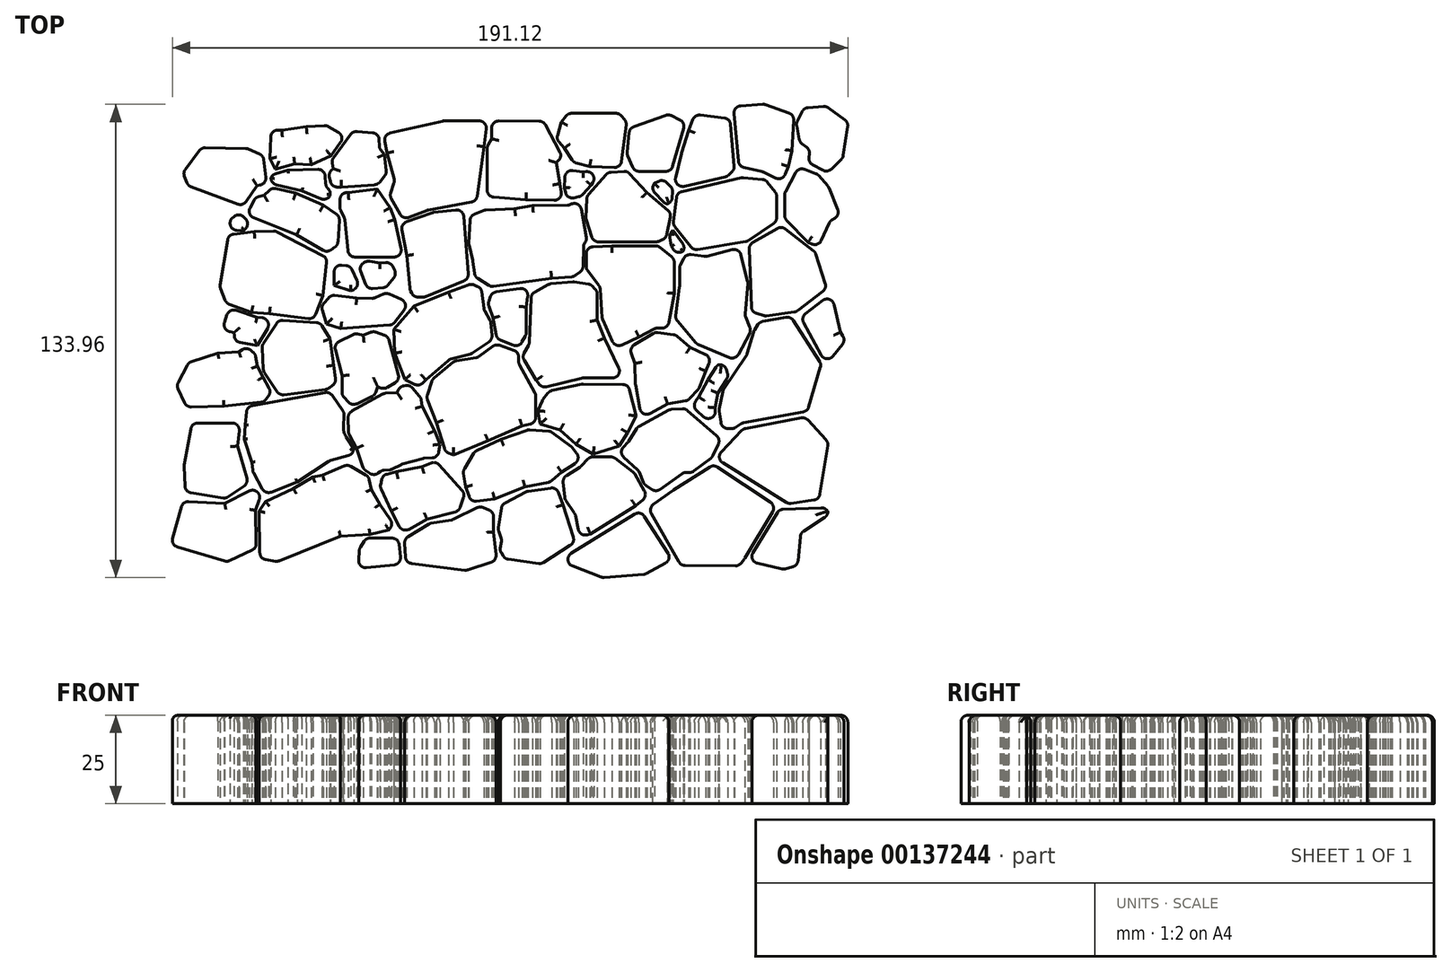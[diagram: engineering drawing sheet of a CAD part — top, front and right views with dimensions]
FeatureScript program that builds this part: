
annotation { "Feature Type Name" : "Feature", "Feature Type Description" : "" }
export const myFeature = defineFeature(function(context is Context, id is Id, definition is map)
    precondition{}
    {
        {
            var Q0;
            Q0=qCreatedBy(makeId("Top.planeOp"),FACE);
            var sketch = newSketch(context, id + "F0", { "sketchPlane" : qUnion([Q0])});
            skLineSegment(sketch, "E0", {"start": v(54.67, -32.32) * mm, "end": v(75.4, -45.2) * mm});
            skLineSegment(sketch, "E1", {"start": v(75.4, -45.2) * mm, "end": v(84.05, -43.94) * mm});
            skLineSegment(sketch, "E2", {"start": v(84.05, -43.94) * mm, "end": v(86.64, -27.84) * mm});
            skLineSegment(sketch, "E3", {"start": v(86.64, -27.84) * mm, "end": v(80.12, -20.7) * mm});
            skLineSegment(sketch, "E4", {"start": v(80.12, -20.7) * mm, "end": v(62.6, -24) * mm});
            skLineSegment(sketch, "E5", {"start": v(62.6, -24) * mm, "end": v(54.67, -32.32) * mm});
            skLineSegment(sketch, "E6", {"start": v(56.48, -23.92) * mm, "end": v(59.93, -23.92) * mm});
            skLineSegment(sketch, "E7", {"start": v(59.93, -23.92) * mm, "end": v(62.3, -22.35) * mm});
            skLineSegment(sketch, "E8", {"start": v(62.3, -22.35) * mm, "end": v(80.75, -18.97) * mm});
            skLineSegment(sketch, "E9", {"start": v(80.75, -18.97) * mm, "end": v(84.67, -5.7) * mm});
            skLineSegment(sketch, "E10", {"start": v(84.67, -5.7) * mm, "end": v(76.04, 7.81) * mm});
            skLineSegment(sketch, "E11", {"start": v(76.04, 7.81) * mm, "end": v(67.24, 6.24) * mm});
            skLineSegment(sketch, "E12", {"start": v(67.24, 6.24) * mm, "end": v(65.59, 3.8) * mm});
            skLineSegment(sketch, "E13", {"start": v(65.59, 3.8) * mm, "end": v(63.63, -3.03) * mm});
            skLineSegment(sketch, "E14", {"start": v(63.63, -3.03) * mm, "end": v(56.87, -13.08) * mm});
            skLineSegment(sketch, "E15", {"start": v(56.87, -13.08) * mm, "end": v(55.77, -18.65) * mm});
            skLineSegment(sketch, "E16", {"start": v(55.77, -18.65) * mm, "end": v(56.48, -23.92) * mm});
            skLineSegment(sketch, "E17", {"start": v(78.86, 7.58) * mm, "end": v(86.09, -5.77) * mm});
            skLineSegment(sketch, "E18", {"start": v(86.09, -5.77) * mm, "end": v(91.59, 1.14) * mm});
            skLineSegment(sketch, "E19", {"start": v(91.59, 1.14) * mm, "end": v(90.02, 3.34) * mm});
            skLineSegment(sketch, "E20", {"start": v(90.02, 3.34) * mm, "end": v(87.58, 14.25) * mm});
            skLineSegment(sketch, "E21", {"start": v(87.58, 14.25) * mm, "end": v(78.86, 7.58) * mm});
            skLineSegment(sketch, "E22", {"start": v(77.53, 9.15) * mm, "end": v(86.23, 15.81) * mm});
            skLineSegment(sketch, "E23", {"start": v(86.23, 15.81) * mm, "end": v(82.95, 26.03) * mm});
            skLineSegment(sketch, "E24", {"start": v(82.95, 26.03) * mm, "end": v(73.44, 33.42) * mm});
            skLineSegment(sketch, "E25", {"start": v(73.44, 33.42) * mm, "end": v(64.25, 28.15) * mm});
            skLineSegment(sketch, "E26", {"start": v(64.25, 28.15) * mm, "end": v(64.96, 9.07) * mm});
            skLineSegment(sketch, "E27", {"start": v(64.96, 9.07) * mm, "end": v(68.73, 7.97) * mm});
            skLineSegment(sketch, "E28", {"start": v(68.73, 7.97) * mm, "end": v(77.53, 9.15) * mm});
            skLineSegment(sketch, "E29", {"start": v(83.89, 27.6) * mm, "end": v(87.19, 34.83) * mm});
            skLineSegment(sketch, "E30", {"start": v(87.19, 34.83) * mm, "end": v(89.94, 36.56) * mm});
            skLineSegment(sketch, "E31", {"start": v(89.94, 36.56) * mm, "end": v(86.72, 44.5) * mm});
            skLineSegment(sketch, "E32", {"start": v(86.72, 44.5) * mm, "end": v(83.57, 48.1) * mm});
            skLineSegment(sketch, "E33", {"start": v(83.57, 48.1) * mm, "end": v(78.23, 50.07) * mm});
            skLineSegment(sketch, "E34", {"start": v(78.23, 50.07) * mm, "end": v(74.3, 42.76) * mm});
            skLineSegment(sketch, "E35", {"start": v(74.3, 42.76) * mm, "end": v(74.3, 35.62) * mm});
            skLineSegment(sketch, "E36", {"start": v(74.3, 35.62) * mm, "end": v(80.9, 28.78) * mm});
            skLineSegment(sketch, "E37", {"start": v(80.9, 28.78) * mm, "end": v(83.89, 27.6) * mm});
            skLineSegment(sketch, "E38", {"start": v(72.03, 34.75) * mm, "end": v(72.03, 42.53) * mm});
            skLineSegment(sketch, "E39", {"start": v(72.03, 42.53) * mm, "end": v(68.89, 46.53) * mm});
            skLineSegment(sketch, "E40", {"start": v(68.89, 46.53) * mm, "end": v(62.3, 47.16) * mm});
            skLineSegment(sketch, "E41", {"start": v(62.3, 47.16) * mm, "end": v(43.83, 42.84) * mm});
            skLineSegment(sketch, "E42", {"start": v(43.83, 42.84) * mm, "end": v(42.73, 33.89) * mm});
            skLineSegment(sketch, "E43", {"start": v(42.73, 33.89) * mm, "end": v(48.55, 26.58) * mm});
            skLineSegment(sketch, "E44", {"start": v(48.55, 26.58) * mm, "end": v(63.7, 29.1) * mm});
            skLineSegment(sketch, "E45", {"start": v(63.7, 29.1) * mm, "end": v(72.03, 34.75) * mm});
            skLineSegment(sketch, "E46", {"start": v(46.35, 25.48) * mm, "end": v(51.92, 24.78) * mm});
            skLineSegment(sketch, "E47", {"start": v(51.92, 24.78) * mm, "end": v(61.43, 27.21) * mm});
            skLineSegment(sketch, "E48", {"start": v(61.43, 27.21) * mm, "end": v(63.92, 17.47) * mm});
            skLineSegment(sketch, "E49", {"start": v(63.92, 17.47) * mm, "end": v(63.08, 8.13) * mm});
            skLineSegment(sketch, "E50", {"start": v(63.08, 8.13) * mm, "end": v(64.8, 3.89) * mm});
            skLineSegment(sketch, "E51", {"start": v(64.8, 3.89) * mm, "end": v(60.33, -4.52) * mm});
            skLineSegment(sketch, "E52", {"start": v(60.33, -4.52) * mm, "end": v(49.49, 0) * mm});
            skLineSegment(sketch, "E53", {"start": v(49.49, 0) * mm, "end": v(43.36, 7.26) * mm});
            skLineSegment(sketch, "E54", {"start": v(43.36, 7.26) * mm, "end": v(44.54, 16.06) * mm});
            skLineSegment(sketch, "E55", {"start": v(44.54, 16.06) * mm, "end": v(44.54, 21.87) * mm});
            skLineSegment(sketch, "E56", {"start": v(44.54, 21.87) * mm, "end": v(46.35, 25.48) * mm});
            skLineSegment(sketch, "E57", {"start": v(18.15, 27.45) * mm, "end": v(18.15, 21.32) * mm});
            skLineSegment(sketch, "E58", {"start": v(18.15, 21.32) * mm, "end": v(22.08, 16.14) * mm});
            skLineSegment(sketch, "E59", {"start": v(22.08, 16.14) * mm, "end": v(22.7, 7.1) * mm});
            skLineSegment(sketch, "E60", {"start": v(22.7, 7.1) * mm, "end": v(26.4, -1.06) * mm});
            skLineSegment(sketch, "E61", {"start": v(26.4, -1.06) * mm, "end": v(33.1, 1.96) * mm});
            skLineSegment(sketch, "E62", {"start": v(33.1, 1.96) * mm, "end": v(37.79, 4.51) * mm});
            skLineSegment(sketch, "E63", {"start": v(37.79, 4.51) * mm, "end": v(41.24, 4.51) * mm});
            skLineSegment(sketch, "E64", {"start": v(41.24, 4.51) * mm, "end": v(43.05, 14.33) * mm});
            skLineSegment(sketch, "E65", {"start": v(43.05, 14.33) * mm, "end": v(43.05, 20.38) * mm});
            skLineSegment(sketch, "E66", {"start": v(43.05, 20.38) * mm, "end": v(43.05, 24.07) * mm});
            skLineSegment(sketch, "E67", {"start": v(43.05, 24.07) * mm, "end": v(38.41, 27.84) * mm});
            skLineSegment(sketch, "E68", {"start": v(38.41, 27.84) * mm, "end": v(25.38, 27.84) * mm});
            skLineSegment(sketch, "E69", {"start": v(25.38, 27.84) * mm, "end": v(18.15, 27.45) * mm});
            skLineSegment(sketch, "E70", {"start": v(48.07, -17.63) * mm, "end": v(49.96, -14.96) * mm});
            skLineSegment(sketch, "E71", {"start": v(49.96, -14.96) * mm, "end": v(52.63, -10.1) * mm});
            skLineSegment(sketch, "E72", {"start": v(52.63, -10.1) * mm, "end": v(55.22, -5.93) * mm});
            skLineSegment(sketch, "E73", {"start": v(55.22, -5.93) * mm, "end": v(57.19, -5.3) * mm});
            skLineSegment(sketch, "E74", {"start": v(57.19, -5.3) * mm, "end": v(58.4, -9.09) * mm});
            skLineSegment(sketch, "E75", {"start": v(58.4, -9.09) * mm, "end": v(55.38, -13.86) * mm});
            skLineSegment(sketch, "E76", {"start": v(55.38, -13.86) * mm, "end": v(54.6, -17.95) * mm});
            skLineSegment(sketch, "E77", {"start": v(54.6, -17.95) * mm, "end": v(55.22, -24) * mm});
            skLineSegment(sketch, "E78", {"start": v(55.22, -24) * mm, "end": v(48.07, -17.63) * mm});
            skLineSegment(sketch, "E79", {"start": v(24.3, 48.58) * mm, "end": v(29.78, 48.96) * mm});
            skLineSegment(sketch, "E80", {"start": v(29.78, 48.96) * mm, "end": v(35.3, 42.93) * mm});
            skLineSegment(sketch, "E81", {"start": v(35.3, 42.93) * mm, "end": v(42.2, 37.04) * mm});
            skLineSegment(sketch, "E82", {"start": v(42.2, 37.04) * mm, "end": v(40.63, 29.89) * mm});
            skLineSegment(sketch, "E83", {"start": v(40.63, 29.89) * mm, "end": v(38.28, 28.95) * mm});
            skLineSegment(sketch, "E84", {"start": v(38.28, 28.95) * mm, "end": v(20.13, 28.95) * mm});
            skLineSegment(sketch, "E85", {"start": v(20.13, 28.95) * mm, "end": v(18.1, 35.46) * mm});
            skLineSegment(sketch, "E86", {"start": v(18.1, 35.46) * mm, "end": v(18.33, 41.83) * mm});
            skLineSegment(sketch, "E87", {"start": v(18.33, 41.83) * mm, "end": v(24.3, 48.58) * mm});
            skLineSegment(sketch, "E88", {"start": v(43.4, 2.6) * mm, "end": v(47.56, -0.89) * mm});
            skLineSegment(sketch, "E89", {"start": v(47.56, -0.89) * mm, "end": v(53.64, -3.72) * mm});
            skLineSegment(sketch, "E90", {"start": v(53.64, -3.72) * mm, "end": v(51.97, -7.63) * mm});
            skLineSegment(sketch, "E91", {"start": v(51.97, -7.63) * mm, "end": v(50.06, -12.54) * mm});
            skLineSegment(sketch, "E92", {"start": v(50.06, -12.54) * mm, "end": v(46.98, -15.95) * mm});
            skLineSegment(sketch, "E93", {"start": v(46.98, -15.95) * mm, "end": v(41.16, -16.86) * mm});
            skLineSegment(sketch, "E94", {"start": v(41.16, -16.86) * mm, "end": v(35.83, -19.86) * mm});
            skLineSegment(sketch, "E95", {"start": v(35.83, -19.86) * mm, "end": v(33.58, -19.86) * mm});
            skLineSegment(sketch, "E96", {"start": v(33.58, -19.86) * mm, "end": v(32.09, -11.46) * mm});
            skLineSegment(sketch, "E97", {"start": v(32.09, -11.46) * mm, "end": v(31.92, -5.46) * mm});
            skLineSegment(sketch, "E98", {"start": v(31.92, -5.46) * mm, "end": v(30.34, -1.05) * mm});
            skLineSegment(sketch, "E99", {"start": v(30.34, -1.05) * mm, "end": v(37.66, 3.36) * mm});
            skLineSegment(sketch, "E100", {"start": v(37.66, 3.36) * mm, "end": v(43.4, 2.6) * mm});
            skLineSegment(sketch, "E101", {"start": v(46.18, -18.24) * mm, "end": v(56.19, -26.98) * mm});
            skLineSegment(sketch, "E102", {"start": v(56.19, -26.98) * mm, "end": v(53.81, -31.95) * mm});
            skLineSegment(sketch, "E103", {"start": v(53.81, -31.95) * mm, "end": v(48.18, -36.33) * mm});
            skLineSegment(sketch, "E104", {"start": v(48.18, -36.33) * mm, "end": v(45.8, -36.33) * mm});
            skLineSegment(sketch, "E105", {"start": v(45.8, -36.33) * mm, "end": v(37.88, -41.96) * mm});
            skLineSegment(sketch, "E106", {"start": v(37.88, -41.96) * mm, "end": v(34.54, -39.66) * mm});
            skLineSegment(sketch, "E107", {"start": v(34.54, -39.66) * mm, "end": v(32.98, -35.88) * mm});
            skLineSegment(sketch, "E108", {"start": v(32.98, -35.88) * mm, "end": v(27.28, -30.62) * mm});
            skLineSegment(sketch, "E109", {"start": v(27.28, -30.62) * mm, "end": v(30.02, -27.73) * mm});
            skLineSegment(sketch, "E110", {"start": v(30.02, -27.73) * mm, "end": v(32.69, -23.5) * mm});
            skLineSegment(sketch, "E111", {"start": v(32.69, -23.5) * mm, "end": v(41.8, -18.53) * mm});
            skLineSegment(sketch, "E112", {"start": v(41.8, -18.53) * mm, "end": v(46.18, -18.24) * mm});
            skLineSegment(sketch, "E113", {"start": v(7.75, -13.33) * mm, "end": v(17.1, -11.29) * mm});
            skLineSegment(sketch, "E114", {"start": v(17.1, -11.29) * mm, "end": v(30.05, -11.46) * mm});
            skLineSegment(sketch, "E115", {"start": v(30.05, -11.46) * mm, "end": v(32.25, -20.32) * mm});
            skLineSegment(sketch, "E116", {"start": v(32.25, -20.32) * mm, "end": v(29.81, -25.03) * mm});
            skLineSegment(sketch, "E117", {"start": v(29.81, -25.03) * mm, "end": v(27.46, -28.88) * mm});
            skLineSegment(sketch, "E118", {"start": v(27.46, -28.88) * mm, "end": v(20.15, -31.16) * mm});
            skLineSegment(sketch, "E119", {"start": v(20.15, -31.16) * mm, "end": v(15.29, -28.33) * mm});
            skLineSegment(sketch, "E120", {"start": v(15.29, -28.33) * mm, "end": v(10.73, -24.32) * mm});
            skLineSegment(sketch, "E121", {"start": v(10.73, -24.32) * mm, "end": v(5.15, -22.6) * mm});
            skLineSegment(sketch, "E122", {"start": v(5.15, -22.6) * mm, "end": v(4.45, -18.82) * mm});
            skLineSegment(sketch, "E123", {"start": v(4.45, -18.82) * mm, "end": v(5.78, -15.84) * mm});
            skLineSegment(sketch, "E124", {"start": v(5.78, -15.84) * mm, "end": v(7.75, -13.33) * mm});
            skLineSegment(sketch, "E125", {"start": v(2.6, 14.2) * mm, "end": v(7.77, 17.02) * mm});
            skLineSegment(sketch, "E126", {"start": v(7.77, 17.02) * mm, "end": v(14.58, 17.61) * mm});
            skLineSegment(sketch, "E127", {"start": v(14.58, 17.61) * mm, "end": v(19.32, 16.95) * mm});
            skLineSegment(sketch, "E128", {"start": v(19.32, 16.95) * mm, "end": v(21.24, 15.03) * mm});
            skLineSegment(sketch, "E129", {"start": v(21.24, 15.03) * mm, "end": v(21.24, 6.8) * mm});
            skLineSegment(sketch, "E130", {"start": v(21.24, 6.8) * mm, "end": v(23.32, 1.72) * mm});
            skLineSegment(sketch, "E131", {"start": v(23.32, 1.72) * mm, "end": v(28.73, -9.6) * mm});
            skLineSegment(sketch, "E132", {"start": v(28.73, -9.6) * mm, "end": v(17.08, -9.6) * mm});
            skLineSegment(sketch, "E133", {"start": v(17.08, -9.6) * mm, "end": v(5.6, -12.43) * mm});
            skLineSegment(sketch, "E134", {"start": v(5.6, -12.43) * mm, "end": v(4.01, -10.18) * mm});
            skLineSegment(sketch, "E135", {"start": v(4.01, -10.18) * mm, "end": v(0, -3.6) * mm});
            skLineSegment(sketch, "E136", {"start": v(0, -3.6) * mm, "end": v(2.01, 0) * mm});
            skLineSegment(sketch, "E137", {"start": v(2.01, 0) * mm, "end": v(2.6, 14.2) * mm});
            skLineSegment(sketch, "E138", {"start": v(35.48, -43) * mm, "end": v(32.15, -45.75) * mm});
            skLineSegment(sketch, "E139", {"start": v(32.15, -45.75) * mm, "end": v(19.34, -53.74) * mm});
            skLineSegment(sketch, "E140", {"start": v(19.34, -53.74) * mm, "end": v(16.34, -54.57) * mm});
            skLineSegment(sketch, "E141", {"start": v(16.34, -54.57) * mm, "end": v(15.01, -48.16) * mm});
            skLineSegment(sketch, "E142", {"start": v(15.01, -48.16) * mm, "end": v(12.1, -43.84) * mm});
            skLineSegment(sketch, "E143", {"start": v(12.1, -43.84) * mm, "end": v(11.52, -37.84) * mm});
            skLineSegment(sketch, "E144", {"start": v(11.52, -37.84) * mm, "end": v(16.6, -34.68) * mm});
            skLineSegment(sketch, "E145", {"start": v(16.6, -34.68) * mm, "end": v(19.17, -31.94) * mm});
            skLineSegment(sketch, "E146", {"start": v(19.17, -31.94) * mm, "end": v(25.75, -31.94) * mm});
            skLineSegment(sketch, "E147", {"start": v(25.75, -31.94) * mm, "end": v(31.65, -36.43) * mm});
            skLineSegment(sketch, "E148", {"start": v(31.65, -36.43) * mm, "end": v(35.48, -43) * mm});
            skLineSegment(sketch, "E149", {"start": v(-7.45, 0) * mm, "end": v(-0.96, -2.23) * mm});
            skLineSegment(sketch, "E150", {"start": v(-0.96, -2.23) * mm, "end": v(-0.96, -5.4) * mm});
            skLineSegment(sketch, "E151", {"start": v(-0.96, -5.4) * mm, "end": v(3.86, -14.21) * mm});
            skLineSegment(sketch, "E152", {"start": v(3.86, -14.21) * mm, "end": v(3.86, -22.28) * mm});
            skLineSegment(sketch, "E153", {"start": v(3.86, -22.28) * mm, "end": v(0, -23.2) * mm});
            skLineSegment(sketch, "E154", {"start": v(0, -23.2) * mm, "end": v(-9.62, -27.36) * mm});
            skLineSegment(sketch, "E155", {"start": v(-9.62, -27.36) * mm, "end": v(-19.35, -31.35) * mm});
            skLineSegment(sketch, "E156", {"start": v(-19.35, -31.35) * mm, "end": v(-21.68, -30.52) * mm});
            skLineSegment(sketch, "E157", {"start": v(-21.68, -30.52) * mm, "end": v(-24.18, -22.2) * mm});
            skLineSegment(sketch, "E158", {"start": v(-24.18, -22.2) * mm, "end": v(-27, -15.05) * mm});
            skLineSegment(sketch, "E159", {"start": v(-27, -15.05) * mm, "end": v(-25.26, -9.89) * mm});
            skLineSegment(sketch, "E160", {"start": v(-25.26, -9.89) * mm, "end": v(-19.1, -4.81) * mm});
            skLineSegment(sketch, "E161", {"start": v(-19.1, -4.81) * mm, "end": v(-12.61, -3.81) * mm});
            skLineSegment(sketch, "E162", {"start": v(-12.61, -3.81) * mm, "end": v(-7.45, 0) * mm});
            skLineSegment(sketch, "E163", {"start": v(-8.53, 14.59) * mm, "end": v(-9.65, 11.48) * mm});
            skLineSegment(sketch, "E164", {"start": v(-9.65, 11.48) * mm, "end": v(-8.24, 7.4) * mm});
            skLineSegment(sketch, "E165", {"start": v(-8.24, 7.4) * mm, "end": v(-7.12, 1.54) * mm});
            skLineSegment(sketch, "E166", {"start": v(-7.12, 1.54) * mm, "end": v(-0.9, -0.98) * mm});
            skLineSegment(sketch, "E167", {"start": v(-0.9, -0.98) * mm, "end": v(1.18, 2.73) * mm});
            skLineSegment(sketch, "E168", {"start": v(1.18, 2.73) * mm, "end": v(1.18, 10.51) * mm});
            skLineSegment(sketch, "E169", {"start": v(1.18, 10.51) * mm, "end": v(2, 16.15) * mm});
            skLineSegment(sketch, "E170", {"start": v(2, 16.15) * mm, "end": v(-8.53, 14.59) * mm});
            skLineSegment(sketch, "E171", {"start": v(-14.54, 17.04) * mm, "end": v(-11.57, 16) * mm});
            skLineSegment(sketch, "E172", {"start": v(-11.57, 16) * mm, "end": v(-10.76, 9.7) * mm});
            skLineSegment(sketch, "E173", {"start": v(-10.76, 9.7) * mm, "end": v(-8.9, 6.5) * mm});
            skLineSegment(sketch, "E174", {"start": v(-8.9, 6.5) * mm, "end": v(-8.39, 1.32) * mm});
            skLineSegment(sketch, "E175", {"start": v(-8.39, 1.32) * mm, "end": v(-14.24, -2.68) * mm});
            skLineSegment(sketch, "E176", {"start": v(-14.24, -2.68) * mm, "end": v(-20.62, -4.39) * mm});
            skLineSegment(sketch, "E177", {"start": v(-20.62, -4.39) * mm, "end": v(-27.21, -10.1) * mm});
            skLineSegment(sketch, "E178", {"start": v(-27.21, -10.1) * mm, "end": v(-29, -12.02) * mm});
            skLineSegment(sketch, "E179", {"start": v(-29, -12.02) * mm, "end": v(-33.15, -10.1) * mm});
            skLineSegment(sketch, "E180", {"start": v(-33.15, -10.1) * mm, "end": v(-36.04, -2.6) * mm});
            skLineSegment(sketch, "E181", {"start": v(-36.04, -2.6) * mm, "end": v(-36.26, 4.21) * mm});
            skLineSegment(sketch, "E182", {"start": v(-36.26, 4.21) * mm, "end": v(-30.62, 10.73) * mm});
            skLineSegment(sketch, "E183", {"start": v(-30.62, 10.73) * mm, "end": v(-20.84, 14.74) * mm});
            skLineSegment(sketch, "E184", {"start": v(-20.84, 14.74) * mm, "end": v(-14.54, 17.04) * mm});
            skLineSegment(sketch, "E185", {"start": v(-15.13, 18.42) * mm, "end": v(-16.67, 38.22) * mm});
            skLineSegment(sketch, "E186", {"start": v(-16.67, 38.22) * mm, "end": v(-25.2, 37.24) * mm});
            skLineSegment(sketch, "E187", {"start": v(-25.2, 37.24) * mm, "end": v(-34.3, 34.1) * mm});
            skLineSegment(sketch, "E188", {"start": v(-34.3, 34.1) * mm, "end": v(-32.62, 25.07) * mm});
            skLineSegment(sketch, "E189", {"start": v(-32.62, 25.07) * mm, "end": v(-31.71, 15.4) * mm});
            skLineSegment(sketch, "E190", {"start": v(-31.71, 15.4) * mm, "end": v(-30.66, 13.31) * mm});
            skLineSegment(sketch, "E191", {"start": v(-30.66, 13.31) * mm, "end": v(-27.58, 13.31) * mm});
            skLineSegment(sketch, "E192", {"start": v(-27.58, 13.31) * mm, "end": v(-15.13, 18.42) * mm});
            skLineSegment(sketch, "E193", {"start": v(-14.66, 36.31) * mm, "end": v(-10.6, 37.92) * mm});
            skLineSegment(sketch, "E194", {"start": v(-10.6, 37.92) * mm, "end": v(-2.07, 38.27) * mm});
            skLineSegment(sketch, "E195", {"start": v(-2.07, 38.27) * mm, "end": v(2.97, 39.25) * mm});
            skLineSegment(sketch, "E196", {"start": v(2.97, 39.25) * mm, "end": v(13.19, 39.32) * mm});
            skLineSegment(sketch, "E197", {"start": v(13.19, 39.32) * mm, "end": v(16.34, 40.58) * mm});
            skLineSegment(sketch, "E198", {"start": v(16.34, 40.58) * mm, "end": v(18.3, 29.46) * mm});
            skLineSegment(sketch, "E199", {"start": v(18.3, 29.46) * mm, "end": v(17.39, 28.06) * mm});
            skLineSegment(sketch, "E200", {"start": v(17.39, 28.06) * mm, "end": v(17.25, 21.06) * mm});
            skLineSegment(sketch, "E201", {"start": v(17.25, 21.06) * mm, "end": v(14.66, 19.1) * mm});
            skLineSegment(sketch, "E202", {"start": v(14.66, 19.1) * mm, "end": v(8.36, 18.68) * mm});
            skLineSegment(sketch, "E203", {"start": v(8.36, 18.68) * mm, "end": v(-8.78, 16.23) * mm});
            skLineSegment(sketch, "E204", {"start": v(-8.78, 16.23) * mm, "end": v(-13.33, 19.1) * mm});
            skLineSegment(sketch, "E205", {"start": v(-13.33, 19.1) * mm, "end": v(-13.96, 23.58) * mm});
            skLineSegment(sketch, "E206", {"start": v(-13.96, 23.58) * mm, "end": v(-15.08, 28.27) * mm});
            skLineSegment(sketch, "E207", {"start": v(-15.08, 28.27) * mm, "end": v(-14.66, 36.31) * mm});
            skLineSegment(sketch, "E208", {"start": v(39.87, 46.7) * mm, "end": v(37.5, 45.57) * mm});
            skLineSegment(sketch, "E209", {"start": v(37.5, 45.57) * mm, "end": v(34.86, 45.77) * mm});
            skLineSegment(sketch, "E210", {"start": v(34.86, 45.77) * mm, "end": v(40.54, 39.63) * mm});
            skLineSegment(sketch, "E211", {"start": v(40.54, 39.63) * mm, "end": v(42.38, 39.76) * mm});
            skLineSegment(sketch, "E212", {"start": v(42.38, 39.76) * mm, "end": v(42.65, 43.99) * mm});
            skLineSegment(sketch, "E213", {"start": v(42.65, 43.99) * mm, "end": v(39.87, 46.7) * mm});
            skLineSegment(sketch, "E214", {"start": v(42.76, 32.2) * mm, "end": v(46.37, 27.15) * mm});
            skLineSegment(sketch, "E215", {"start": v(46.37, 27.15) * mm, "end": v(44.09, 24.49) * mm});
            skLineSegment(sketch, "E216", {"start": v(44.09, 24.49) * mm, "end": v(42.2, 27.82) * mm});
            skLineSegment(sketch, "E217", {"start": v(42.2, 27.82) * mm, "end": v(41.65, 31.6) * mm});
            skLineSegment(sketch, "E218", {"start": v(41.65, 31.6) * mm, "end": v(42.76, 32.2) * mm});
            skLineSegment(sketch, "E219", {"start": v(16.7, 41.85) * mm, "end": v(19.54, 45.05) * mm});
            skLineSegment(sketch, "E220", {"start": v(19.54, 45.05) * mm, "end": v(22.41, 49.26) * mm});
            skLineSegment(sketch, "E221", {"start": v(22.41, 49.26) * mm, "end": v(17.3, 48.73) * mm});
            skLineSegment(sketch, "E222", {"start": v(17.3, 48.73) * mm, "end": v(12.23, 49.44) * mm});
            skLineSegment(sketch, "E223", {"start": v(12.23, 49.44) * mm, "end": v(11.94, 44.2) * mm});
            skLineSegment(sketch, "E224", {"start": v(11.94, 44.2) * mm, "end": v(12.76, 41.02) * mm});
            skLineSegment(sketch, "E225", {"start": v(12.76, 41.02) * mm, "end": v(16.7, 41.85) * mm});
            skLineSegment(sketch, "E226", {"start": v(-14.49, -44.65) * mm, "end": v(-7.8, -43.87) * mm});
            skPoint(sketch, "E226.startSnap0", {"position": v(-14.49, -29.36) * mm});
            skLineSegment(sketch, "E227", {"start": v(-7.8, -43.87) * mm, "end": v(0.85, -40.41) * mm});
            skLineSegment(sketch, "E228", {"start": v(0.85, -40.41) * mm, "end": v(8, -39) * mm});
            skLineSegment(sketch, "E229", {"start": v(8, -39) * mm, "end": v(11.21, -36.25) * mm});
            skLineSegment(sketch, "E230", {"start": v(11.21, -36.25) * mm, "end": v(16.79, -32.56) * mm});
            skLineSegment(sketch, "E231", {"start": v(16.79, -32.56) * mm, "end": v(14.04, -29.1) * mm});
            skLineSegment(sketch, "E232", {"start": v(14.04, -29.1) * mm, "end": v(8.07, -24.7) * mm});
            skLineSegment(sketch, "E233", {"start": v(8.07, -24.7) * mm, "end": v(1.79, -24.23) * mm});
            skLineSegment(sketch, "E234", {"start": v(1.79, -24.23) * mm, "end": v(-5.99, -26.9) * mm});
            skLineSegment(sketch, "E235", {"start": v(-5.99, -26.9) * mm, "end": v(-13.37, -30.44) * mm});
            skLineSegment(sketch, "E236", {"start": v(-13.37, -30.44) * mm, "end": v(-16.67, -35.86) * mm});
            skLineSegment(sketch, "E237", {"start": v(-16.67, -35.86) * mm, "end": v(-15.96, -40.41) * mm});
            skLineSegment(sketch, "E238", {"start": v(-15.96, -40.41) * mm, "end": v(-14.49, -44.65) * mm});
            skLineSegment(sketch, "E239", {"start": v(-31.74, -11.59) * mm, "end": v(-28.62, -15.22) * mm});
            skLineSegment(sketch, "E240", {"start": v(-28.62, -15.22) * mm, "end": v(-28.25, -17.6) * mm});
            skLineSegment(sketch, "E241", {"start": v(-28.25, -17.6) * mm, "end": v(-24.77, -24.56) * mm});
            skLineSegment(sketch, "E242", {"start": v(-24.77, -24.56) * mm, "end": v(-23.21, -28.34) * mm});
            skLineSegment(sketch, "E243", {"start": v(-23.21, -28.34) * mm, "end": v(-23.8, -32.12) * mm});
            skLineSegment(sketch, "E244", {"start": v(-23.8, -32.12) * mm, "end": v(-27.88, -32.34) * mm});
            skLineSegment(sketch, "E245", {"start": v(-27.88, -32.34) * mm, "end": v(-34.1, -34.05) * mm});
            skLineSegment(sketch, "E246", {"start": v(-34.1, -34.05) * mm, "end": v(-37, -35.53) * mm});
            skLineSegment(sketch, "E247", {"start": v(-37, -35.53) * mm, "end": v(-39.67, -35.75) * mm});
            skLineSegment(sketch, "E248", {"start": v(-39.67, -35.75) * mm, "end": v(-41.82, -37.38) * mm});
            skLineSegment(sketch, "E249", {"start": v(-41.82, -37.38) * mm, "end": v(-44.78, -35.46) * mm});
            skLineSegment(sketch, "E250", {"start": v(-44.78, -35.46) * mm, "end": v(-46.79, -29.45) * mm});
            skLineSegment(sketch, "E251", {"start": v(-46.79, -29.45) * mm, "end": v(-49.08, -25.3) * mm});
            skLineSegment(sketch, "E252", {"start": v(-49.08, -25.3) * mm, "end": v(-49.23, -19.6) * mm});
            skLineSegment(sketch, "E253", {"start": v(-49.23, -19.6) * mm, "end": v(-39.08, -13.96) * mm});
            skLineSegment(sketch, "E254", {"start": v(-39.08, -13.96) * mm, "end": v(-35.37, -13.74) * mm});
            skLineSegment(sketch, "E255", {"start": v(-35.37, -13.74) * mm, "end": v(-34.55, -11.96) * mm});
            skLineSegment(sketch, "E256", {"start": v(-34.55, -11.96) * mm, "end": v(-31.74, -11.59) * mm});
            skLineSegment(sketch, "E257", {"start": v(-42.09, 3.6) * mm, "end": v(-37.97, 2.2) * mm});
            skLineSegment(sketch, "E258", {"start": v(-37.97, 2.2) * mm, "end": v(-34.61, -10.16) * mm});
            skLineSegment(sketch, "E259", {"start": v(-34.61, -10.16) * mm, "end": v(-38.9, -12.75) * mm});
            skLineSegment(sketch, "E260", {"start": v(-38.9, -12.75) * mm, "end": v(-40.85, -12.04) * mm});
            skLineSegment(sketch, "E261", {"start": v(-40.85, -12.04) * mm, "end": v(-41.67, -14.4) * mm});
            skLineSegment(sketch, "E262", {"start": v(-41.67, -14.4) * mm, "end": v(-48.09, -17.51) * mm});
            skLineSegment(sketch, "E263", {"start": v(-48.09, -17.51) * mm, "end": v(-50.97, -14.45) * mm});
            skLineSegment(sketch, "E264", {"start": v(-50.97, -14.45) * mm, "end": v(-50.91, -8.98) * mm});
            skLineSegment(sketch, "E265", {"start": v(-50.91, -8.98) * mm, "end": v(-53.27, -0.04) * mm});
            skLineSegment(sketch, "E266", {"start": v(-53.27, -0.04) * mm, "end": v(-47.26, 2.96) * mm});
            skLineSegment(sketch, "E267", {"start": v(-47.26, 2.96) * mm, "end": v(-44.91, 2.5) * mm});
            skLineSegment(sketch, "E268", {"start": v(-44.91, 2.5) * mm, "end": v(-42.09, 3.6) * mm});
            skLineSegment(sketch, "E269", {"start": v(-36.53, 5.47) * mm, "end": v(-31.86, 11.65) * mm});
            skLineSegment(sketch, "E270", {"start": v(-31.86, 11.65) * mm, "end": v(-38.4, 14.51) * mm});
            skLineSegment(sketch, "E271", {"start": v(-38.4, 14.51) * mm, "end": v(-41.95, 12.95) * mm});
            skLineSegment(sketch, "E272", {"start": v(-41.95, 12.95) * mm, "end": v(-46.82, 13.08) * mm});
            skLineSegment(sketch, "E273", {"start": v(-46.82, 13.08) * mm, "end": v(-54.05, 13.89) * mm});
            skLineSegment(sketch, "E274", {"start": v(-54.05, 13.89) * mm, "end": v(-56.85, 10.65) * mm});
            skLineSegment(sketch, "E275", {"start": v(-56.85, 10.65) * mm, "end": v(-55.3, 5.72) * mm});
            skLineSegment(sketch, "E276", {"start": v(-55.3, 5.72) * mm, "end": v(-51.3, 4.35) * mm});
            skLineSegment(sketch, "E277", {"start": v(-51.3, 4.35) * mm, "end": v(-36.53, 5.47) * mm});
            skLineSegment(sketch, "E278", {"start": v(-46.37, 22.47) * mm, "end": v(-43.7, 23.5) * mm});
            skLineSegment(sketch, "E279", {"start": v(-43.7, 23.5) * mm, "end": v(-40.2, 22.93) * mm});
            skLineSegment(sketch, "E280", {"start": v(-40.2, 22.93) * mm, "end": v(-37.17, 23.21) * mm});
            skLineSegment(sketch, "E281", {"start": v(-37.17, 23.21) * mm, "end": v(-35.54, 19.76) * mm});
            skLineSegment(sketch, "E282", {"start": v(-35.54, 19.76) * mm, "end": v(-38.43, 16.07) * mm});
            skLineSegment(sketch, "E283", {"start": v(-38.43, 16.07) * mm, "end": v(-43.75, 15.6) * mm});
            skLineSegment(sketch, "E284", {"start": v(-43.75, 15.6) * mm, "end": v(-46.37, 22.47) * mm});
            skLineSegment(sketch, "E285", {"start": v(9.68, 51.34) * mm, "end": v(10.67, 45.4) * mm});
            skLineSegment(sketch, "E286", {"start": v(10.67, 45.4) * mm, "end": v(11.53, 40.64) * mm});
            skLineSegment(sketch, "E287", {"start": v(11.53, 40.64) * mm, "end": v(1.1, 40.9) * mm});
            skLineSegment(sketch, "E288", {"start": v(1.1, 40.9) * mm, "end": v(-9.87, 41.7) * mm});
            skLineSegment(sketch, "E289", {"start": v(-9.87, 41.7) * mm, "end": v(-9.87, 55.9) * mm});
            skLineSegment(sketch, "E290", {"start": v(-9.87, 55.9) * mm, "end": v(-8.61, 58.14) * mm});
            skLineSegment(sketch, "E291", {"start": v(-8.61, 58.14) * mm, "end": v(-8.61, 63.16) * mm});
            skLineSegment(sketch, "E292", {"start": v(-8.61, 63.16) * mm, "end": v(6.05, 63.1) * mm});
            skLineSegment(sketch, "E293", {"start": v(6.05, 63.1) * mm, "end": v(11.4, 53.06) * mm});
            skLineSegment(sketch, "E294", {"start": v(11.4, 53.06) * mm, "end": v(9.68, 51.34) * mm});
            skLineSegment(sketch, "E295", {"start": v(-9.87, 63.17) * mm, "end": v(-10.76, 55.9) * mm});
            skLineSegment(sketch, "E296", {"start": v(-10.76, 55.9) * mm, "end": v(-12.88, 40.48) * mm});
            skLineSegment(sketch, "E297", {"start": v(-12.88, 40.48) * mm, "end": v(-26.72, 37.93) * mm});
            skLineSegment(sketch, "E298", {"start": v(-26.72, 37.93) * mm, "end": v(-33.64, 35.25) * mm});
            skLineSegment(sketch, "E299", {"start": v(-33.64, 35.25) * mm, "end": v(-37.44, 41.98) * mm});
            skLineSegment(sketch, "E300", {"start": v(-37.44, 41.98) * mm, "end": v(-36.07, 46.1) * mm});
            skLineSegment(sketch, "E301", {"start": v(-36.07, 46.1) * mm, "end": v(-38.25, 54.07) * mm});
            skLineSegment(sketch, "E302", {"start": v(-38.25, 54.07) * mm, "end": v(-39.19, 59.3) * mm});
            skLineSegment(sketch, "E303", {"start": v(-39.19, 59.3) * mm, "end": v(-22.3, 63.17) * mm});
            skLineSegment(sketch, "E304", {"start": v(-22.3, 63.17) * mm, "end": v(-9.87, 63.17) * mm});
            skLineSegment(sketch, "E305", {"start": v(-49.08, 24.65) * mm, "end": v(-33.69, 24.65) * mm});
            skLineSegment(sketch, "E306", {"start": v(-33.69, 24.65) * mm, "end": v(-36.07, 35.22) * mm});
            skLineSegment(sketch, "E307", {"start": v(-36.07, 35.22) * mm, "end": v(-37.32, 38.59) * mm});
            skLineSegment(sketch, "E308", {"start": v(-37.32, 38.59) * mm, "end": v(-40.95, 43.94) * mm});
            skLineSegment(sketch, "E309", {"start": v(-40.95, 43.94) * mm, "end": v(-49.14, 42.88) * mm});
            skLineSegment(sketch, "E310", {"start": v(-49.14, 42.88) * mm, "end": v(-51.52, 42.95) * mm});
            skLineSegment(sketch, "E311", {"start": v(-51.52, 42.95) * mm, "end": v(-51.52, 38.26) * mm});
            skLineSegment(sketch, "E312", {"start": v(-51.52, 38.26) * mm, "end": v(-50.2, 35.55) * mm});
            skLineSegment(sketch, "E313", {"start": v(-50.2, 35.55) * mm, "end": v(-49.08, 24.65) * mm});
            skLineSegment(sketch, "E314", {"start": v(-51.12, 44.45) * mm, "end": v(-40.82, 45.17) * mm});
            skLineSegment(sketch, "E315", {"start": v(-40.82, 45.17) * mm, "end": v(-38.3, 48.34) * mm});
            skLineSegment(sketch, "E316", {"start": v(-38.3, 48.34) * mm, "end": v(-38.97, 53.63) * mm});
            skLineSegment(sketch, "E317", {"start": v(-38.97, 53.63) * mm, "end": v(-40.35, 55.41) * mm});
            skLineSegment(sketch, "E318", {"start": v(-40.35, 55.41) * mm, "end": v(-40.49, 59.64) * mm});
            skLineSegment(sketch, "E319", {"start": v(-40.49, 59.64) * mm, "end": v(-47.75, 60.3) * mm});
            skLineSegment(sketch, "E320", {"start": v(-47.75, 60.3) * mm, "end": v(-53.83, 52.1) * mm});
            skLineSegment(sketch, "E321", {"start": v(-53.83, 52.1) * mm, "end": v(-53.5, 49.67) * mm});
            skLineSegment(sketch, "E322", {"start": v(-53.5, 49.67) * mm, "end": v(-54.75, 48.34) * mm});
            skLineSegment(sketch, "E323", {"start": v(-54.75, 48.34) * mm, "end": v(-53.9, 44.45) * mm});
            skLineSegment(sketch, "E324", {"start": v(-53.9, 44.45) * mm, "end": v(-51.12, 44.45) * mm});
            skLineSegment(sketch, "E325", {"start": v(-33.8, -53.42) * mm, "end": v(-26.9, -49.6) * mm});
            skLineSegment(sketch, "E326", {"start": v(-26.9, -49.6) * mm, "end": v(-17.84, -47.2) * mm});
            skLineSegment(sketch, "E327", {"start": v(-17.84, -47.2) * mm, "end": v(-16.16, -42.37) * mm});
            skLineSegment(sketch, "E328", {"start": v(-16.16, -42.37) * mm, "end": v(-24.42, -33.13) * mm});
            skLineSegment(sketch, "E329", {"start": v(-24.42, -33.13) * mm, "end": v(-28.34, -34.67) * mm});
            skLineSegment(sketch, "E330", {"start": v(-28.34, -34.67) * mm, "end": v(-35.54, -36.14) * mm});
            skLineSegment(sketch, "E331", {"start": v(-35.54, -36.14) * mm, "end": v(-39.46, -37.12) * mm});
            skLineSegment(sketch, "E332", {"start": v(-39.46, -37.12) * mm, "end": v(-40.16, -40.41) * mm});
            skLineSegment(sketch, "E333", {"start": v(-40.16, -40.41) * mm, "end": v(-37.01, -47.2) * mm});
            skLineSegment(sketch, "E334", {"start": v(-37.01, -47.2) * mm, "end": v(-33.8, -53.42) * mm});
            skLineSegment(sketch, "E335", {"start": v(-49.37, -34.13) * mm, "end": v(-43.4, -37.5) * mm});
            skLineSegment(sketch, "E336", {"start": v(-43.4, -37.5) * mm, "end": v(-42.62, -41.2) * mm});
            skLineSegment(sketch, "E337", {"start": v(-42.62, -41.2) * mm, "end": v(-40.18, -45.36) * mm});
            skLineSegment(sketch, "E338", {"start": v(-40.18, -45.36) * mm, "end": v(-36.41, -51.02) * mm});
            skLineSegment(sketch, "E339", {"start": v(-36.41, -51.02) * mm, "end": v(-37.67, -52.59) * mm});
            skLineSegment(sketch, "E340", {"start": v(-37.67, -52.59) * mm, "end": v(-43, -53.92) * mm});
            skLineSegment(sketch, "E341", {"start": v(-43, -53.92) * mm, "end": v(-51.41, -54.4) * mm});
            skLineSegment(sketch, "E342", {"start": v(-51.41, -54.4) * mm, "end": v(-69.24, -61.54) * mm});
            skLineSegment(sketch, "E343", {"start": v(-69.24, -61.54) * mm, "end": v(-74.19, -60.76) * mm});
            skLineSegment(sketch, "E344", {"start": v(-74.19, -60.76) * mm, "end": v(-74.35, -47.25) * mm});
            skLineSegment(sketch, "E345", {"start": v(-74.35, -47.25) * mm, "end": v(-72.62, -44.58) * mm});
            skLineSegment(sketch, "E346", {"start": v(-72.62, -44.58) * mm, "end": v(-64.69, -40.89) * mm});
            skLineSegment(sketch, "E347", {"start": v(-64.69, -40.89) * mm, "end": v(-59.19, -37.59) * mm});
            skLineSegment(sketch, "E348", {"start": v(-59.19, -37.59) * mm, "end": v(-56.44, -37.12) * mm});
            skLineSegment(sketch, "E349", {"start": v(-56.44, -37.12) * mm, "end": v(-49.37, -34.13) * mm});
            skLineSegment(sketch, "E350", {"start": v(-72.62, -42.54) * mm, "end": v(-63.59, -39) * mm});
            skLineSegment(sketch, "E351", {"start": v(-63.59, -39) * mm, "end": v(-54.48, -33.03) * mm});
            skLineSegment(sketch, "E352", {"start": v(-54.48, -33.03) * mm, "end": v(-47.96, -31.23) * mm});
            skLineSegment(sketch, "E353", {"start": v(-47.96, -31.23) * mm, "end": v(-47.64, -29.65) * mm});
            skLineSegment(sketch, "E354", {"start": v(-47.64, -29.65) * mm, "end": v(-50.63, -24.94) * mm});
            skLineSegment(sketch, "E355", {"start": v(-50.63, -24.94) * mm, "end": v(-50.31, -19.52) * mm});
            skLineSegment(sketch, "E356", {"start": v(-50.31, -19.52) * mm, "end": v(-54.48, -13.48) * mm});
            skLineSegment(sketch, "E357", {"start": v(-54.48, -13.48) * mm, "end": v(-77.8, -17.72) * mm});
            skLineSegment(sketch, "E358", {"start": v(-77.8, -17.72) * mm, "end": v(-78.35, -22.82) * mm});
            skLineSegment(sketch, "E359", {"start": v(-78.35, -22.82) * mm, "end": v(-78.59, -26.9) * mm});
            skLineSegment(sketch, "E360", {"start": v(-78.59, -26.9) * mm, "end": v(-76.47, -33.5) * mm});
            skLineSegment(sketch, "E361", {"start": v(-76.47, -33.5) * mm, "end": v(-76.15, -36.17) * mm});
            skLineSegment(sketch, "E362", {"start": v(-76.15, -36.17) * mm, "end": v(-72.62, -42.54) * mm});
            skLineSegment(sketch, "E363", {"start": v(-68.85, 6.81) * mm, "end": v(-57.12, 5.98) * mm});
            skLineSegment(sketch, "E364", {"start": v(-57.12, 5.98) * mm, "end": v(-54.29, 1.49) * mm});
            skLineSegment(sketch, "E365", {"start": v(-54.29, 1.49) * mm, "end": v(-53.37, -6) * mm});
            skLineSegment(sketch, "E366", {"start": v(-53.37, -6) * mm, "end": v(-52.62, -10.91) * mm});
            skLineSegment(sketch, "E367", {"start": v(-52.62, -10.91) * mm, "end": v(-55.04, -12.74) * mm});
            skLineSegment(sketch, "E368", {"start": v(-55.04, -12.74) * mm, "end": v(-68.6, -14.49) * mm});
            skLineSegment(sketch, "E369", {"start": v(-68.6, -14.49) * mm, "end": v(-73.18, -7.67) * mm});
            skLineSegment(sketch, "E370", {"start": v(-73.18, -7.67) * mm, "end": v(-73.6, -0.43) * mm});
            skLineSegment(sketch, "E371", {"start": v(-73.6, -0.43) * mm, "end": v(-68.85, 6.81) * mm});
            skLineSegment(sketch, "E372", {"start": v(-55.16, 24.41) * mm, "end": v(-56.3, 13.73) * mm});
            skPoint(sketch, "E372.endSnap0", {"position": v(-40.18, 13.73) * mm});
            skLineSegment(sketch, "E373", {"start": v(-56.3, 13.73) * mm, "end": v(-58.95, 7.05) * mm});
            skLineSegment(sketch, "E374", {"start": v(-58.95, 7.05) * mm, "end": v(-71.47, 8.54) * mm});
            skLineSegment(sketch, "E375", {"start": v(-71.47, 8.54) * mm, "end": v(-76.58, 8.98) * mm});
            skLineSegment(sketch, "E376", {"start": v(-76.58, 8.98) * mm, "end": v(-83.72, 11.63) * mm});
            skLineSegment(sketch, "E377", {"start": v(-83.72, 11.63) * mm, "end": v(-85.48, 16.21) * mm});
            skLineSegment(sketch, "E378", {"start": v(-85.48, 16.21) * mm, "end": v(-83.1, 30.94) * mm});
            skLineSegment(sketch, "E379", {"start": v(-83.1, 30.94) * mm, "end": v(-75.79, 31.9) * mm});
            skLineSegment(sketch, "E380", {"start": v(-75.79, 31.9) * mm, "end": v(-69.8, 32) * mm});
            skLineSegment(sketch, "E381", {"start": v(-69.8, 32) * mm, "end": v(-55.16, 24.41) * mm});
            skLineSegment(sketch, "E382", {"start": v(-48.63, 22.12) * mm, "end": v(-45.81, 16.13) * mm});
            skLineSegment(sketch, "E383", {"start": v(-45.81, 16.13) * mm, "end": v(-48.46, 15.07) * mm});
            skLineSegment(sketch, "E384", {"start": v(-48.46, 15.07) * mm, "end": v(-53.13, 16.57) * mm});
            skLineSegment(sketch, "E385", {"start": v(-53.13, 16.57) * mm, "end": v(-53.22, 22.56) * mm});
            skLineSegment(sketch, "E386", {"start": v(-53.22, 22.56) * mm, "end": v(-48.63, 22.12) * mm});
            skLineSegment(sketch, "E387", {"start": v(-70.76, 44.25) * mm, "end": v(-72.97, 42.13) * mm});
            skLineSegment(sketch, "E388", {"start": v(-72.97, 42.13) * mm, "end": v(-75.43, 41.52) * mm});
            skLineSegment(sketch, "E389", {"start": v(-75.43, 41.52) * mm, "end": v(-78, 36.58) * mm});
            skLineSegment(sketch, "E390", {"start": v(-78, 36.58) * mm, "end": v(-63.8, 30.94) * mm});
            skLineSegment(sketch, "E391", {"start": v(-63.8, 30.94) * mm, "end": v(-55.16, 25.91) * mm});
            skLineSegment(sketch, "E392", {"start": v(-55.16, 25.91) * mm, "end": v(-52.16, 28.03) * mm});
            skLineSegment(sketch, "E393", {"start": v(-52.16, 28.03) * mm, "end": v(-51.63, 36.14) * mm});
            skLineSegment(sketch, "E394", {"start": v(-51.63, 36.14) * mm, "end": v(-56.22, 39.31) * mm});
            skLineSegment(sketch, "E395", {"start": v(-56.22, 39.31) * mm, "end": v(-64.06, 42.75) * mm});
            skLineSegment(sketch, "E396", {"start": v(-64.06, 42.75) * mm, "end": v(-70.76, 44.25) * mm});
            skLineSegment(sketch, "E397", {"start": v(-71.4, 45.5) * mm, "end": v(-62.3, 43.44) * mm});
            skLineSegment(sketch, "E398", {"start": v(-62.3, 43.44) * mm, "end": v(-54.87, 40.26) * mm});
            skLineSegment(sketch, "E399", {"start": v(-54.87, 40.26) * mm, "end": v(-54, 43.07) * mm});
            skLineSegment(sketch, "E400", {"start": v(-54, 43.07) * mm, "end": v(-55.5, 44.63) * mm});
            skLineSegment(sketch, "E401", {"start": v(-55.5, 44.63) * mm, "end": v(-55.8, 49.49) * mm});
            skLineSegment(sketch, "E402", {"start": v(-55.8, 49.49) * mm, "end": v(-66.22, 49.24) * mm});
            skLineSegment(sketch, "E403", {"start": v(-66.22, 49.24) * mm, "end": v(-70.9, 47.87) * mm});
            skLineSegment(sketch, "E404", {"start": v(-70.9, 47.87) * mm, "end": v(-71.4, 45.5) * mm});
            skLineSegment(sketch, "E405", {"start": v(-71.02, 60.58) * mm, "end": v(-67.97, 60.58) * mm});
            skLineSegment(sketch, "E406", {"start": v(-67.97, 60.58) * mm, "end": v(-61.05, 61.52) * mm});
            skLineSegment(sketch, "E407", {"start": v(-61.05, 61.52) * mm, "end": v(-55.31, 61.9) * mm});
            skLineSegment(sketch, "E408", {"start": v(-55.31, 61.9) * mm, "end": v(-50.07, 58.84) * mm});
            skLineSegment(sketch, "E409", {"start": v(-50.07, 58.84) * mm, "end": v(-54.06, 53.3) * mm});
            skLineSegment(sketch, "E410", {"start": v(-54.06, 53.3) * mm, "end": v(-59.61, 50.8) * mm});
            skLineSegment(sketch, "E411", {"start": v(-59.61, 50.8) * mm, "end": v(-64.35, 50.98) * mm});
            skLineSegment(sketch, "E412", {"start": v(-64.35, 50.98) * mm, "end": v(-69.77, 49.49) * mm});
            skLineSegment(sketch, "E413", {"start": v(-69.77, 49.49) * mm, "end": v(-71.4, 52.48) * mm});
            skLineSegment(sketch, "E414", {"start": v(-71.4, 52.48) * mm, "end": v(-71.02, 60.58) * mm});
            skLineSegment(sketch, "E415", {"start": v(-74.9, -0.43) * mm, "end": v(-70.46, 7.07) * mm});
            skLineSegment(sketch, "E416", {"start": v(-70.46, 7.07) * mm, "end": v(-75.01, 7.62) * mm});
            skLineSegment(sketch, "E417", {"start": v(-75.01, 7.62) * mm, "end": v(-82.84, 10.18) * mm});
            skLineSegment(sketch, "E418", {"start": v(-82.84, 10.18) * mm, "end": v(-84.95, 3.96) * mm});
            skLineSegment(sketch, "E419", {"start": v(-84.95, 3.96) * mm, "end": v(-81.45, 3.3) * mm});
            skLineSegment(sketch, "E420", {"start": v(-81.45, 3.3) * mm, "end": v(-81.34, 0.74) * mm});
            skLineSegment(sketch, "E421", {"start": v(-81.34, 0.74) * mm, "end": v(-74.9, -0.43) * mm});
            skLineSegment(sketch, "E422", {"start": v(-75.53, -2.74) * mm, "end": v(-74.95, -6.32) * mm});
            skLineSegment(sketch, "E423", {"start": v(-74.95, -6.32) * mm, "end": v(-73.28, -9.4) * mm});
            skLineSegment(sketch, "E424", {"start": v(-73.28, -9.4) * mm, "end": v(-70.95, -13.64) * mm});
            skLineSegment(sketch, "E425", {"start": v(-70.95, -13.64) * mm, "end": v(-73.04, -16.39) * mm});
            skLineSegment(sketch, "E426", {"start": v(-73.04, -16.39) * mm, "end": v(-84.35, -17.55) * mm});
            skLineSegment(sketch, "E427", {"start": v(-84.35, -17.55) * mm, "end": v(-94.92, -17.8) * mm});
            skLineSegment(sketch, "E428", {"start": v(-94.92, -17.8) * mm, "end": v(-97.75, -11.73) * mm});
            skLineSegment(sketch, "E429", {"start": v(-97.75, -11.73) * mm, "end": v(-94.34, -5.24) * mm});
            skLineSegment(sketch, "E430", {"start": v(-94.34, -5.24) * mm, "end": v(-86.1, -2.57) * mm});
            skLineSegment(sketch, "E431", {"start": v(-86.1, -2.57) * mm, "end": v(-80.1, -2.16) * mm});
            skLineSegment(sketch, "E432", {"start": v(-80.1, -2.16) * mm, "end": v(-77.94, -0.83) * mm});
            skLineSegment(sketch, "E433", {"start": v(-77.94, -0.83) * mm, "end": v(-75.53, -2.74) * mm});
            skLineSegment(sketch, "E434", {"start": v(11.05, 62.86) * mm, "end": v(9.73, 58) * mm});
            skLineSegment(sketch, "E435", {"start": v(9.73, 58) * mm, "end": v(11.93, 55.45) * mm});
            skLineSegment(sketch, "E436", {"start": v(11.93, 55.45) * mm, "end": v(14.58, 51.49) * mm});
            skLineSegment(sketch, "E437", {"start": v(14.58, 51.49) * mm, "end": v(19.16, 50.25) * mm});
            skLineSegment(sketch, "E438", {"start": v(19.16, 50.25) * mm, "end": v(27.89, 49.9) * mm});
            skLineSegment(sketch, "E439", {"start": v(27.89, 49.9) * mm, "end": v(29.56, 62.95) * mm});
            skLineSegment(sketch, "E440", {"start": v(29.56, 62.95) * mm, "end": v(27.45, 65.33) * mm});
            skLineSegment(sketch, "E441", {"start": v(27.45, 65.33) * mm, "end": v(13.08, 65.33) * mm});
            skLineSegment(sketch, "E442", {"start": v(13.08, 65.33) * mm, "end": v(11.05, 62.86) * mm});
            skLineSegment(sketch, "E443", {"start": v(31.8, 48.9) * mm, "end": v(42.22, 48.9) * mm});
            skLineSegment(sketch, "E444", {"start": v(42.22, 48.9) * mm, "end": v(46.15, 62.74) * mm});
            skLineSegment(sketch, "E445", {"start": v(46.15, 62.74) * mm, "end": v(41.47, 65.05) * mm});
            skLineSegment(sketch, "E446", {"start": v(41.47, 65.05) * mm, "end": v(30.44, 61.12) * mm});
            skLineSegment(sketch, "E447", {"start": v(30.44, 61.12) * mm, "end": v(29.69, 53.83) * mm});
            skLineSegment(sketch, "E448", {"start": v(29.69, 53.83) * mm, "end": v(31.8, 48.9) * mm});
            skLineSegment(sketch, "E449", {"start": v(43.1, 45.66) * mm, "end": v(45.21, 44.48) * mm});
            skLineSegment(sketch, "E450", {"start": v(45.21, 44.48) * mm, "end": v(58.05, 47.47) * mm});
            skLineSegment(sketch, "E451", {"start": v(58.05, 47.47) * mm, "end": v(60.1, 49.47) * mm});
            skLineSegment(sketch, "E452", {"start": v(60.1, 49.47) * mm, "end": v(58.86, 63.8) * mm});
            skLineSegment(sketch, "E453", {"start": v(58.86, 63.8) * mm, "end": v(48.89, 64.99) * mm});
            skLineSegment(sketch, "E454", {"start": v(48.89, 64.99) * mm, "end": v(47.08, 60.5) * mm});
            skLineSegment(sketch, "E455", {"start": v(47.08, 60.5) * mm, "end": v(45.09, 54.02) * mm});
            skLineSegment(sketch, "E456", {"start": v(45.09, 54.02) * mm, "end": v(43.1, 45.66) * mm});
            skLineSegment(sketch, "E457", {"start": v(68.03, 48.78) * mm, "end": v(73.64, 46.1) * mm});
            skLineSegment(sketch, "E458", {"start": v(73.64, 46.1) * mm, "end": v(75.38, 50.28) * mm});
            skLineSegment(sketch, "E459", {"start": v(75.38, 50.28) * mm, "end": v(76.38, 54.77) * mm});
            skLineSegment(sketch, "E460", {"start": v(76.38, 54.77) * mm, "end": v(76.94, 64.86) * mm});
            skLineSegment(sketch, "E461", {"start": v(76.94, 64.86) * mm, "end": v(68.46, 67.92) * mm});
            skLineSegment(sketch, "E462", {"start": v(68.46, 67.92) * mm, "end": v(59.8, 67.3) * mm});
            skLineSegment(sketch, "E463", {"start": v(59.8, 67.3) * mm, "end": v(61.36, 50.28) * mm});
            skLineSegment(sketch, "E464", {"start": v(61.36, 50.28) * mm, "end": v(68.03, 48.78) * mm});
            skLineSegment(sketch, "E465", {"start": v(81.43, 55.01) * mm, "end": v(81, 51.46) * mm});
            skLineSegment(sketch, "E466", {"start": v(81, 51.46) * mm, "end": v(86.42, 48.53) * mm});
            skLineSegment(sketch, "E467", {"start": v(86.42, 48.53) * mm, "end": v(90.78, 52.7) * mm});
            skLineSegment(sketch, "E468", {"start": v(90.78, 52.7) * mm, "end": v(92.34, 62.74) * mm});
            skLineSegment(sketch, "E469", {"start": v(92.34, 62.74) * mm, "end": v(85.98, 67.36) * mm});
            skLineSegment(sketch, "E470", {"start": v(85.98, 67.36) * mm, "end": v(79.8, 66.86) * mm});
            skLineSegment(sketch, "E471", {"start": v(79.8, 66.86) * mm, "end": v(77.56, 62.5) * mm});
            skLineSegment(sketch, "E472", {"start": v(77.56, 62.5) * mm, "end": v(78.56, 57.26) * mm});
            skLineSegment(sketch, "E473", {"start": v(78.56, 57.26) * mm, "end": v(81.43, 55.01) * mm});
            skLineSegment(sketch, "E474", {"start": v(62.96, -60.76) * mm, "end": v(71.86, -45.84) * mm});
            skLineSegment(sketch, "E475", {"start": v(71.86, -45.84) * mm, "end": v(54.23, -34.12) * mm});
            skLineSegment(sketch, "E476", {"start": v(54.23, -34.12) * mm, "end": v(42.77, -41.35) * mm});
            skLineSegment(sketch, "E477", {"start": v(42.77, -41.35) * mm, "end": v(35.72, -46.46) * mm});
            skLineSegment(sketch, "E478", {"start": v(35.72, -46.46) * mm, "end": v(44.97, -62.68) * mm});
            skLineSegment(sketch, "E479", {"start": v(44.97, -62.68) * mm, "end": v(61.37, -62.77) * mm});
            skLineSegment(sketch, "E480", {"start": v(61.37, -62.77) * mm, "end": v(62.96, -60.76) * mm});
            skLineSegment(sketch, "E481", {"start": v(-4.86, -60.76) * mm, "end": v(-6.26, -58.51) * mm});
            skLineSegment(sketch, "E482", {"start": v(-6.26, -58.51) * mm, "end": v(-5.8, -55.3) * mm});
            skLineSegment(sketch, "E483", {"start": v(-5.8, -55.3) * mm, "end": v(-6.75, -52.48) * mm});
            skLineSegment(sketch, "E484", {"start": v(-6.75, -52.48) * mm, "end": v(-5.7, -45.45) * mm});
            skLineSegment(sketch, "E485", {"start": v(-5.7, -45.45) * mm, "end": v(1.43, -41.68) * mm});
            skLineSegment(sketch, "E486", {"start": v(1.43, -41.68) * mm, "end": v(9.7, -40.52) * mm});
            skLineSegment(sketch, "E487", {"start": v(9.7, -40.52) * mm, "end": v(11.6, -45.45) * mm});
            skLineSegment(sketch, "E488", {"start": v(11.6, -45.45) * mm, "end": v(14.95, -56.14) * mm});
            skLineSegment(sketch, "E489", {"start": v(14.95, -56.14) * mm, "end": v(5.41, -62.23) * mm});
            skLineSegment(sketch, "E490", {"start": v(5.41, -62.23) * mm, "end": v(-4.86, -60.76) * mm});
            skLineSegment(sketch, "E491", {"start": v(42.44, -61) * mm, "end": v(33.5, -47.1) * mm});
            skLineSegment(sketch, "E492", {"start": v(33.5, -47.1) * mm, "end": v(10.48, -61.39) * mm});
            skLineSegment(sketch, "E493", {"start": v(10.48, -61.39) * mm, "end": v(22.8, -66.1) * mm});
            skLineSegment(sketch, "E494", {"start": v(22.8, -66.1) * mm, "end": v(34.83, -65.16) * mm});
            skLineSegment(sketch, "E495", {"start": v(34.83, -65.16) * mm, "end": v(42.44, -61) * mm});
            skLineSegment(sketch, "E496", {"start": v(-8.06, -53.21) * mm, "end": v(-8.06, -47.52) * mm});
            skLineSegment(sketch, "E497", {"start": v(-8.06, -47.52) * mm, "end": v(-11.89, -45.93) * mm});
            skLineSegment(sketch, "E498", {"start": v(-11.89, -45.93) * mm, "end": v(-19.73, -49.76) * mm});
            skLineSegment(sketch, "E499", {"start": v(-19.73, -49.76) * mm, "end": v(-26.08, -50.78) * mm});
            skLineSegment(sketch, "E500", {"start": v(-26.08, -50.78) * mm, "end": v(-33.27, -55.17) * mm});
            skLineSegment(sketch, "E501", {"start": v(-33.27, -55.17) * mm, "end": v(-32.9, -61.9) * mm});
            skLineSegment(sketch, "E502", {"start": v(-32.9, -61.9) * mm, "end": v(-15.8, -64.05) * mm});
            skLineSegment(sketch, "E503", {"start": v(-15.8, -64.05) * mm, "end": v(-7.22, -61.25) * mm});
            skLineSegment(sketch, "E504", {"start": v(-7.22, -61.25) * mm, "end": v(-8.06, -53.21) * mm});
            skLineSegment(sketch, "E505", {"start": v(77.95, -62.72) * mm, "end": v(78.8, -53.54) * mm});
            skLineSegment(sketch, "E506", {"start": v(78.8, -53.54) * mm, "end": v(86.8, -48.32) * mm});
            skLineSegment(sketch, "E507", {"start": v(86.8, -48.32) * mm, "end": v(86.27, -46.27) * mm});
            skLineSegment(sketch, "E508", {"start": v(86.27, -46.27) * mm, "end": v(72.8, -46.8) * mm});
            skLineSegment(sketch, "E509", {"start": v(72.8, -46.8) * mm, "end": v(63.88, -61.4) * mm});
            skLineSegment(sketch, "E510", {"start": v(63.88, -61.4) * mm, "end": v(73.99, -63.78) * mm});
            skLineSegment(sketch, "E511", {"start": v(73.99, -63.78) * mm, "end": v(77.95, -62.72) * mm});
            skLineSegment(sketch, "E512", {"start": v(-73.24, 53.38) * mm, "end": v(-72.28, 45.3) * mm});
            skLineSegment(sketch, "E513", {"start": v(-72.28, 45.3) * mm, "end": v(-75.02, 44.85) * mm});
            skLineSegment(sketch, "E514", {"start": v(-75.02, 44.85) * mm, "end": v(-78.95, 39.07) * mm});
            skLineSegment(sketch, "E515", {"start": v(-78.95, 39.07) * mm, "end": v(-94.52, 44.85) * mm});
            skLineSegment(sketch, "E516", {"start": v(-94.52, 44.85) * mm, "end": v(-95.93, 48.63) * mm});
            skLineSegment(sketch, "E517", {"start": v(-95.93, 48.63) * mm, "end": v(-90.66, 55.6) * mm});
            skLineSegment(sketch, "E518", {"start": v(-90.66, 55.6) * mm, "end": v(-77.84, 55.38) * mm});
            skLineSegment(sketch, "E519", {"start": v(-77.84, 55.38) * mm, "end": v(-73.24, 53.38) * mm});
            skLineSegment(sketch, "E520", {"start": v(-80.05, 37.4) * mm, "end": v(-76.71, 33.79) * mm});
            skPoint(sketch, "E520.endSnap0", {"position": v(-76.71, 39.05) * mm});
            skLineSegment(sketch, "E521", {"start": v(-76.71, 33.79) * mm, "end": v(-78.87, 32.14) * mm});
            skLineSegment(sketch, "E522", {"start": v(-78.87, 32.14) * mm, "end": v(-85.63, 32.37) * mm});
            skLineSegment(sketch, "E523", {"start": v(-85.63, 32.37) * mm, "end": v(-80.05, 37.4) * mm});
            skLineSegment(sketch, "E524", {"start": v(-79.78, -22.35) * mm, "end": v(-80.48, -28.87) * mm});
            skLineSegment(sketch, "E525", {"start": v(-80.48, -28.87) * mm, "end": v(-77.45, -39.35) * mm});
            skLineSegment(sketch, "E526", {"start": v(-77.45, -39.35) * mm, "end": v(-83.78, -43.68) * mm});
            skLineSegment(sketch, "E527", {"start": v(-83.78, -43.68) * mm, "end": v(-95.33, -41.8) * mm});
            skLineSegment(sketch, "E528", {"start": v(-95.33, -41.8) * mm, "end": v(-95.66, -34.46) * mm});
            skLineSegment(sketch, "E529", {"start": v(-95.66, -34.46) * mm, "end": v(-93.44, -22.35) * mm});
            skLineSegment(sketch, "E530", {"start": v(-93.44, -22.35) * mm, "end": v(-79.78, -22.35) * mm});
            skLineSegment(sketch, "E531", {"start": v(-83.39, -61.62) * mm, "end": v(-75.2, -57.77) * mm});
            skLineSegment(sketch, "E532", {"start": v(-75.2, -57.77) * mm, "end": v(-75.41, -47.07) * mm});
            skLineSegment(sketch, "E533", {"start": v(-75.41, -47.07) * mm, "end": v(-74.08, -43.29) * mm});
            skLineSegment(sketch, "E534", {"start": v(-74.08, -43.29) * mm, "end": v(-75.27, -40.63) * mm});
            skLineSegment(sketch, "E535", {"start": v(-75.27, -40.63) * mm, "end": v(-84.16, -45.1) * mm});
            skLineSegment(sketch, "E536", {"start": v(-84.16, -45.1) * mm, "end": v(-95.91, -44.48) * mm});
            skLineSegment(sketch, "E537", {"start": v(-95.91, -44.48) * mm, "end": v(-99.41, -56.86) * mm});
            skLineSegment(sketch, "E538", {"start": v(-99.41, -56.86) * mm, "end": v(-83.39, -61.62) * mm});
            skLineSegment(sketch, "E539", {"start": v(-34.2, -62.28) * mm, "end": v(-34.99, -54.95) * mm});
            skLineSegment(sketch, "E540", {"start": v(-34.99, -54.95) * mm, "end": v(-44.04, -54.89) * mm});
            skLineSegment(sketch, "E541", {"start": v(-44.04, -54.89) * mm, "end": v(-46.02, -57.93) * mm});
            skLineSegment(sketch, "E542", {"start": v(-46.02, -57.93) * mm, "end": v(-46.41, -63.54) * mm});
            skLineSegment(sketch, "E543", {"start": v(-46.41, -63.54) * mm, "end": v(-34.2, -62.28) * mm});
            skSolve(sketch);
        }
        {
            var Q0;
            Q0 = qSketchRegion(id + "F0", true);
            extrude(context, id + "F1", {"entities" : qUnion([Q0]), "depth" : 25 * mm});
        }
        {
            var Q0;
            Q0=makeQuery(id+"F1.opExtrude","SWEPT_EDGE",EDGE,{"disambiguationData":[OSD([sQuery(id+"F0.wireOp",EDGE,"E502"),sQuery(id+"F0.wireOp",EDGE,"E503")])]});
            var Q1;
            Q1=makeQuery(id+"F1.opExtrude","SWEPT_EDGE",EDGE,{"disambiguationData":[OSD([sQuery(id+"F0.wireOp",EDGE,"E503"),sQuery(id+"F0.wireOp",EDGE,"E504")])]});
            var Q2;
            Q2=makeQuery(id+"F1.opExtrude","SWEPT_EDGE",EDGE,{"disambiguationData":[OSD([sQuery(id+"F0.wireOp",EDGE,"E501"),sQuery(id+"F0.wireOp",EDGE,"E502")])]});
            var Q3;
            Q3=makeQuery(id+"F1.opExtrude","SWEPT_EDGE",EDGE,{"disambiguationData":[OSD([sQuery(id+"F0.wireOp",EDGE,"E496"),sQuery(id+"F0.wireOp",EDGE,"E497")])]});
            var Q4;
            Q4=makeQuery(id+"F1.opExtrude","SWEPT_EDGE",EDGE,{"disambiguationData":[OSD([sQuery(id+"F0.wireOp",EDGE,"E497"),sQuery(id+"F0.wireOp",EDGE,"E498")])]});
            var Q5;
            Q5=makeQuery(id+"F1.opExtrude","SWEPT_EDGE",EDGE,{"disambiguationData":[OSD([sQuery(id+"F0.wireOp",EDGE,"E498"),sQuery(id+"F0.wireOp",EDGE,"E499")])]});
            var Q6;
            Q6=makeQuery(id+"F1.opExtrude","SWEPT_EDGE",EDGE,{"disambiguationData":[OSD([sQuery(id+"F0.wireOp",EDGE,"E499"),sQuery(id+"F0.wireOp",EDGE,"E500")])]});
            var Q7;
            Q7=makeQuery(id+"F1.opExtrude","SWEPT_EDGE",EDGE,{"disambiguationData":[OSD([sQuery(id+"F0.wireOp",EDGE,"E489"),sQuery(id+"F0.wireOp",EDGE,"E490")])]});
            var Q8;
            Q8=makeQuery(id+"F1.opExtrude","SWEPT_EDGE",EDGE,{"disambiguationData":[OSD([sQuery(id+"F0.wireOp",EDGE,"E481"),sQuery(id+"F0.wireOp",EDGE,"E490")])]});
            var Q9;
            Q9=makeQuery(id+"F1.opExtrude","SWEPT_EDGE",EDGE,{"disambiguationData":[OSD([sQuery(id+"F0.wireOp",EDGE,"E481"),sQuery(id+"F0.wireOp",EDGE,"E482")])]});
            var Q10;
            Q10=makeQuery(id+"F1.opExtrude","SWEPT_EDGE",EDGE,{"disambiguationData":[OSD([sQuery(id+"F0.wireOp",EDGE,"E488"),sQuery(id+"F0.wireOp",EDGE,"E489")])]});
            var Q11;
            Q11=makeQuery(id+"F1.opExtrude","SWEPT_EDGE",EDGE,{"disambiguationData":[OSD([sQuery(id+"F0.wireOp",EDGE,"E486"),sQuery(id+"F0.wireOp",EDGE,"E487")])]});
            var Q12;
            Q12=makeQuery(id+"F1.opExtrude","SWEPT_EDGE",EDGE,{"disambiguationData":[OSD([sQuery(id+"F0.wireOp",EDGE,"E485"),sQuery(id+"F0.wireOp",EDGE,"E486")])]});
            var Q13;
            Q13=makeQuery(id+"F1.opExtrude","SWEPT_EDGE",EDGE,{"disambiguationData":[OSD([sQuery(id+"F0.wireOp",EDGE,"E484"),sQuery(id+"F0.wireOp",EDGE,"E485")])]});
            var Q14;
            Q14=makeQuery(id+"F1.opExtrude","SWEPT_EDGE",EDGE,{"disambiguationData":[OSD([sQuery(id+"F0.wireOp",EDGE,"E483"),sQuery(id+"F0.wireOp",EDGE,"E484")])]});
            var Q15;
            Q15=makeQuery(id+"F1.opExtrude","SWEPT_EDGE",EDGE,{"disambiguationData":[OSD([sQuery(id+"F0.wireOp",EDGE,"E482"),sQuery(id+"F0.wireOp",EDGE,"E483")])]});
            var Q16;
            Q16=makeQuery(id+"F1.opExtrude","SWEPT_EDGE",EDGE,{"disambiguationData":[OSD([sQuery(id+"F0.wireOp",EDGE,"E143"),sQuery(id+"F0.wireOp",EDGE,"E144")])]});
            var Q17;
            Q17=makeQuery(id+"F1.opExtrude","SWEPT_EDGE",EDGE,{"disambiguationData":[OSD([sQuery(id+"F0.wireOp",EDGE,"E142"),sQuery(id+"F0.wireOp",EDGE,"E143")])]});
            var Q18;
            Q18=makeQuery(id+"F1.opExtrude","SWEPT_EDGE",EDGE,{"disambiguationData":[OSD([sQuery(id+"F0.wireOp",EDGE,"E141"),sQuery(id+"F0.wireOp",EDGE,"E142")])]});
            var Q19;
            Q19=makeQuery(id+"F1.opExtrude","SWEPT_EDGE",EDGE,{"disambiguationData":[OSD([sQuery(id+"F0.wireOp",EDGE,"E144"),sQuery(id+"F0.wireOp",EDGE,"E145")])]});
            var Q20;
            Q20=makeQuery(id+"F1.opExtrude","SWEPT_EDGE",EDGE,{"disambiguationData":[OSD([sQuery(id+"F0.wireOp",EDGE,"E145"),sQuery(id+"F0.wireOp",EDGE,"E146")])]});
            var Q21;
            Q21=makeQuery(id+"F1.opExtrude","SWEPT_EDGE",EDGE,{"disambiguationData":[OSD([sQuery(id+"F0.wireOp",EDGE,"E140"),sQuery(id+"F0.wireOp",EDGE,"E141")])]});
            var Q22;
            Q22=makeQuery(id+"F1.opExtrude","SWEPT_EDGE",EDGE,{"disambiguationData":[OSD([sQuery(id+"F0.wireOp",EDGE,"E138"),sQuery(id+"F0.wireOp",EDGE,"E148")])]});
            var Q23;
            Q23=makeQuery(id+"F1.opExtrude","SWEPT_EDGE",EDGE,{"disambiguationData":[OSD([sQuery(id+"F0.wireOp",EDGE,"E146"),sQuery(id+"F0.wireOp",EDGE,"E147")])]});
            var Q24;
            Q24=makeQuery(id+"F1.opExtrude","SWEPT_EDGE",EDGE,{"disambiguationData":[OSD([sQuery(id+"F0.wireOp",EDGE,"E147"),sQuery(id+"F0.wireOp",EDGE,"E148")])]});
            var Q25;
            Q25=makeQuery(id+"F1.opExtrude","SWEPT_EDGE",EDGE,{"disambiguationData":[OSD([sQuery(id+"F0.wireOp",EDGE,"E111"),sQuery(id+"F0.wireOp",EDGE,"E112")])]});
            var Q26;
            Q26=makeQuery(id+"F1.opExtrude","SWEPT_EDGE",EDGE,{"disambiguationData":[OSD([sQuery(id+"F0.wireOp",EDGE,"E101"),sQuery(id+"F0.wireOp",EDGE,"E112")])]});
            var Q27;
            Q27=makeQuery(id+"F1.opExtrude","SWEPT_EDGE",EDGE,{"disambiguationData":[OSD([sQuery(id+"F0.wireOp",EDGE,"E110"),sQuery(id+"F0.wireOp",EDGE,"E111")])]});
            var Q28;
            Q28=makeQuery(id+"F1.opExtrude","SWEPT_EDGE",EDGE,{"disambiguationData":[OSD([sQuery(id+"F0.wireOp",EDGE,"E109"),sQuery(id+"F0.wireOp",EDGE,"E110")])]});
            var Q29;
            Q29=makeQuery(id+"F1.opExtrude","SWEPT_EDGE",EDGE,{"disambiguationData":[OSD([sQuery(id+"F0.wireOp",EDGE,"E108"),sQuery(id+"F0.wireOp",EDGE,"E109")])]});
            var Q30;
            Q30=makeQuery(id+"F1.opExtrude","SWEPT_EDGE",EDGE,{"disambiguationData":[OSD([sQuery(id+"F0.wireOp",EDGE,"E101"),sQuery(id+"F0.wireOp",EDGE,"E102")])]});
            var Q31;
            Q31=makeQuery(id+"F1.opExtrude","SWEPT_EDGE",EDGE,{"disambiguationData":[OSD([sQuery(id+"F0.wireOp",EDGE,"E102"),sQuery(id+"F0.wireOp",EDGE,"E103")])]});
            var Q32;
            Q32=makeQuery(id+"F1.opExtrude","SWEPT_EDGE",EDGE,{"disambiguationData":[OSD([sQuery(id+"F0.wireOp",EDGE,"E103"),sQuery(id+"F0.wireOp",EDGE,"E104")])]});
            var Q33;
            Q33=makeQuery(id+"F1.opExtrude","SWEPT_EDGE",EDGE,{"disambiguationData":[OSD([sQuery(id+"F0.wireOp",EDGE,"E104"),sQuery(id+"F0.wireOp",EDGE,"E105")])]});
            var Q34;
            Q34=makeQuery(id+"F1.opExtrude","SWEPT_EDGE",EDGE,{"disambiguationData":[OSD([sQuery(id+"F0.wireOp",EDGE,"E105"),sQuery(id+"F0.wireOp",EDGE,"E106")])]});
            var Q35;
            Q35=makeQuery(id+"F1.opExtrude","SWEPT_EDGE",EDGE,{"disambiguationData":[OSD([sQuery(id+"F0.wireOp",EDGE,"E106"),sQuery(id+"F0.wireOp",EDGE,"E107")])]});
            var Q36;
            Q36=makeQuery(id+"F1.opExtrude","SWEPT_EDGE",EDGE,{"disambiguationData":[OSD([sQuery(id+"F0.wireOp",EDGE,"E107"),sQuery(id+"F0.wireOp",EDGE,"E108")])]});
            var Q37;
            Q37=makeQuery(id+"F1.opExtrude","SWEPT_EDGE",EDGE,{"disambiguationData":[OSD([sQuery(id+"F0.wireOp",EDGE,"E77"),sQuery(id+"F0.wireOp",EDGE,"E78")])]});
            var Q38;
            Q38=makeQuery(id+"F1.opExtrude","SWEPT_EDGE",EDGE,{"disambiguationData":[OSD([sQuery(id+"F0.wireOp",EDGE,"E70"),sQuery(id+"F0.wireOp",EDGE,"E78")])]});
            var Q39;
            Q39=makeQuery(id+"F1.opExtrude","SWEPT_EDGE",EDGE,{"disambiguationData":[OSD([sQuery(id+"F0.wireOp",EDGE,"E74"),sQuery(id+"F0.wireOp",EDGE,"E75")])]});
            var Q40;
            Q40=makeQuery(id+"F1.opExtrude","SWEPT_EDGE",EDGE,{"disambiguationData":[OSD([sQuery(id+"F0.wireOp",EDGE,"E73"),sQuery(id+"F0.wireOp",EDGE,"E74")])]});
            var Q41;
            Q41=makeQuery(id+"F1.opExtrude","SWEPT_EDGE",EDGE,{"disambiguationData":[OSD([sQuery(id+"F0.wireOp",EDGE,"E72"),sQuery(id+"F0.wireOp",EDGE,"E73")])]});
            var Q42;
            Q42=makeQuery(id+"F1.opExtrude","SWEPT_EDGE",EDGE,{"disambiguationData":[OSD([sQuery(id+"F0.wireOp",EDGE,"E8"),sQuery(id+"F0.wireOp",EDGE,"E9")])]});
            var Q43;
            Q43=makeQuery(id+"F1.opExtrude","SWEPT_EDGE",EDGE,{"disambiguationData":[OSD([sQuery(id+"F0.wireOp",EDGE,"E3"),sQuery(id+"F0.wireOp",EDGE,"E4")])]});
            var Q44;
            Q44=makeQuery(id+"F1.opExtrude","SWEPT_EDGE",EDGE,{"disambiguationData":[OSD([sQuery(id+"F0.wireOp",EDGE,"E2"),sQuery(id+"F0.wireOp",EDGE,"E3")])]});
            var Q45;
            Q45=makeQuery(id+"F1.opExtrude","SWEPT_EDGE",EDGE,{"disambiguationData":[OSD([sQuery(id+"F0.wireOp",EDGE,"E4"),sQuery(id+"F0.wireOp",EDGE,"E5")])]});
            var Q46;
            Q46=makeQuery(id+"F1.opExtrude","SWEPT_EDGE",EDGE,{"disambiguationData":[OSD([sQuery(id+"F0.wireOp",EDGE,"E0"),sQuery(id+"F0.wireOp",EDGE,"E5")])]});
            var Q47;
            Q47=makeQuery(id+"F1.opExtrude","SWEPT_EDGE",EDGE,{"disambiguationData":[OSD([sQuery(id+"F0.wireOp",EDGE,"E475"),sQuery(id+"F0.wireOp",EDGE,"E476")])]});
            var Q48;
            Q48=makeQuery(id+"F1.opExtrude","SWEPT_EDGE",EDGE,{"disambiguationData":[OSD([sQuery(id+"F0.wireOp",EDGE,"E476"),sQuery(id+"F0.wireOp",EDGE,"E477")])]});
            var Q49;
            Q49=makeQuery(id+"F1.opExtrude","SWEPT_EDGE",EDGE,{"disambiguationData":[OSD([sQuery(id+"F0.wireOp",EDGE,"E477"),sQuery(id+"F0.wireOp",EDGE,"E478")])]});
            var Q50;
            Q50=makeQuery(id+"F1.opExtrude","SWEPT_EDGE",EDGE,{"disambiguationData":[OSD([sQuery(id+"F0.wireOp",EDGE,"E478"),sQuery(id+"F0.wireOp",EDGE,"E479")])]});
            var Q51;
            Q51=makeQuery(id+"F1.opExtrude","SWEPT_EDGE",EDGE,{"disambiguationData":[OSD([sQuery(id+"F0.wireOp",EDGE,"E479"),sQuery(id+"F0.wireOp",EDGE,"E480")])]});
            var Q52;
            Q52=makeQuery(id+"F1.opExtrude","SWEPT_EDGE",EDGE,{"disambiguationData":[OSD([sQuery(id+"F0.wireOp",EDGE,"E474"),sQuery(id+"F0.wireOp",EDGE,"E480")])]});
            var Q53;
            Q53=makeQuery(id+"F1.opExtrude","SWEPT_EDGE",EDGE,{"disambiguationData":[OSD([sQuery(id+"F0.wireOp",EDGE,"E474"),sQuery(id+"F0.wireOp",EDGE,"E475")])]});
            var Q54;
            Q54=makeQuery(id+"F1.opExtrude","SWEPT_EDGE",EDGE,{"disambiguationData":[OSD([sQuery(id+"F0.wireOp",EDGE,"E1"),sQuery(id+"F0.wireOp",EDGE,"E2")])]});
            var Q55;
            Q55=makeQuery(id+"F1.opExtrude","SWEPT_EDGE",EDGE,{"disambiguationData":[OSD([sQuery(id+"F0.wireOp",EDGE,"E0"),sQuery(id+"F0.wireOp",EDGE,"E1")])]});
            var Q56;
            Q56=makeQuery(id+"F1.opExtrude","SWEPT_EDGE",EDGE,{"disambiguationData":[OSD([sQuery(id+"F0.wireOp",EDGE,"E506"),sQuery(id+"F0.wireOp",EDGE,"E507")])]});
            var Q57;
            Q57=makeQuery(id+"F1.opExtrude","SWEPT_EDGE",EDGE,{"disambiguationData":[OSD([sQuery(id+"F0.wireOp",EDGE,"E505"),sQuery(id+"F0.wireOp",EDGE,"E506")])]});
            var Q58;
            Q58=makeQuery(id+"F1.opExtrude","SWEPT_EDGE",EDGE,{"disambiguationData":[OSD([sQuery(id+"F0.wireOp",EDGE,"E505"),sQuery(id+"F0.wireOp",EDGE,"E511")])]});
            var Q59;
            Q59=makeQuery(id+"F1.opExtrude","SWEPT_EDGE",EDGE,{"disambiguationData":[OSD([sQuery(id+"F0.wireOp",EDGE,"E510"),sQuery(id+"F0.wireOp",EDGE,"E511")])]});
            var Q60;
            Q60=makeQuery(id+"F1.opExtrude","SWEPT_EDGE",EDGE,{"disambiguationData":[OSD([sQuery(id+"F0.wireOp",EDGE,"E509"),sQuery(id+"F0.wireOp",EDGE,"E510")])]});
            var Q61;
            Q61=makeQuery(id+"F1.opExtrude","SWEPT_EDGE",EDGE,{"disambiguationData":[OSD([sQuery(id+"F0.wireOp",EDGE,"E508"),sQuery(id+"F0.wireOp",EDGE,"E509")])]});
            var Q62;
            Q62=makeQuery(id+"F1.opExtrude","SWEPT_EDGE",EDGE,{"disambiguationData":[OSD([sQuery(id+"F0.wireOp",EDGE,"E507"),sQuery(id+"F0.wireOp",EDGE,"E508")])]});
            var Q63;
            Q63=makeQuery(id+"F1.opExtrude","SWEPT_EDGE",EDGE,{"disambiguationData":[OSD([sQuery(id+"F0.wireOp",EDGE,"E10"),sQuery(id+"F0.wireOp",EDGE,"E11")])]});
            var Q64;
            Q64=makeQuery(id+"F1.opExtrude","SWEPT_EDGE",EDGE,{"disambiguationData":[OSD([sQuery(id+"F0.wireOp",EDGE,"E9"),sQuery(id+"F0.wireOp",EDGE,"E10")])]});
            var Q65;
            Q65=makeQuery(id+"F1.opExtrude","SWEPT_EDGE",EDGE,{"disambiguationData":[OSD([sQuery(id+"F0.wireOp",EDGE,"E11"),sQuery(id+"F0.wireOp",EDGE,"E12")])]});
            var Q66;
            Q66=makeQuery(id+"F1.opExtrude","SWEPT_EDGE",EDGE,{"disambiguationData":[OSD([sQuery(id+"F0.wireOp",EDGE,"E13"),sQuery(id+"F0.wireOp",EDGE,"E14")])]});
            var Q67;
            Q67=makeQuery(id+"F1.opExtrude","SWEPT_EDGE",EDGE,{"disambiguationData":[OSD([sQuery(id+"F0.wireOp",EDGE,"E12"),sQuery(id+"F0.wireOp",EDGE,"E13")])]});
            var Q68;
            Q68=makeQuery(id+"F1.opExtrude","SWEPT_EDGE",EDGE,{"disambiguationData":[OSD([sQuery(id+"F0.wireOp",EDGE,"E14"),sQuery(id+"F0.wireOp",EDGE,"E15")])]});
            var Q69;
            Q69=makeQuery(id+"F1.opExtrude","SWEPT_EDGE",EDGE,{"disambiguationData":[OSD([sQuery(id+"F0.wireOp",EDGE,"E15"),sQuery(id+"F0.wireOp",EDGE,"E16")])]});
            var Q70;
            Q70=makeQuery(id+"F1.opExtrude","SWEPT_EDGE",EDGE,{"disambiguationData":[OSD([sQuery(id+"F0.wireOp",EDGE,"E6"),sQuery(id+"F0.wireOp",EDGE,"E16")])]});
            var Q71;
            Q71=makeQuery(id+"F1.opExtrude","SWEPT_EDGE",EDGE,{"disambiguationData":[OSD([sQuery(id+"F0.wireOp",EDGE,"E6"),sQuery(id+"F0.wireOp",EDGE,"E7")])]});
            var Q72;
            Q72=makeQuery(id+"F1.opExtrude","SWEPT_EDGE",EDGE,{"disambiguationData":[OSD([sQuery(id+"F0.wireOp",EDGE,"E7"),sQuery(id+"F0.wireOp",EDGE,"E8")])]});
            var Q73;
            Q73=makeQuery(id+"F1.opExtrude","SWEPT_EDGE",EDGE,{"disambiguationData":[OSD([sQuery(id+"F0.wireOp",EDGE,"E18"),sQuery(id+"F0.wireOp",EDGE,"E19")])]});
            var Q74;
            Q74=makeQuery(id+"F1.opExtrude","SWEPT_EDGE",EDGE,{"disambiguationData":[OSD([sQuery(id+"F0.wireOp",EDGE,"E17"),sQuery(id+"F0.wireOp",EDGE,"E18")])]});
            var Q75;
            Q75=makeQuery(id+"F1.opExtrude","SWEPT_EDGE",EDGE,{"disambiguationData":[OSD([sQuery(id+"F0.wireOp",EDGE,"E17"),sQuery(id+"F0.wireOp",EDGE,"E21")])]});
            var Q76;
            Q76=makeQuery(id+"F1.opExtrude","SWEPT_EDGE",EDGE,{"disambiguationData":[OSD([sQuery(id+"F0.wireOp",EDGE,"E20"),sQuery(id+"F0.wireOp",EDGE,"E21")])]});
            var Q77;
            Q77=makeQuery(id+"F1.opExtrude","SWEPT_EDGE",EDGE,{"disambiguationData":[OSD([sQuery(id+"F0.wireOp",EDGE,"E22"),sQuery(id+"F0.wireOp",EDGE,"E23")])]});
            var Q78;
            Q78=makeQuery(id+"F1.opExtrude","SWEPT_EDGE",EDGE,{"disambiguationData":[OSD([sQuery(id+"F0.wireOp",EDGE,"E23"),sQuery(id+"F0.wireOp",EDGE,"E24")])]});
            var Q79;
            Q79=makeQuery(id+"F1.opExtrude","SWEPT_EDGE",EDGE,{"disambiguationData":[OSD([sQuery(id+"F0.wireOp",EDGE,"E24"),sQuery(id+"F0.wireOp",EDGE,"E25")])]});
            var Q80;
            Q80=makeQuery(id+"F1.opExtrude","SWEPT_EDGE",EDGE,{"disambiguationData":[OSD([sQuery(id+"F0.wireOp",EDGE,"E25"),sQuery(id+"F0.wireOp",EDGE,"E26")])]});
            var Q81;
            Q81=makeQuery(id+"F1.opExtrude","SWEPT_EDGE",EDGE,{"disambiguationData":[OSD([sQuery(id+"F0.wireOp",EDGE,"E26"),sQuery(id+"F0.wireOp",EDGE,"E27")])]});
            var Q82;
            Q82=makeQuery(id+"F1.opExtrude","SWEPT_EDGE",EDGE,{"disambiguationData":[OSD([sQuery(id+"F0.wireOp",EDGE,"E22"),sQuery(id+"F0.wireOp",EDGE,"E28")])]});
            var Q83;
            Q83=makeQuery(id+"F1.opExtrude","SWEPT_EDGE",EDGE,{"disambiguationData":[OSD([sQuery(id+"F0.wireOp",EDGE,"E27"),sQuery(id+"F0.wireOp",EDGE,"E28")])]});
            var Q84;
            Q84=makeQuery(id+"F1.opExtrude","SWEPT_EDGE",EDGE,{"disambiguationData":[OSD([sQuery(id+"F0.wireOp",EDGE,"E29"),sQuery(id+"F0.wireOp",EDGE,"E37")])]});
            var Q85;
            Q85=makeQuery(id+"F1.opExtrude","SWEPT_EDGE",EDGE,{"disambiguationData":[OSD([sQuery(id+"F0.wireOp",EDGE,"E29"),sQuery(id+"F0.wireOp",EDGE,"E30")])]});
            var Q86;
            Q86=makeQuery(id+"F1.opExtrude","SWEPT_EDGE",EDGE,{"disambiguationData":[OSD([sQuery(id+"F0.wireOp",EDGE,"E30"),sQuery(id+"F0.wireOp",EDGE,"E31")])]});
            var Q87;
            Q87=makeQuery(id+"F1.opExtrude","SWEPT_EDGE",EDGE,{"disambiguationData":[OSD([sQuery(id+"F0.wireOp",EDGE,"E31"),sQuery(id+"F0.wireOp",EDGE,"E32")])]});
            var Q88;
            Q88=makeQuery(id+"F1.opExtrude","SWEPT_EDGE",EDGE,{"disambiguationData":[OSD([sQuery(id+"F0.wireOp",EDGE,"E32"),sQuery(id+"F0.wireOp",EDGE,"E33")])]});
            var Q89;
            Q89=makeQuery(id+"F1.opExtrude","SWEPT_EDGE",EDGE,{"disambiguationData":[OSD([sQuery(id+"F0.wireOp",EDGE,"E33"),sQuery(id+"F0.wireOp",EDGE,"E34")])]});
            var Q90;
            Q90=makeQuery(id+"F1.opExtrude","SWEPT_EDGE",EDGE,{"disambiguationData":[OSD([sQuery(id+"F0.wireOp",EDGE,"E34"),sQuery(id+"F0.wireOp",EDGE,"E35")])]});
            var Q91;
            Q91=makeQuery(id+"F1.opExtrude","SWEPT_EDGE",EDGE,{"disambiguationData":[OSD([sQuery(id+"F0.wireOp",EDGE,"E35"),sQuery(id+"F0.wireOp",EDGE,"E36")])]});
            var Q92;
            Q92=makeQuery(id+"F1.opExtrude","SWEPT_EDGE",EDGE,{"disambiguationData":[OSD([sQuery(id+"F0.wireOp",EDGE,"E465"),sQuery(id+"F0.wireOp",EDGE,"E466")])]});
            var Q93;
            Q93=makeQuery(id+"F1.opExtrude","SWEPT_EDGE",EDGE,{"disambiguationData":[OSD([sQuery(id+"F0.wireOp",EDGE,"E465"),sQuery(id+"F0.wireOp",EDGE,"E473")])]});
            var Q94;
            Q94=makeQuery(id+"F1.opExtrude","SWEPT_EDGE",EDGE,{"disambiguationData":[OSD([sQuery(id+"F0.wireOp",EDGE,"E472"),sQuery(id+"F0.wireOp",EDGE,"E473")])]});
            var Q95;
            Q95=makeQuery(id+"F1.opExtrude","SWEPT_EDGE",EDGE,{"disambiguationData":[OSD([sQuery(id+"F0.wireOp",EDGE,"E470"),sQuery(id+"F0.wireOp",EDGE,"E471")])]});
            var Q96;
            Q96=makeQuery(id+"F1.opExtrude","SWEPT_EDGE",EDGE,{"disambiguationData":[OSD([sQuery(id+"F0.wireOp",EDGE,"E471"),sQuery(id+"F0.wireOp",EDGE,"E472")])]});
            var Q97;
            Q97=makeQuery(id+"F1.opExtrude","SWEPT_EDGE",EDGE,{"disambiguationData":[OSD([sQuery(id+"F0.wireOp",EDGE,"E466"),sQuery(id+"F0.wireOp",EDGE,"E467")])]});
            var Q98;
            Q98=makeQuery(id+"F1.opExtrude","SWEPT_EDGE",EDGE,{"disambiguationData":[OSD([sQuery(id+"F0.wireOp",EDGE,"E467"),sQuery(id+"F0.wireOp",EDGE,"E468")])]});
            var Q99;
            Q99=makeQuery(id+"F1.opExtrude","SWEPT_EDGE",EDGE,{"disambiguationData":[OSD([sQuery(id+"F0.wireOp",EDGE,"E468"),sQuery(id+"F0.wireOp",EDGE,"E469")])]});
            var Q100;
            Q100=makeQuery(id+"F1.opExtrude","SWEPT_EDGE",EDGE,{"disambiguationData":[OSD([sQuery(id+"F0.wireOp",EDGE,"E469"),sQuery(id+"F0.wireOp",EDGE,"E470")])]});
            var Q101;
            Q101=makeQuery(id+"F1.opExtrude","SWEPT_EDGE",EDGE,{"disambiguationData":[OSD([sQuery(id+"F0.wireOp",EDGE,"E457"),sQuery(id+"F0.wireOp",EDGE,"E458")])]});
            var Q102;
            Q102=makeQuery(id+"F1.opExtrude","SWEPT_EDGE",EDGE,{"disambiguationData":[OSD([sQuery(id+"F0.wireOp",EDGE,"E38"),sQuery(id+"F0.wireOp",EDGE,"E39")])]});
            var Q103;
            Q103=makeQuery(id+"F1.opExtrude","SWEPT_EDGE",EDGE,{"disambiguationData":[OSD([sQuery(id+"F0.wireOp",EDGE,"E38"),sQuery(id+"F0.wireOp",EDGE,"E45")])]});
            var Q104;
            Q104=makeQuery(id+"F1.opExtrude","SWEPT_EDGE",EDGE,{"disambiguationData":[OSD([sQuery(id+"F0.wireOp",EDGE,"E451"),sQuery(id+"F0.wireOp",EDGE,"E452")])]});
            var Q105;
            Q105=makeQuery(id+"F1.opExtrude","SWEPT_EDGE",EDGE,{"disambiguationData":[OSD([sQuery(id+"F0.wireOp",EDGE,"E460"),sQuery(id+"F0.wireOp",EDGE,"E461")])]});
            var Q106;
            Q106=makeQuery(id+"F1.opExtrude","SWEPT_EDGE",EDGE,{"disambiguationData":[OSD([sQuery(id+"F0.wireOp",EDGE,"E462"),sQuery(id+"F0.wireOp",EDGE,"E463")])]});
            var Q107;
            Q107=makeQuery(id+"F1.opExtrude","SWEPT_EDGE",EDGE,{"disambiguationData":[OSD([sQuery(id+"F0.wireOp",EDGE,"E463"),sQuery(id+"F0.wireOp",EDGE,"E464")])]});
            var Q108;
            Q108=makeQuery(id+"F1.opExtrude","SWEPT_EDGE",EDGE,{"disambiguationData":[OSD([sQuery(id+"F0.wireOp",EDGE,"E457"),sQuery(id+"F0.wireOp",EDGE,"E464")])]});
            var Q109;
            Q109=makeQuery(id+"F1.opExtrude","SWEPT_EDGE",EDGE,{"disambiguationData":[OSD([sQuery(id+"F0.wireOp",EDGE,"E39"),sQuery(id+"F0.wireOp",EDGE,"E40")])]});
            var Q110;
            Q110=makeQuery(id+"F1.opExtrude","SWEPT_EDGE",EDGE,{"disambiguationData":[OSD([sQuery(id+"F0.wireOp",EDGE,"E40"),sQuery(id+"F0.wireOp",EDGE,"E41")])]});
            var Q111;
            Q111=makeQuery(id+"F1.opExtrude","SWEPT_EDGE",EDGE,{"disambiguationData":[OSD([sQuery(id+"F0.wireOp",EDGE,"E450"),sQuery(id+"F0.wireOp",EDGE,"E451")])]});
            var Q112;
            Q112=makeQuery(id+"F1.opExtrude","SWEPT_EDGE",EDGE,{"disambiguationData":[OSD([sQuery(id+"F0.wireOp",EDGE,"E44"),sQuery(id+"F0.wireOp",EDGE,"E45")])]});
            var Q113;
            Q113=makeQuery(id+"F1.opExtrude","SWEPT_EDGE",EDGE,{"disambiguationData":[OSD([sQuery(id+"F0.wireOp",EDGE,"E43"),sQuery(id+"F0.wireOp",EDGE,"E44")])]});
            var Q114;
            Q114=makeQuery(id+"F1.opExtrude","SWEPT_EDGE",EDGE,{"disambiguationData":[OSD([sQuery(id+"F0.wireOp",EDGE,"E42"),sQuery(id+"F0.wireOp",EDGE,"E43")])]});
            var Q115;
            Q115=makeQuery(id+"F1.opExtrude","SWEPT_EDGE",EDGE,{"disambiguationData":[OSD([sQuery(id+"F0.wireOp",EDGE,"E41"),sQuery(id+"F0.wireOp",EDGE,"E42")])]});
            var Q116;
            Q116=makeQuery(id+"F1.opExtrude","SWEPT_EDGE",EDGE,{"disambiguationData":[OSD([sQuery(id+"F0.wireOp",EDGE,"E449"),sQuery(id+"F0.wireOp",EDGE,"E456")])]});
            var Q117;
            Q117=makeQuery(id+"F1.opExtrude","SWEPT_EDGE",EDGE,{"disambiguationData":[OSD([sQuery(id+"F0.wireOp",EDGE,"E449"),sQuery(id+"F0.wireOp",EDGE,"E450")])]});
            var Q118;
            Q118=makeQuery(id+"F1.opExtrude","SWEPT_EDGE",EDGE,{"disambiguationData":[OSD([sQuery(id+"F0.wireOp",EDGE,"E455"),sQuery(id+"F0.wireOp",EDGE,"E456")])]});
            var Q119;
            Q119=makeQuery(id+"F1.opExtrude","SWEPT_EDGE",EDGE,{"disambiguationData":[OSD([sQuery(id+"F0.wireOp",EDGE,"E453"),sQuery(id+"F0.wireOp",EDGE,"E454")])]});
            var Q120;
            Q120=makeQuery(id+"F1.opExtrude","SWEPT_EDGE",EDGE,{"disambiguationData":[OSD([sQuery(id+"F0.wireOp",EDGE,"E452"),sQuery(id+"F0.wireOp",EDGE,"E453")])]});
            var Q121;
            Q121=makeQuery(id+"F1.opExtrude","SWEPT_EDGE",EDGE,{"disambiguationData":[OSD([sQuery(id+"F0.wireOp",EDGE,"E445"),sQuery(id+"F0.wireOp",EDGE,"E446")])]});
            var Q122;
            Q122=makeQuery(id+"F1.opExtrude","SWEPT_EDGE",EDGE,{"disambiguationData":[OSD([sQuery(id+"F0.wireOp",EDGE,"E444"),sQuery(id+"F0.wireOp",EDGE,"E445")])]});
            var Q123;
            Q123=makeQuery(id+"F1.opExtrude","SWEPT_EDGE",EDGE,{"disambiguationData":[OSD([sQuery(id+"F0.wireOp",EDGE,"E443"),sQuery(id+"F0.wireOp",EDGE,"E444")])]});
            var Q124;
            Q124=makeQuery(id+"F1.opExtrude","SWEPT_EDGE",EDGE,{"disambiguationData":[OSD([sQuery(id+"F0.wireOp",EDGE,"E443"),sQuery(id+"F0.wireOp",EDGE,"E448")])]});
            var Q125;
            Q125=makeQuery(id+"F1.opExtrude","SWEPT_EDGE",EDGE,{"disambiguationData":[OSD([sQuery(id+"F0.wireOp",EDGE,"E211"),sQuery(id+"F0.wireOp",EDGE,"E212")])]});
            var Q126;
            Q126=makeQuery(id+"F1.opExtrude","SWEPT_EDGE",EDGE,{"disambiguationData":[OSD([sQuery(id+"F0.wireOp",EDGE,"E210"),sQuery(id+"F0.wireOp",EDGE,"E211")])]});
            var Q127;
            Q127=makeQuery(id+"F1.opExtrude","SWEPT_EDGE",EDGE,{"disambiguationData":[OSD([sQuery(id+"F0.wireOp",EDGE,"E208"),sQuery(id+"F0.wireOp",EDGE,"E213")])]});
            var Q128;
            Q128=makeQuery(id+"F1.opExtrude","SWEPT_EDGE",EDGE,{"disambiguationData":[OSD([sQuery(id+"F0.wireOp",EDGE,"E212"),sQuery(id+"F0.wireOp",EDGE,"E213")])]});
            var Q129;
            Q129=makeQuery(id+"F1.opExtrude","SWEPT_EDGE",EDGE,{"disambiguationData":[OSD([sQuery(id+"F0.wireOp",EDGE,"E209"),sQuery(id+"F0.wireOp",EDGE,"E210")])]});
            var Q130;
            Q130=makeQuery(id+"F1.opExtrude","SWEPT_EDGE",EDGE,{"disambiguationData":[OSD([sQuery(id+"F0.wireOp",EDGE,"E447"),sQuery(id+"F0.wireOp",EDGE,"E448")])]});
            var Q131;
            Q131=makeQuery(id+"F1.opExtrude","SWEPT_EDGE",EDGE,{"disambiguationData":[OSD([sQuery(id+"F0.wireOp",EDGE,"E446"),sQuery(id+"F0.wireOp",EDGE,"E447")])]});
            var Q132;
            Q132=makeQuery(id+"F1.opExtrude","SWEPT_EDGE",EDGE,{"disambiguationData":[OSD([sQuery(id+"F0.wireOp",EDGE,"E438"),sQuery(id+"F0.wireOp",EDGE,"E439")])]});
            var Q133;
            Q133=makeQuery(id+"F1.opExtrude","SWEPT_EDGE",EDGE,{"disambiguationData":[OSD([sQuery(id+"F0.wireOp",EDGE,"E439"),sQuery(id+"F0.wireOp",EDGE,"E440")])]});
            var Q134;
            Q134=makeQuery(id+"F1.opExtrude","SWEPT_EDGE",EDGE,{"disambiguationData":[OSD([sQuery(id+"F0.wireOp",EDGE,"E440"),sQuery(id+"F0.wireOp",EDGE,"E441")])]});
            var Q135;
            Q135=makeQuery(id+"F1.opExtrude","SWEPT_EDGE",EDGE,{"disambiguationData":[OSD([sQuery(id+"F0.wireOp",EDGE,"E441"),sQuery(id+"F0.wireOp",EDGE,"E442")])]});
            var Q136;
            Q136=makeQuery(id+"F1.opExtrude","SWEPT_EDGE",EDGE,{"disambiguationData":[OSD([sQuery(id+"F0.wireOp",EDGE,"E434"),sQuery(id+"F0.wireOp",EDGE,"E435")])]});
            var Q137;
            Q137=makeQuery(id+"F1.opExtrude","SWEPT_EDGE",EDGE,{"disambiguationData":[OSD([sQuery(id+"F0.wireOp",EDGE,"E436"),sQuery(id+"F0.wireOp",EDGE,"E437")])]});
            var Q138;
            Q138=makeQuery(id+"F1.opExtrude","SWEPT_EDGE",EDGE,{"disambiguationData":[OSD([sQuery(id+"F0.wireOp",EDGE,"E89"),sQuery(id+"F0.wireOp",EDGE,"E90")])]});
            var Q139;
            Q139=makeQuery(id+"F1.opExtrude","SWEPT_EDGE",EDGE,{"disambiguationData":[OSD([sQuery(id+"F0.wireOp",EDGE,"E91"),sQuery(id+"F0.wireOp",EDGE,"E92")])]});
            var Q140;
            Q140=makeQuery(id+"F1.opExtrude","SWEPT_EDGE",EDGE,{"disambiguationData":[OSD([sQuery(id+"F0.wireOp",EDGE,"E92"),sQuery(id+"F0.wireOp",EDGE,"E93")])]});
            var Q141;
            Q141=makeQuery(id+"F1.opExtrude","SWEPT_EDGE",EDGE,{"disambiguationData":[OSD([sQuery(id+"F0.wireOp",EDGE,"E95"),sQuery(id+"F0.wireOp",EDGE,"E96")])]});
            var Q142;
            Q142=makeQuery(id+"F1.opExtrude","SWEPT_EDGE",EDGE,{"disambiguationData":[OSD([sQuery(id+"F0.wireOp",EDGE,"E94"),sQuery(id+"F0.wireOp",EDGE,"E95")])]});
            var Q143;
            Q143=makeQuery(id+"F1.opExtrude","SWEPT_EDGE",EDGE,{"disambiguationData":[OSD([sQuery(id+"F0.wireOp",EDGE,"E88"),sQuery(id+"F0.wireOp",EDGE,"E100")])]});
            var Q144;
            Q144=makeQuery(id+"F1.opExtrude","SWEPT_EDGE",EDGE,{"disambiguationData":[OSD([sQuery(id+"F0.wireOp",EDGE,"E99"),sQuery(id+"F0.wireOp",EDGE,"E100")])]});
            var Q145;
            Q145=makeQuery(id+"F1.opExtrude","SWEPT_EDGE",EDGE,{"disambiguationData":[OSD([sQuery(id+"F0.wireOp",EDGE,"E98"),sQuery(id+"F0.wireOp",EDGE,"E99")])]});
            var Q146;
            Q146=makeQuery(id+"F1.opExtrude","SWEPT_EDGE",EDGE,{"disambiguationData":[OSD([sQuery(id+"F0.wireOp",EDGE,"E96"),sQuery(id+"F0.wireOp",EDGE,"E97")])]});
            var Q147;
            Q147=makeQuery(id+"F1.opExtrude","SWEPT_EDGE",EDGE,{"disambiguationData":[OSD([sQuery(id+"F0.wireOp",EDGE,"E131"),sQuery(id+"F0.wireOp",EDGE,"E132")])]});
            var Q148;
            Q148=makeQuery(id+"F1.opExtrude","SWEPT_EDGE",EDGE,{"disambiguationData":[OSD([sQuery(id+"F0.wireOp",EDGE,"E60"),sQuery(id+"F0.wireOp",EDGE,"E61")])]});
            var Q149;
            Q149=makeQuery(id+"F1.opExtrude","SWEPT_EDGE",EDGE,{"disambiguationData":[OSD([sQuery(id+"F0.wireOp",EDGE,"E63"),sQuery(id+"F0.wireOp",EDGE,"E64")])]});
            var Q150;
            Q150=makeQuery(id+"F1.opExtrude","SWEPT_EDGE",EDGE,{"disambiguationData":[OSD([sQuery(id+"F0.wireOp",EDGE,"E62"),sQuery(id+"F0.wireOp",EDGE,"E63")])]});
            var Q151;
            Q151=makeQuery(id+"F1.opExtrude","SWEPT_EDGE",EDGE,{"disambiguationData":[OSD([sQuery(id+"F0.wireOp",EDGE,"E66"),sQuery(id+"F0.wireOp",EDGE,"E67")])]});
            var Q152;
            Q152=makeQuery(id+"F1.opExtrude","SWEPT_EDGE",EDGE,{"disambiguationData":[OSD([sQuery(id+"F0.wireOp",EDGE,"E67"),sQuery(id+"F0.wireOp",EDGE,"E68")])]});
            var Q153;
            Q153=makeQuery(id+"F1.opExtrude","SWEPT_EDGE",EDGE,{"disambiguationData":[OSD([sQuery(id+"F0.wireOp",EDGE,"E49"),sQuery(id+"F0.wireOp",EDGE,"E50")])]});
            var Q154;
            Q154=makeQuery(id+"F1.opExtrude","SWEPT_EDGE",EDGE,{"disambiguationData":[OSD([sQuery(id+"F0.wireOp",EDGE,"E51"),sQuery(id+"F0.wireOp",EDGE,"E52")])]});
            var Q155;
            Q155=makeQuery(id+"F1.opExtrude","SWEPT_EDGE",EDGE,{"disambiguationData":[OSD([sQuery(id+"F0.wireOp",EDGE,"E52"),sQuery(id+"F0.wireOp",EDGE,"E53")])]});
            var Q156;
            Q156=makeQuery(id+"F1.opExtrude","SWEPT_EDGE",EDGE,{"disambiguationData":[OSD([sQuery(id+"F0.wireOp",EDGE,"E53"),sQuery(id+"F0.wireOp",EDGE,"E54")])]});
            var Q157;
            Q157=makeQuery(id+"F1.opExtrude","SWEPT_EDGE",EDGE,{"disambiguationData":[OSD([sQuery(id+"F0.wireOp",EDGE,"E50"),sQuery(id+"F0.wireOp",EDGE,"E51")])]});
            var Q158;
            Q158=makeQuery(id+"F1.opExtrude","SWEPT_EDGE",EDGE,{"disambiguationData":[OSD([sQuery(id+"F0.wireOp",EDGE,"E48"),sQuery(id+"F0.wireOp",EDGE,"E49")])]});
            var Q159;
            Q159=makeQuery(id+"F1.opExtrude","SWEPT_EDGE",EDGE,{"disambiguationData":[OSD([sQuery(id+"F0.wireOp",EDGE,"E47"),sQuery(id+"F0.wireOp",EDGE,"E48")])]});
            var Q160;
            Q160=makeQuery(id+"F1.opExtrude","SWEPT_EDGE",EDGE,{"disambiguationData":[OSD([sQuery(id+"F0.wireOp",EDGE,"E46"),sQuery(id+"F0.wireOp",EDGE,"E47")])]});
            var Q161;
            Q161=makeQuery(id+"F1.opExtrude","SWEPT_EDGE",EDGE,{"disambiguationData":[OSD([sQuery(id+"F0.wireOp",EDGE,"E46"),sQuery(id+"F0.wireOp",EDGE,"E56")])]});
            var Q162;
            Q162=makeQuery(id+"F1.opExtrude","SWEPT_EDGE",EDGE,{"disambiguationData":[OSD([sQuery(id+"F0.wireOp",EDGE,"E55"),sQuery(id+"F0.wireOp",EDGE,"E56")])]});
            var Q163;
            Q163=makeQuery(id+"F1.opExtrude","SWEPT_EDGE",EDGE,{"disambiguationData":[OSD([sQuery(id+"F0.wireOp",EDGE,"E54"),sQuery(id+"F0.wireOp",EDGE,"E55")])]});
            var Q164;
            Q164=makeQuery(id+"F1.opExtrude","SWEPT_EDGE",EDGE,{"disambiguationData":[OSD([sQuery(id+"F0.wireOp",EDGE,"E214"),sQuery(id+"F0.wireOp",EDGE,"E215")])]});
            var Q165;
            Q165=makeQuery(id+"F1.opExtrude","SWEPT_EDGE",EDGE,{"disambiguationData":[OSD([sQuery(id+"F0.wireOp",EDGE,"E215"),sQuery(id+"F0.wireOp",EDGE,"E216")])]});
            var Q166;
            Q166=makeQuery(id+"F1.opExtrude","SWEPT_EDGE",EDGE,{"disambiguationData":[OSD([sQuery(id+"F0.wireOp",EDGE,"E81"),sQuery(id+"F0.wireOp",EDGE,"E82")])]});
            var Q167;
            Q167=makeQuery(id+"F1.opExtrude","SWEPT_EDGE",EDGE,{"disambiguationData":[OSD([sQuery(id+"F0.wireOp",EDGE,"E82"),sQuery(id+"F0.wireOp",EDGE,"E83")])]});
            var Q168;
            Q168=makeQuery(id+"F1.opExtrude","SWEPT_EDGE",EDGE,{"disambiguationData":[OSD([sQuery(id+"F0.wireOp",EDGE,"E83"),sQuery(id+"F0.wireOp",EDGE,"E84")])]});
            var Q169;
            Q169=makeQuery(id+"F1.opExtrude","SWEPT_EDGE",EDGE,{"disambiguationData":[OSD([sQuery(id+"F0.wireOp",EDGE,"E217"),sQuery(id+"F0.wireOp",EDGE,"E218")])]});
            var Q170;
            Q170=makeQuery(id+"F1.opExtrude","SWEPT_EDGE",EDGE,{"disambiguationData":[OSD([sQuery(id+"F0.wireOp",EDGE,"E79"),sQuery(id+"F0.wireOp",EDGE,"E80")])]});
            var Q171;
            Q171=makeQuery(id+"F1.opExtrude","SWEPT_EDGE",EDGE,{"disambiguationData":[OSD([sQuery(id+"F0.wireOp",EDGE,"E79"),sQuery(id+"F0.wireOp",EDGE,"E87")])]});
            var Q172;
            Q172=makeQuery(id+"F1.opExtrude","SWEPT_EDGE",EDGE,{"disambiguationData":[OSD([sQuery(id+"F0.wireOp",EDGE,"E86"),sQuery(id+"F0.wireOp",EDGE,"E87")])]});
            var Q173;
            Q173=makeQuery(id+"F1.opExtrude","SWEPT_EDGE",EDGE,{"disambiguationData":[OSD([sQuery(id+"F0.wireOp",EDGE,"E85"),sQuery(id+"F0.wireOp",EDGE,"E86")])]});
            var Q174;
            Q174=makeQuery(id+"F1.opExtrude","SWEPT_EDGE",EDGE,{"disambiguationData":[OSD([sQuery(id+"F0.wireOp",EDGE,"E84"),sQuery(id+"F0.wireOp",EDGE,"E85")])]});
            var Q175;
            Q175=makeQuery(id+"F1.opExtrude","SWEPT_EDGE",EDGE,{"disambiguationData":[OSD([sQuery(id+"F0.wireOp",EDGE,"E59"),sQuery(id+"F0.wireOp",EDGE,"E60")])]});
            var Q176;
            Q176=makeQuery(id+"F1.opExtrude","SWEPT_EDGE",EDGE,{"disambiguationData":[OSD([sQuery(id+"F0.wireOp",EDGE,"E58"),sQuery(id+"F0.wireOp",EDGE,"E59")])]});
            var Q177;
            Q177=makeQuery(id+"F1.opExtrude","SWEPT_EDGE",EDGE,{"disambiguationData":[OSD([sQuery(id+"F0.wireOp",EDGE,"E57"),sQuery(id+"F0.wireOp",EDGE,"E58")])]});
            var Q178;
            Q178=makeQuery(id+"F1.opExtrude","SWEPT_EDGE",EDGE,{"disambiguationData":[OSD([sQuery(id+"F0.wireOp",EDGE,"E57"),sQuery(id+"F0.wireOp",EDGE,"E69")])]});
            var Q179;
            Q179=makeQuery(id+"F1.opExtrude","SWEPT_EDGE",EDGE,{"disambiguationData":[OSD([sQuery(id+"F0.wireOp",EDGE,"E199"),sQuery(id+"F0.wireOp",EDGE,"E200")])]});
            var Q180;
            Q180=makeQuery(id+"F1.opExtrude","SWEPT_EDGE",EDGE,{"disambiguationData":[OSD([sQuery(id+"F0.wireOp",EDGE,"E198"),sQuery(id+"F0.wireOp",EDGE,"E199")])]});
            var Q181;
            Q181=makeQuery(id+"F1.opExtrude","SWEPT_EDGE",EDGE,{"disambiguationData":[OSD([sQuery(id+"F0.wireOp",EDGE,"E197"),sQuery(id+"F0.wireOp",EDGE,"E198")])]});
            var Q182;
            Q182=makeQuery(id+"F1.opExtrude","SWEPT_EDGE",EDGE,{"disambiguationData":[OSD([sQuery(id+"F0.wireOp",EDGE,"E196"),sQuery(id+"F0.wireOp",EDGE,"E197")])]});
            var Q183;
            Q183=makeQuery(id+"F1.opExtrude","SWEPT_EDGE",EDGE,{"disambiguationData":[OSD([sQuery(id+"F0.wireOp",EDGE,"E220"),sQuery(id+"F0.wireOp",EDGE,"E221")])]});
            var Q184;
            Q184=makeQuery(id+"F1.opExtrude","SWEPT_EDGE",EDGE,{"disambiguationData":[OSD([sQuery(id+"F0.wireOp",EDGE,"E222"),sQuery(id+"F0.wireOp",EDGE,"E223")])]});
            var Q185;
            Q185=makeQuery(id+"F1.opExtrude","SWEPT_EDGE",EDGE,{"disambiguationData":[OSD([sQuery(id+"F0.wireOp",EDGE,"E224"),sQuery(id+"F0.wireOp",EDGE,"E225")])]});
            var Q186;
            Q186=makeQuery(id+"F1.opExtrude","SWEPT_EDGE",EDGE,{"disambiguationData":[OSD([sQuery(id+"F0.wireOp",EDGE,"E219"),sQuery(id+"F0.wireOp",EDGE,"E225")])]});
            var Q187;
            Q187=makeQuery(id+"F1.opExtrude","SWEPT_EDGE",EDGE,{"disambiguationData":[OSD([sQuery(id+"F0.wireOp",EDGE,"E286"),sQuery(id+"F0.wireOp",EDGE,"E287")])]});
            var Q188;
            Q188=makeQuery(id+"F1.opExtrude","SWEPT_EDGE",EDGE,{"disambiguationData":[OSD([sQuery(id+"F0.wireOp",EDGE,"E292"),sQuery(id+"F0.wireOp",EDGE,"E293")])]});
            var Q189;
            Q189=makeQuery(id+"F1.opExtrude","SWEPT_EDGE",EDGE,{"disambiguationData":[OSD([sQuery(id+"F0.wireOp",EDGE,"E293"),sQuery(id+"F0.wireOp",EDGE,"E294")])]});
            var Q190;
            Q190=makeQuery(id+"F1.opExtrude","SWEPT_EDGE",EDGE,{"disambiguationData":[OSD([sQuery(id+"F0.wireOp",EDGE,"E291"),sQuery(id+"F0.wireOp",EDGE,"E292")])]});
            var Q191;
            Q191=makeQuery(id+"F1.opExtrude","SWEPT_EDGE",EDGE,{"disambiguationData":[OSD([sQuery(id+"F0.wireOp",EDGE,"E288"),sQuery(id+"F0.wireOp",EDGE,"E289")])]});
            var Q192;
            Q192=makeQuery(id+"F1.opExtrude","SWEPT_EDGE",EDGE,{"disambiguationData":[OSD([sQuery(id+"F0.wireOp",EDGE,"E289"),sQuery(id+"F0.wireOp",EDGE,"E290")])]});
            var Q193;
            Q193=makeQuery(id+"F1.opExtrude","SWEPT_EDGE",EDGE,{"disambiguationData":[OSD([sQuery(id+"F0.wireOp",EDGE,"E295"),sQuery(id+"F0.wireOp",EDGE,"E304")])]});
            var Q194;
            Q194=makeQuery(id+"F1.opExtrude","SWEPT_EDGE",EDGE,{"disambiguationData":[OSD([sQuery(id+"F0.wireOp",EDGE,"E296"),sQuery(id+"F0.wireOp",EDGE,"E297")])]});
            var Q195;
            Q195=makeQuery(id+"F1.opExtrude","SWEPT_EDGE",EDGE,{"disambiguationData":[OSD([sQuery(id+"F0.wireOp",EDGE,"E302"),sQuery(id+"F0.wireOp",EDGE,"E303")])]});
            var Q196;
            Q196=makeQuery(id+"F1.opExtrude","SWEPT_EDGE",EDGE,{"disambiguationData":[OSD([sQuery(id+"F0.wireOp",EDGE,"E193"),sQuery(id+"F0.wireOp",EDGE,"E207")])]});
            var Q197;
            Q197=makeQuery(id+"F1.opExtrude","SWEPT_EDGE",EDGE,{"disambiguationData":[OSD([sQuery(id+"F0.wireOp",EDGE,"E193"),sQuery(id+"F0.wireOp",EDGE,"E194")])]});
            var Q198;
            Q198=makeQuery(id+"F1.opExtrude","SWEPT_EDGE",EDGE,{"disambiguationData":[OSD([sQuery(id+"F0.wireOp",EDGE,"E300"),sQuery(id+"F0.wireOp",EDGE,"E301")])]});
            var Q199;
            Q199=makeQuery(id+"F1.opExtrude","SWEPT_EDGE",EDGE,{"disambiguationData":[OSD([sQuery(id+"F0.wireOp",EDGE,"E299"),sQuery(id+"F0.wireOp",EDGE,"E300")])]});
            var Q200;
            Q200=makeQuery(id+"F1.opExtrude","SWEPT_EDGE",EDGE,{"disambiguationData":[OSD([sQuery(id+"F0.wireOp",EDGE,"E298"),sQuery(id+"F0.wireOp",EDGE,"E299")])]});
            var Q201;
            Q201=makeQuery(id+"F1.opExtrude","SWEPT_EDGE",EDGE,{"disambiguationData":[OSD([sQuery(id+"F0.wireOp",EDGE,"E297"),sQuery(id+"F0.wireOp",EDGE,"E298")])]});
            var Q202;
            Q202=makeQuery(id+"F1.opExtrude","SWEPT_EDGE",EDGE,{"disambiguationData":[OSD([sQuery(id+"F0.wireOp",EDGE,"E187"),sQuery(id+"F0.wireOp",EDGE,"E188")])]});
            var Q203;
            Q203=makeQuery(id+"F1.opExtrude","SWEPT_EDGE",EDGE,{"disambiguationData":[OSD([sQuery(id+"F0.wireOp",EDGE,"E189"),sQuery(id+"F0.wireOp",EDGE,"E190")])]});
            var Q204;
            Q204=makeQuery(id+"F1.opExtrude","SWEPT_EDGE",EDGE,{"disambiguationData":[OSD([sQuery(id+"F0.wireOp",EDGE,"E190"),sQuery(id+"F0.wireOp",EDGE,"E191")])]});
            var Q205;
            Q205=makeQuery(id+"F1.opExtrude","SWEPT_EDGE",EDGE,{"disambiguationData":[OSD([sQuery(id+"F0.wireOp",EDGE,"E191"),sQuery(id+"F0.wireOp",EDGE,"E192")])]});
            var Q206;
            Q206=makeQuery(id+"F1.opExtrude","SWEPT_EDGE",EDGE,{"disambiguationData":[OSD([sQuery(id+"F0.wireOp",EDGE,"E185"),sQuery(id+"F0.wireOp",EDGE,"E192")])]});
            var Q207;
            Q207=makeQuery(id+"F1.opExtrude","SWEPT_EDGE",EDGE,{"disambiguationData":[OSD([sQuery(id+"F0.wireOp",EDGE,"E203"),sQuery(id+"F0.wireOp",EDGE,"E204")])]});
            var Q208;
            Q208=makeQuery(id+"F1.opExtrude","SWEPT_EDGE",EDGE,{"disambiguationData":[OSD([sQuery(id+"F0.wireOp",EDGE,"E204"),sQuery(id+"F0.wireOp",EDGE,"E205")])]});
            var Q209;
            Q209=makeQuery(id+"F1.opExtrude","SWEPT_EDGE",EDGE,{"disambiguationData":[OSD([sQuery(id+"F0.wireOp",EDGE,"E206"),sQuery(id+"F0.wireOp",EDGE,"E207")])]});
            var Q210;
            Q210=makeQuery(id+"F1.opExtrude","SWEPT_EDGE",EDGE,{"disambiguationData":[OSD([sQuery(id+"F0.wireOp",EDGE,"E205"),sQuery(id+"F0.wireOp",EDGE,"E206")])]});
            var Q211;
            Q211=makeQuery(id+"F1.opExtrude","SWEPT_EDGE",EDGE,{"disambiguationData":[OSD([sQuery(id+"F0.wireOp",EDGE,"E185"),sQuery(id+"F0.wireOp",EDGE,"E186")])]});
            var Q212;
            Q212=makeQuery(id+"F1.opExtrude","SWEPT_EDGE",EDGE,{"disambiguationData":[OSD([sQuery(id+"F0.wireOp",EDGE,"E186"),sQuery(id+"F0.wireOp",EDGE,"E187")])]});
            var Q213;
            Q213=makeQuery(id+"F1.opExtrude","SWEPT_EDGE",EDGE,{"disambiguationData":[OSD([sQuery(id+"F0.wireOp",EDGE,"E303"),sQuery(id+"F0.wireOp",EDGE,"E304")])]});
            var Q214;
            Q214=makeQuery(id+"F1.opExtrude","SWEPT_EDGE",EDGE,{"disambiguationData":[OSD([sQuery(id+"F0.wireOp",EDGE,"E318"),sQuery(id+"F0.wireOp",EDGE,"E319")])]});
            var Q215;
            Q215=makeQuery(id+"F1.opExtrude","SWEPT_EDGE",EDGE,{"disambiguationData":[OSD([sQuery(id+"F0.wireOp",EDGE,"E319"),sQuery(id+"F0.wireOp",EDGE,"E320")])]});
            var Q216;
            Q216=makeQuery(id+"F1.opExtrude","SWEPT_EDGE",EDGE,{"disambiguationData":[OSD([sQuery(id+"F0.wireOp",EDGE,"E317"),sQuery(id+"F0.wireOp",EDGE,"E318")])]});
            var Q217;
            Q217=makeQuery(id+"F1.opExtrude","SWEPT_EDGE",EDGE,{"disambiguationData":[OSD([sQuery(id+"F0.wireOp",EDGE,"E315"),sQuery(id+"F0.wireOp",EDGE,"E316")])]});
            var Q218;
            Q218=makeQuery(id+"F1.opExtrude","SWEPT_EDGE",EDGE,{"disambiguationData":[OSD([sQuery(id+"F0.wireOp",EDGE,"E314"),sQuery(id+"F0.wireOp",EDGE,"E315")])]});
            var Q219;
            Q219=makeQuery(id+"F1.opExtrude","SWEPT_EDGE",EDGE,{"disambiguationData":[OSD([sQuery(id+"F0.wireOp",EDGE,"E323"),sQuery(id+"F0.wireOp",EDGE,"E324")])]});
            var Q220;
            Q220=makeQuery(id+"F1.opExtrude","SWEPT_EDGE",EDGE,{"disambiguationData":[OSD([sQuery(id+"F0.wireOp",EDGE,"E322"),sQuery(id+"F0.wireOp",EDGE,"E323")])]});
            var Q221;
            Q221=makeQuery(id+"F1.opExtrude","SWEPT_EDGE",EDGE,{"disambiguationData":[OSD([sQuery(id+"F0.wireOp",EDGE,"E320"),sQuery(id+"F0.wireOp",EDGE,"E321")])]});
            var Q222;
            Q222=makeQuery(id+"F1.opExtrude","SWEPT_EDGE",EDGE,{"disambiguationData":[OSD([sQuery(id+"F0.wireOp",EDGE,"E310"),sQuery(id+"F0.wireOp",EDGE,"E311")])]});
            var Q223;
            Q223=makeQuery(id+"F1.opExtrude","SWEPT_EDGE",EDGE,{"disambiguationData":[OSD([sQuery(id+"F0.wireOp",EDGE,"E311"),sQuery(id+"F0.wireOp",EDGE,"E312")])]});
            var Q224;
            Q224=makeQuery(id+"F1.opExtrude","SWEPT_EDGE",EDGE,{"disambiguationData":[OSD([sQuery(id+"F0.wireOp",EDGE,"E312"),sQuery(id+"F0.wireOp",EDGE,"E313")])]});
            var Q225;
            Q225=makeQuery(id+"F1.opExtrude","SWEPT_EDGE",EDGE,{"disambiguationData":[OSD([sQuery(id+"F0.wireOp",EDGE,"E305"),sQuery(id+"F0.wireOp",EDGE,"E313")])]});
            var Q226;
            Q226=makeQuery(id+"F1.opExtrude","SWEPT_EDGE",EDGE,{"disambiguationData":[OSD([sQuery(id+"F0.wireOp",EDGE,"E305"),sQuery(id+"F0.wireOp",EDGE,"E306")])]});
            var Q227;
            Q227=makeQuery(id+"F1.opExtrude","SWEPT_EDGE",EDGE,{"disambiguationData":[OSD([sQuery(id+"F0.wireOp",EDGE,"E281"),sQuery(id+"F0.wireOp",EDGE,"E282")])]});
            var Q228;
            Q228=makeQuery(id+"F1.opExtrude","SWEPT_EDGE",EDGE,{"disambiguationData":[OSD([sQuery(id+"F0.wireOp",EDGE,"E282"),sQuery(id+"F0.wireOp",EDGE,"E283")])]});
            var Q229;
            Q229=makeQuery(id+"F1.opExtrude","SWEPT_EDGE",EDGE,{"disambiguationData":[OSD([sQuery(id+"F0.wireOp",EDGE,"E283"),sQuery(id+"F0.wireOp",EDGE,"E284")])]});
            var Q230;
            Q230=makeQuery(id+"F1.opExtrude","SWEPT_EDGE",EDGE,{"disambiguationData":[OSD([sQuery(id+"F0.wireOp",EDGE,"E278"),sQuery(id+"F0.wireOp",EDGE,"E284")])]});
            var Q231;
            Q231=makeQuery(id+"F1.opExtrude","SWEPT_EDGE",EDGE,{"disambiguationData":[OSD([sQuery(id+"F0.wireOp",EDGE,"E278"),sQuery(id+"F0.wireOp",EDGE,"E279")])]});
            var Q232;
            Q232=makeQuery(id+"F1.opExtrude","SWEPT_EDGE",EDGE,{"disambiguationData":[OSD([sQuery(id+"F0.wireOp",EDGE,"E280"),sQuery(id+"F0.wireOp",EDGE,"E281")])]});
            var Q233;
            Q233=makeQuery(id+"F1.opExtrude","SWEPT_EDGE",EDGE,{"disambiguationData":[OSD([sQuery(id+"F0.wireOp",EDGE,"E269"),sQuery(id+"F0.wireOp",EDGE,"E270")])]});
            var Q234;
            Q234=makeQuery(id+"F1.opExtrude","SWEPT_EDGE",EDGE,{"disambiguationData":[OSD([sQuery(id+"F0.wireOp",EDGE,"E270"),sQuery(id+"F0.wireOp",EDGE,"E271")])]});
            var Q235;
            Q235=makeQuery(id+"F1.opExtrude","SWEPT_EDGE",EDGE,{"disambiguationData":[OSD([sQuery(id+"F0.wireOp",EDGE,"E269"),sQuery(id+"F0.wireOp",EDGE,"E277")])]});
            var Q236;
            Q236=makeQuery(id+"F1.opExtrude","SWEPT_EDGE",EDGE,{"disambiguationData":[OSD([sQuery(id+"F0.wireOp",EDGE,"E382"),sQuery(id+"F0.wireOp",EDGE,"E383")])]});
            var Q237;
            Q237=makeQuery(id+"F1.opExtrude","SWEPT_EDGE",EDGE,{"disambiguationData":[OSD([sQuery(id+"F0.wireOp",EDGE,"E382"),sQuery(id+"F0.wireOp",EDGE,"E386")])]});
            var Q238;
            Q238=makeQuery(id+"F1.opExtrude","SWEPT_EDGE",EDGE,{"disambiguationData":[OSD([sQuery(id+"F0.wireOp",EDGE,"E385"),sQuery(id+"F0.wireOp",EDGE,"E386")])]});
            var Q239;
            Q239=makeQuery(id+"F1.opExtrude","SWEPT_EDGE",EDGE,{"disambiguationData":[OSD([sQuery(id+"F0.wireOp",EDGE,"E372"),sQuery(id+"F0.wireOp",EDGE,"E381")])]});
            var Q240;
            Q240=makeQuery(id+"F1.opExtrude","SWEPT_EDGE",EDGE,{"disambiguationData":[OSD([sQuery(id+"F0.wireOp",EDGE,"E392"),sQuery(id+"F0.wireOp",EDGE,"E393")])]});
            var Q241;
            Q241=makeQuery(id+"F1.opExtrude","SWEPT_EDGE",EDGE,{"disambiguationData":[OSD([sQuery(id+"F0.wireOp",EDGE,"E393"),sQuery(id+"F0.wireOp",EDGE,"E394")])]});
            var Q242;
            Q242=makeQuery(id+"F1.opExtrude","SWEPT_EDGE",EDGE,{"disambiguationData":[OSD([sQuery(id+"F0.wireOp",EDGE,"E399"),sQuery(id+"F0.wireOp",EDGE,"E400")])]});
            var Q243;
            Q243=makeQuery(id+"F1.opExtrude","SWEPT_EDGE",EDGE,{"disambiguationData":[OSD([sQuery(id+"F0.wireOp",EDGE,"E398"),sQuery(id+"F0.wireOp",EDGE,"E399")])]});
            var Q244;
            Q244=makeQuery(id+"F1.opExtrude","SWEPT_EDGE",EDGE,{"disambiguationData":[OSD([sQuery(id+"F0.wireOp",EDGE,"E400"),sQuery(id+"F0.wireOp",EDGE,"E401")])]});
            var Q245;
            Q245=makeQuery(id+"F1.opExtrude","SWEPT_EDGE",EDGE,{"disambiguationData":[OSD([sQuery(id+"F0.wireOp",EDGE,"E401"),sQuery(id+"F0.wireOp",EDGE,"E402")])]});
            var Q246;
            Q246=makeQuery(id+"F1.opExtrude","SWEPT_EDGE",EDGE,{"disambiguationData":[OSD([sQuery(id+"F0.wireOp",EDGE,"E408"),sQuery(id+"F0.wireOp",EDGE,"E409")])]});
            var Q247;
            Q247=makeQuery(id+"F1.opExtrude","SWEPT_EDGE",EDGE,{"disambiguationData":[OSD([sQuery(id+"F0.wireOp",EDGE,"E407"),sQuery(id+"F0.wireOp",EDGE,"E408")])]});
            var Q248;
            Q248=makeQuery(id+"F1.opExtrude","SWEPT_EDGE",EDGE,{"disambiguationData":[OSD([sQuery(id+"F0.wireOp",EDGE,"E405"),sQuery(id+"F0.wireOp",EDGE,"E414")])]});
            var Q249;
            Q249=makeQuery(id+"F1.opExtrude","SWEPT_EDGE",EDGE,{"disambiguationData":[OSD([sQuery(id+"F0.wireOp",EDGE,"E512"),sQuery(id+"F0.wireOp",EDGE,"E519")])]});
            var Q250;
            Q250=makeQuery(id+"F1.opExtrude","SWEPT_EDGE",EDGE,{"disambiguationData":[OSD([sQuery(id+"F0.wireOp",EDGE,"E518"),sQuery(id+"F0.wireOp",EDGE,"E519")])]});
            var Q251;
            Q251=makeQuery(id+"F1.opExtrude","SWEPT_EDGE",EDGE,{"disambiguationData":[OSD([sQuery(id+"F0.wireOp",EDGE,"E512"),sQuery(id+"F0.wireOp",EDGE,"E513")])]});
            var Q252;
            Q252=makeQuery(id+"F1.opExtrude","SWEPT_EDGE",EDGE,{"disambiguationData":[OSD([sQuery(id+"F0.wireOp",EDGE,"E373"),sQuery(id+"F0.wireOp",EDGE,"E374")])]});
            var Q253;
            Q253=makeQuery(id+"F1.opExtrude","SWEPT_EDGE",EDGE,{"disambiguationData":[OSD([sQuery(id+"F0.wireOp",EDGE,"E273"),sQuery(id+"F0.wireOp",EDGE,"E274")])]});
            var Q254;
            Q254=makeQuery(id+"F1.opExtrude","SWEPT_EDGE",EDGE,{"disambiguationData":[OSD([sQuery(id+"F0.wireOp",EDGE,"E271"),sQuery(id+"F0.wireOp",EDGE,"E272")])]});
            var Q255;
            Q255=makeQuery(id+"F1.opExtrude","SWEPT_EDGE",EDGE,{"disambiguationData":[OSD([sQuery(id+"F0.wireOp",EDGE,"E363"),sQuery(id+"F0.wireOp",EDGE,"E364")])]});
            var Q256;
            Q256=makeQuery(id+"F1.opExtrude","SWEPT_EDGE",EDGE,{"disambiguationData":[OSD([sQuery(id+"F0.wireOp",EDGE,"E266"),sQuery(id+"F0.wireOp",EDGE,"E267")])]});
            var Q257;
            Q257=makeQuery(id+"F1.opExtrude","SWEPT_EDGE",EDGE,{"disambiguationData":[OSD([sQuery(id+"F0.wireOp",EDGE,"E265"),sQuery(id+"F0.wireOp",EDGE,"E266")])]});
            var Q258;
            Q258=makeQuery(id+"F1.opExtrude","SWEPT_EDGE",EDGE,{"disambiguationData":[OSD([sQuery(id+"F0.wireOp",EDGE,"E257"),sQuery(id+"F0.wireOp",EDGE,"E268")])]});
            var Q259;
            Q259=makeQuery(id+"F1.opExtrude","SWEPT_EDGE",EDGE,{"disambiguationData":[OSD([sQuery(id+"F0.wireOp",EDGE,"E257"),sQuery(id+"F0.wireOp",EDGE,"E258")])]});
            var Q260;
            Q260=makeQuery(id+"F1.opExtrude","SWEPT_EDGE",EDGE,{"disambiguationData":[OSD([sQuery(id+"F0.wireOp",EDGE,"E178"),sQuery(id+"F0.wireOp",EDGE,"E179")])]});
            var Q261;
            Q261=makeQuery(id+"F1.opExtrude","SWEPT_EDGE",EDGE,{"disambiguationData":[OSD([sQuery(id+"F0.wireOp",EDGE,"E239"),sQuery(id+"F0.wireOp",EDGE,"E256")])]});
            var Q262;
            Q262=makeQuery(id+"F1.opExtrude","SWEPT_EDGE",EDGE,{"disambiguationData":[OSD([sQuery(id+"F0.wireOp",EDGE,"E239"),sQuery(id+"F0.wireOp",EDGE,"E240")])]});
            var Q263;
            Q263=makeQuery(id+"F1.opExtrude","SWEPT_EDGE",EDGE,{"disambiguationData":[OSD([sQuery(id+"F0.wireOp",EDGE,"E255"),sQuery(id+"F0.wireOp",EDGE,"E256")])]});
            var Q264;
            Q264=makeQuery(id+"F1.opExtrude","SWEPT_EDGE",EDGE,{"disambiguationData":[OSD([sQuery(id+"F0.wireOp",EDGE,"E258"),sQuery(id+"F0.wireOp",EDGE,"E259")])]});
            var Q265;
            Q265=makeQuery(id+"F1.opExtrude","SWEPT_EDGE",EDGE,{"disambiguationData":[OSD([sQuery(id+"F0.wireOp",EDGE,"E517"),sQuery(id+"F0.wireOp",EDGE,"E518")])]});
            var Q266;
            Q266=makeQuery(id+"F1.opExtrude","SWEPT_EDGE",EDGE,{"disambiguationData":[OSD([sQuery(id+"F0.wireOp",EDGE,"E516"),sQuery(id+"F0.wireOp",EDGE,"E517")])]});
            var Q267;
            Q267=makeQuery(id+"F1.opExtrude","SWEPT_EDGE",EDGE,{"disambiguationData":[OSD([sQuery(id+"F0.wireOp",EDGE,"E515"),sQuery(id+"F0.wireOp",EDGE,"E516")])]});
            var Q268;
            Q268=makeQuery(id+"F1.opExtrude","SWEPT_EDGE",EDGE,{"disambiguationData":[OSD([sQuery(id+"F0.wireOp",EDGE,"E522"),sQuery(id+"F0.wireOp",EDGE,"E523")])]});
            var Q269;
            Q269=makeQuery(id+"F1.opExtrude","SWEPT_EDGE",EDGE,{"disambiguationData":[OSD([sQuery(id+"F0.wireOp",EDGE,"E514"),sQuery(id+"F0.wireOp",EDGE,"E515")])]});
            var Q270;
            Q270=makeQuery(id+"F1.opExtrude","SWEPT_EDGE",EDGE,{"disambiguationData":[OSD([sQuery(id+"F0.wireOp",EDGE,"E520"),sQuery(id+"F0.wireOp",EDGE,"E521")])]});
            var Q271;
            Q271=makeQuery(id+"F1.opExtrude","SWEPT_EDGE",EDGE,{"disambiguationData":[OSD([sQuery(id+"F0.wireOp",EDGE,"E389"),sQuery(id+"F0.wireOp",EDGE,"E390")])]});
            var Q272;
            Q272=makeQuery(id+"F1.opExtrude","SWEPT_EDGE",EDGE,{"disambiguationData":[OSD([sQuery(id+"F0.wireOp",EDGE,"E391"),sQuery(id+"F0.wireOp",EDGE,"E392")])]});
            var Q273;
            Q273=makeQuery(id+"F1.opExtrude","SWEPT_EDGE",EDGE,{"disambiguationData":[OSD([sQuery(id+"F0.wireOp",EDGE,"E520"),sQuery(id+"F0.wireOp",EDGE,"E523")])]});
            var Q274;
            Q274=makeQuery(id+"F1.opExtrude","SWEPT_EDGE",EDGE,{"disambiguationData":[OSD([sQuery(id+"F0.wireOp",EDGE,"E388"),sQuery(id+"F0.wireOp",EDGE,"E389")])]});
            var Q275;
            Q275=makeQuery(id+"F1.opExtrude","SWEPT_EDGE",EDGE,{"disambiguationData":[OSD([sQuery(id+"F0.wireOp",EDGE,"E387"),sQuery(id+"F0.wireOp",EDGE,"E396")])]});
            var Q276;
            Q276=makeQuery(id+"F1.opExtrude","SWEPT_EDGE",EDGE,{"disambiguationData":[OSD([sQuery(id+"F0.wireOp",EDGE,"E403"),sQuery(id+"F0.wireOp",EDGE,"E404")])]});
            var Q277;
            Q277=makeQuery(id+"F1.opExtrude","SWEPT_EDGE",EDGE,{"disambiguationData":[OSD([sQuery(id+"F0.wireOp",EDGE,"E397"),sQuery(id+"F0.wireOp",EDGE,"E404")])]});
            var Q278;
            Q278=makeQuery(id+"F1.opExtrude","SWEPT_EDGE",EDGE,{"disambiguationData":[OSD([sQuery(id+"F0.wireOp",EDGE,"E378"),sQuery(id+"F0.wireOp",EDGE,"E379")])]});
            var Q279;
            Q279=makeQuery(id+"F1.opExtrude","SWEPT_EDGE",EDGE,{"disambiguationData":[OSD([sQuery(id+"F0.wireOp",EDGE,"E380"),sQuery(id+"F0.wireOp",EDGE,"E381")])]});
            var Q280;
            Q280=makeQuery(id+"F1.opExtrude","SWEPT_EDGE",EDGE,{"disambiguationData":[OSD([sQuery(id+"F0.wireOp",EDGE,"E377"),sQuery(id+"F0.wireOp",EDGE,"E378")])]});
            var Q281;
            Q281=makeQuery(id+"F1.opExtrude","SWEPT_EDGE",EDGE,{"disambiguationData":[OSD([sQuery(id+"F0.wireOp",EDGE,"E376"),sQuery(id+"F0.wireOp",EDGE,"E377")])]});
            var Q282;
            Q282=makeQuery(id+"F1.opExtrude","SWEPT_EDGE",EDGE,{"disambiguationData":[OSD([sQuery(id+"F0.wireOp",EDGE,"E417"),sQuery(id+"F0.wireOp",EDGE,"E418")])]});
            var Q283;
            Q283=makeQuery(id+"F1.opExtrude","SWEPT_EDGE",EDGE,{"disambiguationData":[OSD([sQuery(id+"F0.wireOp",EDGE,"E418"),sQuery(id+"F0.wireOp",EDGE,"E419")])]});
            var Q284;
            Q284=makeQuery(id+"F1.opExtrude","SWEPT_EDGE",EDGE,{"disambiguationData":[OSD([sQuery(id+"F0.wireOp",EDGE,"E420"),sQuery(id+"F0.wireOp",EDGE,"E421")])]});
            var Q285;
            Q285=makeQuery(id+"F1.opExtrude","SWEPT_EDGE",EDGE,{"disambiguationData":[OSD([sQuery(id+"F0.wireOp",EDGE,"E415"),sQuery(id+"F0.wireOp",EDGE,"E416")])]});
            var Q286;
            Q286=makeQuery(id+"F1.opExtrude","SWEPT_EDGE",EDGE,{"disambiguationData":[OSD([sQuery(id+"F0.wireOp",EDGE,"E274"),sQuery(id+"F0.wireOp",EDGE,"E275")])]});
            var Q287;
            Q287=makeQuery(id+"F1.opExtrude","SWEPT_EDGE",EDGE,{"disambiguationData":[OSD([sQuery(id+"F0.wireOp",EDGE,"E363"),sQuery(id+"F0.wireOp",EDGE,"E371")])]});
            var Q288;
            Q288=makeQuery(id+"F1.opExtrude","SWEPT_EDGE",EDGE,{"disambiguationData":[OSD([sQuery(id+"F0.wireOp",EDGE,"E201"),sQuery(id+"F0.wireOp",EDGE,"E202")])]});
            var Q289;
            Q289=makeQuery(id+"F1.opExtrude","SWEPT_EDGE",EDGE,{"disambiguationData":[OSD([sQuery(id+"F0.wireOp",EDGE,"E200"),sQuery(id+"F0.wireOp",EDGE,"E201")])]});
            var Q290;
            Q290=makeQuery(id+"F1.opExtrude","SWEPT_EDGE",EDGE,{"disambiguationData":[OSD([sQuery(id+"F0.wireOp",EDGE,"E169"),sQuery(id+"F0.wireOp",EDGE,"E170")])]});
            var Q291;
            Q291=makeQuery(id+"F1.opExtrude","SWEPT_EDGE",EDGE,{"disambiguationData":[OSD([sQuery(id+"F0.wireOp",EDGE,"E125"),sQuery(id+"F0.wireOp",EDGE,"E137")])]});
            var Q292;
            Q292=makeQuery(id+"F1.opExtrude","SWEPT_EDGE",EDGE,{"disambiguationData":[OSD([sQuery(id+"F0.wireOp",EDGE,"E127"),sQuery(id+"F0.wireOp",EDGE,"E128")])]});
            var Q293;
            Q293=makeQuery(id+"F1.opExtrude","SWEPT_EDGE",EDGE,{"disambiguationData":[OSD([sQuery(id+"F0.wireOp",EDGE,"E128"),sQuery(id+"F0.wireOp",EDGE,"E129")])]});
            var Q294;
            Q294=makeQuery(id+"F1.opExtrude","SWEPT_EDGE",EDGE,{"disambiguationData":[OSD([sQuery(id+"F0.wireOp",EDGE,"E125"),sQuery(id+"F0.wireOp",EDGE,"E126")])]});
            var Q295;
            Q295=makeQuery(id+"F1.opExtrude","SWEPT_EDGE",EDGE,{"disambiguationData":[OSD([sQuery(id+"F0.wireOp",EDGE,"E126"),sQuery(id+"F0.wireOp",EDGE,"E127")])]});
            var Q296;
            Q296=makeQuery(id+"F1.opExtrude","SWEPT_EDGE",EDGE,{"disambiguationData":[OSD([sQuery(id+"F0.wireOp",EDGE,"E171"),sQuery(id+"F0.wireOp",EDGE,"E184")])]});
            var Q297;
            Q297=makeQuery(id+"F1.opExtrude","SWEPT_EDGE",EDGE,{"disambiguationData":[OSD([sQuery(id+"F0.wireOp",EDGE,"E171"),sQuery(id+"F0.wireOp",EDGE,"E172")])]});
            var Q298;
            Q298=makeQuery(id+"F1.opExtrude","SWEPT_EDGE",EDGE,{"disambiguationData":[OSD([sQuery(id+"F0.wireOp",EDGE,"E163"),sQuery(id+"F0.wireOp",EDGE,"E170")])]});
            var Q299;
            Q299=makeQuery(id+"F1.opExtrude","SWEPT_EDGE",EDGE,{"disambiguationData":[OSD([sQuery(id+"F0.wireOp",EDGE,"E163"),sQuery(id+"F0.wireOp",EDGE,"E164")])]});
            var Q300;
            Q300=makeQuery(id+"F1.opExtrude","SWEPT_EDGE",EDGE,{"disambiguationData":[OSD([sQuery(id+"F0.wireOp",EDGE,"E165"),sQuery(id+"F0.wireOp",EDGE,"E166")])]});
            var Q301;
            Q301=makeQuery(id+"F1.opExtrude","SWEPT_EDGE",EDGE,{"disambiguationData":[OSD([sQuery(id+"F0.wireOp",EDGE,"E166"),sQuery(id+"F0.wireOp",EDGE,"E167")])]});
            var Q302;
            Q302=makeQuery(id+"F1.opExtrude","SWEPT_EDGE",EDGE,{"disambiguationData":[OSD([sQuery(id+"F0.wireOp",EDGE,"E167"),sQuery(id+"F0.wireOp",EDGE,"E168")])]});
            var Q303;
            Q303=makeQuery(id+"F1.opExtrude","SWEPT_EDGE",EDGE,{"disambiguationData":[OSD([sQuery(id+"F0.wireOp",EDGE,"E174"),sQuery(id+"F0.wireOp",EDGE,"E175")])]});
            var Q304;
            Q304=makeQuery(id+"F1.opExtrude","SWEPT_EDGE",EDGE,{"disambiguationData":[OSD([sQuery(id+"F0.wireOp",EDGE,"E173"),sQuery(id+"F0.wireOp",EDGE,"E174")])]});
            var Q305;
            Q305=makeQuery(id+"F1.opExtrude","SWEPT_EDGE",EDGE,{"disambiguationData":[OSD([sQuery(id+"F0.wireOp",EDGE,"E172"),sQuery(id+"F0.wireOp",EDGE,"E173")])]});
            var Q306;
            Q306=makeQuery(id+"F1.opExtrude","SWEPT_EDGE",EDGE,{"disambiguationData":[OSD([sQuery(id+"F0.wireOp",EDGE,"E175"),sQuery(id+"F0.wireOp",EDGE,"E176")])]});
            var Q307;
            Q307=makeQuery(id+"F1.opExtrude","SWEPT_EDGE",EDGE,{"disambiguationData":[OSD([sQuery(id+"F0.wireOp",EDGE,"E176"),sQuery(id+"F0.wireOp",EDGE,"E177")])]});
            var Q308;
            Q308=makeQuery(id+"F1.opExtrude","SWEPT_EDGE",EDGE,{"disambiguationData":[OSD([sQuery(id+"F0.wireOp",EDGE,"E132"),sQuery(id+"F0.wireOp",EDGE,"E133")])]});
            var Q309;
            Q309=makeQuery(id+"F1.opExtrude","SWEPT_EDGE",EDGE,{"disambiguationData":[OSD([sQuery(id+"F0.wireOp",EDGE,"E133"),sQuery(id+"F0.wireOp",EDGE,"E134")])]});
            var Q310;
            Q310=makeQuery(id+"F1.opExtrude","SWEPT_EDGE",EDGE,{"disambiguationData":[OSD([sQuery(id+"F0.wireOp",EDGE,"E135"),sQuery(id+"F0.wireOp",EDGE,"E136")])]});
            var Q311;
            Q311=makeQuery(id+"F1.opExtrude","SWEPT_EDGE",EDGE,{"disambiguationData":[OSD([sQuery(id+"F0.wireOp",EDGE,"E136"),sQuery(id+"F0.wireOp",EDGE,"E137")])]});
            var Q312;
            Q312=makeQuery(id+"F1.opExtrude","SWEPT_EDGE",EDGE,{"disambiguationData":[OSD([sQuery(id+"F0.wireOp",EDGE,"E113"),sQuery(id+"F0.wireOp",EDGE,"E124")])]});
            var Q313;
            Q313=makeQuery(id+"F1.opExtrude","SWEPT_EDGE",EDGE,{"disambiguationData":[OSD([sQuery(id+"F0.wireOp",EDGE,"E123"),sQuery(id+"F0.wireOp",EDGE,"E124")])]});
            var Q314;
            Q314=makeQuery(id+"F1.opExtrude","SWEPT_EDGE",EDGE,{"disambiguationData":[OSD([sQuery(id+"F0.wireOp",EDGE,"E152"),sQuery(id+"F0.wireOp",EDGE,"E153")])]});
            var Q315;
            Q315=makeQuery(id+"F1.opExtrude","SWEPT_EDGE",EDGE,{"disambiguationData":[OSD([sQuery(id+"F0.wireOp",EDGE,"E151"),sQuery(id+"F0.wireOp",EDGE,"E152")])]});
            var Q316;
            Q316=makeQuery(id+"F1.opExtrude","SWEPT_EDGE",EDGE,{"disambiguationData":[OSD([sQuery(id+"F0.wireOp",EDGE,"E149"),sQuery(id+"F0.wireOp",EDGE,"E150")])]});
            var Q317;
            Q317=makeQuery(id+"F1.opExtrude","SWEPT_EDGE",EDGE,{"disambiguationData":[OSD([sQuery(id+"F0.wireOp",EDGE,"E149"),sQuery(id+"F0.wireOp",EDGE,"E162")])]});
            var Q318;
            Q318=makeQuery(id+"F1.opExtrude","SWEPT_EDGE",EDGE,{"disambiguationData":[OSD([sQuery(id+"F0.wireOp",EDGE,"E150"),sQuery(id+"F0.wireOp",EDGE,"E151")])]});
            var Q319;
            Q319=makeQuery(id+"F1.opExtrude","SWEPT_EDGE",EDGE,{"disambiguationData":[OSD([sQuery(id+"F0.wireOp",EDGE,"E161"),sQuery(id+"F0.wireOp",EDGE,"E162")])]});
            var Q320;
            Q320=makeQuery(id+"F1.opExtrude","SWEPT_EDGE",EDGE,{"disambiguationData":[OSD([sQuery(id+"F0.wireOp",EDGE,"E160"),sQuery(id+"F0.wireOp",EDGE,"E161")])]});
            var Q321;
            Q321=makeQuery(id+"F1.opExtrude","SWEPT_EDGE",EDGE,{"disambiguationData":[OSD([sQuery(id+"F0.wireOp",EDGE,"E159"),sQuery(id+"F0.wireOp",EDGE,"E160")])]});
            var Q322;
            Q322=makeQuery(id+"F1.opExtrude","SWEPT_EDGE",EDGE,{"disambiguationData":[OSD([sQuery(id+"F0.wireOp",EDGE,"E158"),sQuery(id+"F0.wireOp",EDGE,"E159")])]});
            var Q323;
            Q323=makeQuery(id+"F1.opExtrude","SWEPT_EDGE",EDGE,{"disambiguationData":[OSD([sQuery(id+"F0.wireOp",EDGE,"E114"),sQuery(id+"F0.wireOp",EDGE,"E115")])]});
            var Q324;
            Q324=makeQuery(id+"F1.opExtrude","SWEPT_EDGE",EDGE,{"disambiguationData":[OSD([sQuery(id+"F0.wireOp",EDGE,"E113"),sQuery(id+"F0.wireOp",EDGE,"E114")])]});
            var Q325;
            Q325=makeQuery(id+"F1.opExtrude","SWEPT_EDGE",EDGE,{"disambiguationData":[OSD([sQuery(id+"F0.wireOp",EDGE,"E230"),sQuery(id+"F0.wireOp",EDGE,"E231")])]});
            var Q326;
            Q326=makeQuery(id+"F1.opExtrude","SWEPT_EDGE",EDGE,{"disambiguationData":[OSD([sQuery(id+"F0.wireOp",EDGE,"E236"),sQuery(id+"F0.wireOp",EDGE,"E237")])]});
            var Q327;
            Q327=makeQuery(id+"F1.opExtrude","SWEPT_EDGE",EDGE,{"disambiguationData":[OSD([sQuery(id+"F0.wireOp",EDGE,"E233"),sQuery(id+"F0.wireOp",EDGE,"E234")])]});
            var Q328;
            Q328=makeQuery(id+"F1.opExtrude","SWEPT_EDGE",EDGE,{"disambiguationData":[OSD([sQuery(id+"F0.wireOp",EDGE,"E232"),sQuery(id+"F0.wireOp",EDGE,"E233")])]});
            var Q329;
            Q329=makeQuery(id+"F1.opExtrude","SWEPT_EDGE",EDGE,{"disambiguationData":[OSD([sQuery(id+"F0.wireOp",EDGE,"E231"),sQuery(id+"F0.wireOp",EDGE,"E232")])]});
            var Q330;
            Q330=makeQuery(id+"F1.opExtrude","SWEPT_EDGE",EDGE,{"disambiguationData":[OSD([sQuery(id+"F0.wireOp",EDGE,"E253"),sQuery(id+"F0.wireOp",EDGE,"E254")])]});
            var Q331;
            Q331=makeQuery(id+"F1.opExtrude","SWEPT_EDGE",EDGE,{"disambiguationData":[OSD([sQuery(id+"F0.wireOp",EDGE,"E252"),sQuery(id+"F0.wireOp",EDGE,"E253")])]});
            var Q332;
            Q332=makeQuery(id+"F1.opExtrude","SWEPT_EDGE",EDGE,{"disambiguationData":[OSD([sQuery(id+"F0.wireOp",EDGE,"E356"),sQuery(id+"F0.wireOp",EDGE,"E357")])]});
            var Q333;
            Q333=makeQuery(id+"F1.opExtrude","SWEPT_EDGE",EDGE,{"disambiguationData":[OSD([sQuery(id+"F0.wireOp",EDGE,"E355"),sQuery(id+"F0.wireOp",EDGE,"E356")])]});
            var Q334;
            Q334=makeQuery(id+"F1.opExtrude","SWEPT_EDGE",EDGE,{"disambiguationData":[OSD([sQuery(id+"F0.wireOp",EDGE,"E263"),sQuery(id+"F0.wireOp",EDGE,"E264")])]});
            var Q335;
            Q335=makeQuery(id+"F1.opExtrude","SWEPT_EDGE",EDGE,{"disambiguationData":[OSD([sQuery(id+"F0.wireOp",EDGE,"E262"),sQuery(id+"F0.wireOp",EDGE,"E263")])]});
            var Q336;
            Q336=makeQuery(id+"F1.opExtrude","SWEPT_EDGE",EDGE,{"disambiguationData":[OSD([sQuery(id+"F0.wireOp",EDGE,"E261"),sQuery(id+"F0.wireOp",EDGE,"E262")])]});
            var Q337;
            Q337=makeQuery(id+"F1.opExtrude","SWEPT_EDGE",EDGE,{"disambiguationData":[OSD([sQuery(id+"F0.wireOp",EDGE,"E259"),sQuery(id+"F0.wireOp",EDGE,"E260")])]});
            var Q338;
            Q338=makeQuery(id+"F1.opExtrude","SWEPT_EDGE",EDGE,{"disambiguationData":[OSD([sQuery(id+"F0.wireOp",EDGE,"E368"),sQuery(id+"F0.wireOp",EDGE,"E369")])]});
            var Q339;
            Q339=makeQuery(id+"F1.opExtrude","SWEPT_EDGE",EDGE,{"disambiguationData":[OSD([sQuery(id+"F0.wireOp",EDGE,"E369"),sQuery(id+"F0.wireOp",EDGE,"E370")])]});
            var Q340;
            Q340=makeQuery(id+"F1.opExtrude","SWEPT_EDGE",EDGE,{"disambiguationData":[OSD([sQuery(id+"F0.wireOp",EDGE,"E370"),sQuery(id+"F0.wireOp",EDGE,"E371")])]});
            var Q341;
            Q341=makeQuery(id+"F1.opExtrude","SWEPT_EDGE",EDGE,{"disambiguationData":[OSD([sQuery(id+"F0.wireOp",EDGE,"E367"),sQuery(id+"F0.wireOp",EDGE,"E368")])]});
            var Q342;
            Q342=makeQuery(id+"F1.opExtrude","SWEPT_EDGE",EDGE,{"disambiguationData":[OSD([sQuery(id+"F0.wireOp",EDGE,"E366"),sQuery(id+"F0.wireOp",EDGE,"E367")])]});
            var Q343;
            Q343=makeQuery(id+"F1.opExtrude","SWEPT_EDGE",EDGE,{"disambiguationData":[OSD([sQuery(id+"F0.wireOp",EDGE,"E251"),sQuery(id+"F0.wireOp",EDGE,"E252")])]});
            var Q344;
            Q344=makeQuery(id+"F1.opExtrude","SWEPT_EDGE",EDGE,{"disambiguationData":[OSD([sQuery(id+"F0.wireOp",EDGE,"E249"),sQuery(id+"F0.wireOp",EDGE,"E250")])]});
            var Q345;
            Q345=makeQuery(id+"F1.opExtrude","SWEPT_EDGE",EDGE,{"disambiguationData":[OSD([sQuery(id+"F0.wireOp",EDGE,"E248"),sQuery(id+"F0.wireOp",EDGE,"E249")])]});
            var Q346;
            Q346=makeQuery(id+"F1.opExtrude","SWEPT_EDGE",EDGE,{"disambiguationData":[OSD([sQuery(id+"F0.wireOp",EDGE,"E247"),sQuery(id+"F0.wireOp",EDGE,"E248")])]});
            var Q347;
            Q347=makeQuery(id+"F1.opExtrude","SWEPT_EDGE",EDGE,{"disambiguationData":[OSD([sQuery(id+"F0.wireOp",EDGE,"E246"),sQuery(id+"F0.wireOp",EDGE,"E247")])]});
            var Q348;
            Q348=makeQuery(id+"F1.opExtrude","SWEPT_EDGE",EDGE,{"disambiguationData":[OSD([sQuery(id+"F0.wireOp",EDGE,"E245"),sQuery(id+"F0.wireOp",EDGE,"E246")])]});
            var Q349;
            Q349=makeQuery(id+"F1.opExtrude","SWEPT_EDGE",EDGE,{"disambiguationData":[OSD([sQuery(id+"F0.wireOp",EDGE,"E244"),sQuery(id+"F0.wireOp",EDGE,"E245")])]});
            var Q350;
            Q350=makeQuery(id+"F1.opExtrude","SWEPT_EDGE",EDGE,{"disambiguationData":[OSD([sQuery(id+"F0.wireOp",EDGE,"E243"),sQuery(id+"F0.wireOp",EDGE,"E244")])]});
            var Q351;
            Q351=makeQuery(id+"F1.opExtrude","SWEPT_EDGE",EDGE,{"disambiguationData":[OSD([sQuery(id+"F0.wireOp",EDGE,"E357"),sQuery(id+"F0.wireOp",EDGE,"E358")])]});
            var Q352;
            Q352=makeQuery(id+"F1.opExtrude","SWEPT_EDGE",EDGE,{"disambiguationData":[OSD([sQuery(id+"F0.wireOp",EDGE,"E350"),sQuery(id+"F0.wireOp",EDGE,"E362")])]});
            var Q353;
            Q353=makeQuery(id+"F1.opExtrude","SWEPT_EDGE",EDGE,{"disambiguationData":[OSD([sQuery(id+"F0.wireOp",EDGE,"E361"),sQuery(id+"F0.wireOp",EDGE,"E362")])]});
            var Q354;
            Q354=makeQuery(id+"F1.opExtrude","SWEPT_EDGE",EDGE,{"disambiguationData":[OSD([sQuery(id+"F0.wireOp",EDGE,"E352"),sQuery(id+"F0.wireOp",EDGE,"E353")])]});
            var Q355;
            Q355=makeQuery(id+"F1.opExtrude","SWEPT_EDGE",EDGE,{"disambiguationData":[OSD([sQuery(id+"F0.wireOp",EDGE,"E351"),sQuery(id+"F0.wireOp",EDGE,"E352")])]});
            var Q356;
            Q356=makeQuery(id+"F1.opExtrude","SWEPT_EDGE",EDGE,{"disambiguationData":[OSD([sQuery(id+"F0.wireOp",EDGE,"E526"),sQuery(id+"F0.wireOp",EDGE,"E527")])]});
            var Q357;
            Q357=makeQuery(id+"F1.opExtrude","SWEPT_EDGE",EDGE,{"disambiguationData":[OSD([sQuery(id+"F0.wireOp",EDGE,"E527"),sQuery(id+"F0.wireOp",EDGE,"E528")])]});
            var Q358;
            Q358=makeQuery(id+"F1.opExtrude","SWEPT_EDGE",EDGE,{"disambiguationData":[OSD([sQuery(id+"F0.wireOp",EDGE,"E525"),sQuery(id+"F0.wireOp",EDGE,"E526")])]});
            var Q359;
            Q359=makeQuery(id+"F1.opExtrude","SWEPT_EDGE",EDGE,{"disambiguationData":[OSD([sQuery(id+"F0.wireOp",EDGE,"E529"),sQuery(id+"F0.wireOp",EDGE,"E530")])]});
            var Q360;
            Q360=makeQuery(id+"F1.opExtrude","SWEPT_EDGE",EDGE,{"disambiguationData":[OSD([sQuery(id+"F0.wireOp",EDGE,"E528"),sQuery(id+"F0.wireOp",EDGE,"E529")])]});
            var Q361;
            Q361=makeQuery(id+"F1.opExtrude","SWEPT_EDGE",EDGE,{"disambiguationData":[OSD([sQuery(id+"F0.wireOp",EDGE,"E524"),sQuery(id+"F0.wireOp",EDGE,"E530")])]});
            var Q362;
            Q362=makeQuery(id+"F1.opExtrude","SWEPT_EDGE",EDGE,{"disambiguationData":[OSD([sQuery(id+"F0.wireOp",EDGE,"E536"),sQuery(id+"F0.wireOp",EDGE,"E537")])]});
            var Q363;
            Q363=makeQuery(id+"F1.opExtrude","SWEPT_EDGE",EDGE,{"disambiguationData":[OSD([sQuery(id+"F0.wireOp",EDGE,"E422"),sQuery(id+"F0.wireOp",EDGE,"E433")])]});
            var Q364;
            Q364=makeQuery(id+"F1.opExtrude","SWEPT_EDGE",EDGE,{"disambiguationData":[OSD([sQuery(id+"F0.wireOp",EDGE,"E432"),sQuery(id+"F0.wireOp",EDGE,"E433")])]});
            var Q365;
            Q365=makeQuery(id+"F1.opExtrude","SWEPT_EDGE",EDGE,{"disambiguationData":[OSD([sQuery(id+"F0.wireOp",EDGE,"E424"),sQuery(id+"F0.wireOp",EDGE,"E425")])]});
            var Q366;
            Q366=makeQuery(id+"F1.opExtrude","SWEPT_EDGE",EDGE,{"disambiguationData":[OSD([sQuery(id+"F0.wireOp",EDGE,"E425"),sQuery(id+"F0.wireOp",EDGE,"E426")])]});
            var Q367;
            Q367=makeQuery(id+"F1.opExtrude","SWEPT_EDGE",EDGE,{"disambiguationData":[OSD([sQuery(id+"F0.wireOp",EDGE,"E429"),sQuery(id+"F0.wireOp",EDGE,"E430")])]});
            var Q368;
            Q368=makeQuery(id+"F1.opExtrude","SWEPT_EDGE",EDGE,{"disambiguationData":[OSD([sQuery(id+"F0.wireOp",EDGE,"E428"),sQuery(id+"F0.wireOp",EDGE,"E429")])]});
            var Q369;
            Q369=makeQuery(id+"F1.opExtrude","SWEPT_EDGE",EDGE,{"disambiguationData":[OSD([sQuery(id+"F0.wireOp",EDGE,"E427"),sQuery(id+"F0.wireOp",EDGE,"E428")])]});
            var Q370;
            Q370=makeQuery(id+"F1.opExtrude","SWEPT_EDGE",EDGE,{"disambiguationData":[OSD([sQuery(id+"F0.wireOp",EDGE,"E537"),sQuery(id+"F0.wireOp",EDGE,"E538")])]});
            var Q371;
            Q371=makeQuery(id+"F1.opExtrude","SWEPT_EDGE",EDGE,{"disambiguationData":[OSD([sQuery(id+"F0.wireOp",EDGE,"E531"),sQuery(id+"F0.wireOp",EDGE,"E538")])]});
            var Q372;
            Q372=makeQuery(id+"F1.opExtrude","SWEPT_EDGE",EDGE,{"disambiguationData":[OSD([sQuery(id+"F0.wireOp",EDGE,"E343"),sQuery(id+"F0.wireOp",EDGE,"E344")])]});
            var Q373;
            Q373=makeQuery(id+"F1.opExtrude","SWEPT_EDGE",EDGE,{"disambiguationData":[OSD([sQuery(id+"F0.wireOp",EDGE,"E342"),sQuery(id+"F0.wireOp",EDGE,"E343")])]});
            var Q374;
            Q374=makeQuery(id+"F1.opExtrude","SWEPT_EDGE",EDGE,{"disambiguationData":[OSD([sQuery(id+"F0.wireOp",EDGE,"E542"),sQuery(id+"F0.wireOp",EDGE,"E543")])]});
            var Q375;
            Q375=makeQuery(id+"F1.opExtrude","SWEPT_EDGE",EDGE,{"disambiguationData":[OSD([sQuery(id+"F0.wireOp",EDGE,"E541"),sQuery(id+"F0.wireOp",EDGE,"E542")])]});
            var Q376;
            Q376=makeQuery(id+"F1.opExtrude","SWEPT_EDGE",EDGE,{"disambiguationData":[OSD([sQuery(id+"F0.wireOp",EDGE,"E540"),sQuery(id+"F0.wireOp",EDGE,"E541")])]});
            var Q377;
            Q377=makeQuery(id+"F1.opExtrude","SWEPT_EDGE",EDGE,{"disambiguationData":[OSD([sQuery(id+"F0.wireOp",EDGE,"E534"),sQuery(id+"F0.wireOp",EDGE,"E535")])]});
            var Q378;
            Q378=makeQuery(id+"F1.opExtrude","SWEPT_EDGE",EDGE,{"disambiguationData":[OSD([sQuery(id+"F0.wireOp",EDGE,"E335"),sQuery(id+"F0.wireOp",EDGE,"E349")])]});
            var Q379;
            Q379=makeQuery(id+"F1.opExtrude","SWEPT_EDGE",EDGE,{"disambiguationData":[OSD([sQuery(id+"F0.wireOp",EDGE,"E325"),sQuery(id+"F0.wireOp",EDGE,"E334")])]});
            var Q380;
            Q380=makeQuery(id+"F1.opExtrude","SWEPT_EDGE",EDGE,{"disambiguationData":[OSD([sQuery(id+"F0.wireOp",EDGE,"E332"),sQuery(id+"F0.wireOp",EDGE,"E333")])]});
            var Q381;
            Q381=makeQuery(id+"F1.opExtrude","SWEPT_EDGE",EDGE,{"disambiguationData":[OSD([sQuery(id+"F0.wireOp",EDGE,"E531"),sQuery(id+"F0.wireOp",EDGE,"E532")])]});
            var Q382;
            Q382=makeQuery(id+"F1.opExtrude","SWEPT_EDGE",EDGE,{"disambiguationData":[OSD([sQuery(id+"F0.wireOp",EDGE,"E533"),sQuery(id+"F0.wireOp",EDGE,"E534")])]});
            var Q383;
            Q383=makeQuery(id+"F1.opExtrude","SWEPT_EDGE",EDGE,{"disambiguationData":[OSD([sQuery(id+"F0.wireOp",EDGE,"E326"),sQuery(id+"F0.wireOp",EDGE,"E327")])]});
            var Q384;
            Q384=makeQuery(id+"F1.opExtrude","SWEPT_EDGE",EDGE,{"disambiguationData":[OSD([sQuery(id+"F0.wireOp",EDGE,"E327"),sQuery(id+"F0.wireOp",EDGE,"E328")])]});
            var Q385;
            Q385=makeQuery(id+"F1.opExtrude","SWEPT_EDGE",EDGE,{"disambiguationData":[OSD([sQuery(id+"F0.wireOp",EDGE,"E226"),sQuery(id+"F0.wireOp",EDGE,"E238")])]});
            var Q386;
            Q386=makeQuery(id+"F1.opExtrude","SWEPT_EDGE",EDGE,{"disambiguationData":[OSD([sQuery(id+"F0.wireOp",EDGE,"E228"),sQuery(id+"F0.wireOp",EDGE,"E229")])]});
            var Q387;
            Q387=makeQuery(id+"F1.opExtrude","SWEPT_EDGE",EDGE,{"disambiguationData":[OSD([sQuery(id+"F0.wireOp",EDGE,"E235"),sQuery(id+"F0.wireOp",EDGE,"E236")])]});
            var Q388;
            Q388=makeQuery(id+"F1.opExtrude","SWEPT_EDGE",EDGE,{"disambiguationData":[OSD([sQuery(id+"F0.wireOp",EDGE,"E156"),sQuery(id+"F0.wireOp",EDGE,"E157")])]});
            var Q389;
            Q389=makeQuery(id+"F1.opExtrude","SWEPT_EDGE",EDGE,{"disambiguationData":[OSD([sQuery(id+"F0.wireOp",EDGE,"E328"),sQuery(id+"F0.wireOp",EDGE,"E329")])]});
            var Q390;
            Q390=makeQuery(id+"F1.opExtrude","SWEPT_EDGE",EDGE,{"disambiguationData":[OSD([sQuery(id+"F0.wireOp",EDGE,"E331"),sQuery(id+"F0.wireOp",EDGE,"E332")])]});
            var Q391;
            Q391=makeQuery(id+"F1.opExtrude","SWEPT_EDGE",EDGE,{"disambiguationData":[OSD([sQuery(id+"F0.wireOp",EDGE,"E338"),sQuery(id+"F0.wireOp",EDGE,"E339")])]});
            var Q392;
            Q392=makeQuery(id+"F1.opExtrude","SWEPT_EDGE",EDGE,{"disambiguationData":[OSD([sQuery(id+"F0.wireOp",EDGE,"E539"),sQuery(id+"F0.wireOp",EDGE,"E540")])]});
            var Q393;
            Q393=makeQuery(id+"F1.opExtrude","SWEPT_EDGE",EDGE,{"disambiguationData":[OSD([sQuery(id+"F0.wireOp",EDGE,"E335"),sQuery(id+"F0.wireOp",EDGE,"E336")])]});
            var Q394;
            Q394=makeQuery(id+"F1.opExtrude","SWEPT_EDGE",EDGE,{"disambiguationData":[OSD([sQuery(id+"F0.wireOp",EDGE,"E539"),sQuery(id+"F0.wireOp",EDGE,"E543")])]});
            var Q395;
            Q395=makeQuery(id+"F1.opExtrude","SWEPT_EDGE",EDGE,{"disambiguationData":[OSD([sQuery(id+"F0.wireOp",EDGE,"E500"),sQuery(id+"F0.wireOp",EDGE,"E501")])]});
            var Q396;
            Q396=makeQuery(id+"F1.opExtrude","SWEPT_EDGE",EDGE,{"disambiguationData":[OSD([sQuery(id+"F0.wireOp",EDGE,"E492"),sQuery(id+"F0.wireOp",EDGE,"E493")])]});
            var Q397;
            Q397=makeQuery(id+"F1.opExtrude","SWEPT_EDGE",EDGE,{"disambiguationData":[OSD([sQuery(id+"F0.wireOp",EDGE,"E491"),sQuery(id+"F0.wireOp",EDGE,"E492")])]});
            var Q398;
            Q398=makeQuery(id+"F1.opExtrude","SWEPT_EDGE",EDGE,{"disambiguationData":[OSD([sQuery(id+"F0.wireOp",EDGE,"E491"),sQuery(id+"F0.wireOp",EDGE,"E495")])]});
            var Q399;
            Q399=makeQuery(id+"F1.opExtrude","SWEPT_EDGE",EDGE,{"disambiguationData":[OSD([sQuery(id+"F0.wireOp",EDGE,"E494"),sQuery(id+"F0.wireOp",EDGE,"E495")])]});
            var Q400;
            Q400=makeQuery(id+"F1.opExtrude","SWEPT_EDGE",EDGE,{"disambiguationData":[OSD([sQuery(id+"F0.wireOp",EDGE,"E493"),sQuery(id+"F0.wireOp",EDGE,"E494")])]});
            var Q401;
            Q401=makeQuery(id+"F1.opExtrude","SWEPT_EDGE",EDGE,{"disambiguationData":[OSD([sQuery(id+"F0.wireOp",EDGE,"E461"),sQuery(id+"F0.wireOp",EDGE,"E462")])]});
            fillet(context, id + "F2", {"entities" : qUnion([Q0, Q1, Q2, Q3, Q4, Q5, Q6, Q7, Q8, Q9, Q10, Q11, Q12, Q13, Q14, Q15, Q16, Q17, Q18, Q19, Q20, Q21, Q22, Q23, Q24, Q25, Q26, Q27, Q28, Q29, Q30, Q31, Q32, Q33, Q34, Q35, Q36, Q37, Q38, Q39, Q40, Q41, Q42, Q43, Q44, Q45, Q46, Q47, Q48, Q49, Q50, Q51, Q52, Q53, Q54, Q55, Q56, Q57, Q58, Q59, Q60, Q61, Q62, Q63, Q64, Q65, Q66, Q67, Q68, Q69, Q70, Q71, Q72, Q73, Q74, Q75, Q76, Q77, Q78, Q79, Q80, Q81, Q82, Q83, Q84, Q85, Q86, Q87, Q88, Q89, Q90, Q91, Q92, Q93, Q94, Q95, Q96, Q97, Q98, Q99, Q100, Q101, Q102, Q103, Q104, Q105, Q106, Q107, Q108, Q109, Q110, Q111, Q112, Q113, Q114, Q115, Q116, Q117, Q118, Q119, Q120, Q121, Q122, Q123, Q124, Q125, Q126, Q127, Q128, Q129, Q130, Q131, Q132, Q133, Q134, Q135, Q136, Q137, Q138, Q139, Q140, Q141, Q142, Q143, Q144, Q145, Q146, Q147, Q148, Q149, Q150, Q151, Q152, Q153, Q154, Q155, Q156, Q157, Q158, Q159, Q160, Q161, Q162, Q163, Q164, Q165, Q166, Q167, Q168, Q169, Q170, Q171, Q172, Q173, Q174, Q175, Q176, Q177, Q178, Q179, Q180, Q181, Q182, Q183, Q184, Q185, Q186, Q187, Q188, Q189, Q190, Q191, Q192, Q193, Q194, Q195, Q196, Q197, Q198, Q199, Q200, Q201, Q202, Q203, Q204, Q205, Q206, Q207, Q208, Q209, Q210, Q211, Q212, Q213, Q214, Q215, Q216, Q217, Q218, Q219, Q220, Q221, Q222, Q223, Q224, Q225, Q226, Q227, Q228, Q229, Q230, Q231, Q232, Q233, Q234, Q235, Q236, Q237, Q238, Q239, Q240, Q241, Q242, Q243, Q244, Q245, Q246, Q247, Q248, Q249, Q250, Q251, Q252, Q253, Q254, Q255, Q256, Q257, Q258, Q259, Q260, Q261, Q262, Q263, Q264, Q265, Q266, Q267, Q268, Q269, Q270, Q271, Q272, Q273, Q274, Q275, Q276, Q277, Q278, Q279, Q280, Q281, Q282, Q283, Q284, Q285, Q286, Q287, Q288, Q289, Q290, Q291, Q292, Q293, Q294, Q295, Q296, Q297, Q298, Q299, Q300, Q301, Q302, Q303, Q304, Q305, Q306, Q307, Q308, Q309, Q310, Q311, Q312, Q313, Q314, Q315, Q316, Q317, Q318, Q319, Q320, Q321, Q322, Q323, Q324, Q325, Q326, Q327, Q328, Q329, Q330, Q331, Q332, Q333, Q334, Q335, Q336, Q337, Q338, Q339, Q340, Q341, Q342, Q343, Q344, Q345, Q346, Q347, Q348, Q349, Q350, Q351, Q352, Q353, Q354, Q355, Q356, Q357, Q358, Q359, Q360, Q361, Q362, Q363, Q364, Q365, Q366, Q367, Q368, Q369, Q370, Q371, Q372, Q373, Q374, Q375, Q376, Q377, Q378, Q379, Q380, Q381, Q382, Q383, Q384, Q385, Q386, Q387, Q388, Q389, Q390, Q391, Q392, Q393, Q394, Q395, Q396, Q397, Q398, Q399, Q400, Q401]), "radius" : 2 * mm, "tangentPropagation" : true, "allowEdgeOverflow" : false});
        }
        {
            var Q0;
            Q0=makeQuery(id+"F1.opExtrude","CAP_FACE",FACE,{"disambiguationData":[OSD([sQuery(id+"F0.wireOp",EDGE,"E505"),sQuery(id+"F0.wireOp",EDGE,"E506"),sQuery(id+"F0.wireOp",EDGE,"E507"),sQuery(id+"F0.wireOp",EDGE,"E508"),sQuery(id+"F0.wireOp",EDGE,"E509"),sQuery(id+"F0.wireOp",EDGE,"E510"),sQuery(id+"F0.wireOp",EDGE,"E511")])],"isStart":false});
            var Q1;
            Q1=makeQuery(id+"F1.opExtrude","CAP_FACE",FACE,{"disambiguationData":[OSD([sQuery(id+"F0.wireOp",EDGE,"E0"),sQuery(id+"F0.wireOp",EDGE,"E1"),sQuery(id+"F0.wireOp",EDGE,"E2"),sQuery(id+"F0.wireOp",EDGE,"E3"),sQuery(id+"F0.wireOp",EDGE,"E4"),sQuery(id+"F0.wireOp",EDGE,"E5")])],"isStart":false});
            var Q2;
            Q2=makeQuery(id+"F1.opExtrude","CAP_FACE",FACE,{"disambiguationData":[OSD([sQuery(id+"F0.wireOp",EDGE,"E474"),sQuery(id+"F0.wireOp",EDGE,"E475"),sQuery(id+"F0.wireOp",EDGE,"E476"),sQuery(id+"F0.wireOp",EDGE,"E477"),sQuery(id+"F0.wireOp",EDGE,"E478"),sQuery(id+"F0.wireOp",EDGE,"E479"),sQuery(id+"F0.wireOp",EDGE,"E480")])],"isStart":false});
            var Q3;
            Q3=makeQuery(id+"F1.opExtrude","CAP_FACE",FACE,{"disambiguationData":[OSD([sQuery(id+"F0.wireOp",EDGE,"E491"),sQuery(id+"F0.wireOp",EDGE,"E492"),sQuery(id+"F0.wireOp",EDGE,"E493"),sQuery(id+"F0.wireOp",EDGE,"E494"),sQuery(id+"F0.wireOp",EDGE,"E495")])],"isStart":false});
            var Q4;
            Q4=makeQuery(id+"F1.opExtrude","CAP_FACE",FACE,{"disambiguationData":[OSD([sQuery(id+"F0.wireOp",EDGE,"E101"),sQuery(id+"F0.wireOp",EDGE,"E102"),sQuery(id+"F0.wireOp",EDGE,"E103"),sQuery(id+"F0.wireOp",EDGE,"E104"),sQuery(id+"F0.wireOp",EDGE,"E105"),sQuery(id+"F0.wireOp",EDGE,"E106"),sQuery(id+"F0.wireOp",EDGE,"E107"),sQuery(id+"F0.wireOp",EDGE,"E108"),sQuery(id+"F0.wireOp",EDGE,"E109"),sQuery(id+"F0.wireOp",EDGE,"E110"),sQuery(id+"F0.wireOp",EDGE,"E111"),sQuery(id+"F0.wireOp",EDGE,"E112")])],"isStart":false});
            var Q5;
            Q5=makeQuery(id+"F1.opExtrude","CAP_FACE",FACE,{"disambiguationData":[OSD([sQuery(id+"F0.wireOp",EDGE,"E6"),sQuery(id+"F0.wireOp",EDGE,"E7"),sQuery(id+"F0.wireOp",EDGE,"E8"),sQuery(id+"F0.wireOp",EDGE,"E9"),sQuery(id+"F0.wireOp",EDGE,"E10"),sQuery(id+"F0.wireOp",EDGE,"E11"),sQuery(id+"F0.wireOp",EDGE,"E12"),sQuery(id+"F0.wireOp",EDGE,"E13"),sQuery(id+"F0.wireOp",EDGE,"E14"),sQuery(id+"F0.wireOp",EDGE,"E15"),sQuery(id+"F0.wireOp",EDGE,"E16")])],"isStart":false});
            var Q6;
            Q6=makeQuery(id+"F1.opExtrude","CAP_FACE",FACE,{"disambiguationData":[OSD([sQuery(id+"F0.wireOp",EDGE,"E88"),sQuery(id+"F0.wireOp",EDGE,"E89"),sQuery(id+"F0.wireOp",EDGE,"E90"),sQuery(id+"F0.wireOp",EDGE,"E91"),sQuery(id+"F0.wireOp",EDGE,"E92"),sQuery(id+"F0.wireOp",EDGE,"E93"),sQuery(id+"F0.wireOp",EDGE,"E94"),sQuery(id+"F0.wireOp",EDGE,"E95"),sQuery(id+"F0.wireOp",EDGE,"E96"),sQuery(id+"F0.wireOp",EDGE,"E97"),sQuery(id+"F0.wireOp",EDGE,"E98"),sQuery(id+"F0.wireOp",EDGE,"E99"),sQuery(id+"F0.wireOp",EDGE,"E100")])],"isStart":false});
            var Q7;
            Q7=makeQuery(id+"F1.opExtrude","CAP_FACE",FACE,{"disambiguationData":[OSD([sQuery(id+"F0.wireOp",EDGE,"E70"),sQuery(id+"F0.wireOp",EDGE,"E71"),sQuery(id+"F0.wireOp",EDGE,"E72"),sQuery(id+"F0.wireOp",EDGE,"E73"),sQuery(id+"F0.wireOp",EDGE,"E74"),sQuery(id+"F0.wireOp",EDGE,"E75"),sQuery(id+"F0.wireOp",EDGE,"E76"),sQuery(id+"F0.wireOp",EDGE,"E77"),sQuery(id+"F0.wireOp",EDGE,"E78")])],"isStart":false});
            var Q8;
            Q8=makeQuery(id+"F1.opExtrude","CAP_FACE",FACE,{"disambiguationData":[OSD([sQuery(id+"F0.wireOp",EDGE,"E17"),sQuery(id+"F0.wireOp",EDGE,"E18"),sQuery(id+"F0.wireOp",EDGE,"E19"),sQuery(id+"F0.wireOp",EDGE,"E20"),sQuery(id+"F0.wireOp",EDGE,"E21")])],"isStart":false});
            var Q9;
            Q9=makeQuery(id+"F1.opExtrude","CAP_FACE",FACE,{"disambiguationData":[OSD([sQuery(id+"F0.wireOp",EDGE,"E22"),sQuery(id+"F0.wireOp",EDGE,"E23"),sQuery(id+"F0.wireOp",EDGE,"E24"),sQuery(id+"F0.wireOp",EDGE,"E25"),sQuery(id+"F0.wireOp",EDGE,"E26"),sQuery(id+"F0.wireOp",EDGE,"E27"),sQuery(id+"F0.wireOp",EDGE,"E28")])],"isStart":false});
            var Q10;
            Q10=makeQuery(id+"F1.opExtrude","CAP_FACE",FACE,{"disambiguationData":[OSD([sQuery(id+"F0.wireOp",EDGE,"E46"),sQuery(id+"F0.wireOp",EDGE,"E47"),sQuery(id+"F0.wireOp",EDGE,"E48"),sQuery(id+"F0.wireOp",EDGE,"E49"),sQuery(id+"F0.wireOp",EDGE,"E50"),sQuery(id+"F0.wireOp",EDGE,"E51"),sQuery(id+"F0.wireOp",EDGE,"E52"),sQuery(id+"F0.wireOp",EDGE,"E53"),sQuery(id+"F0.wireOp",EDGE,"E54"),sQuery(id+"F0.wireOp",EDGE,"E55"),sQuery(id+"F0.wireOp",EDGE,"E56")])],"isStart":false});
            var Q11;
            Q11=makeQuery(id+"F1.opExtrude","CAP_FACE",FACE,{"disambiguationData":[OSD([sQuery(id+"F0.wireOp",EDGE,"E57"),sQuery(id+"F0.wireOp",EDGE,"E58"),sQuery(id+"F0.wireOp",EDGE,"E59"),sQuery(id+"F0.wireOp",EDGE,"E60"),sQuery(id+"F0.wireOp",EDGE,"E61"),sQuery(id+"F0.wireOp",EDGE,"E62"),sQuery(id+"F0.wireOp",EDGE,"E63"),sQuery(id+"F0.wireOp",EDGE,"E64"),sQuery(id+"F0.wireOp",EDGE,"E65"),sQuery(id+"F0.wireOp",EDGE,"E66"),sQuery(id+"F0.wireOp",EDGE,"E67"),sQuery(id+"F0.wireOp",EDGE,"E68"),sQuery(id+"F0.wireOp",EDGE,"E69")])],"isStart":false});
            var Q12;
            Q12=makeQuery(id+"F1.opExtrude","CAP_FACE",FACE,{"disambiguationData":[OSD([sQuery(id+"F0.wireOp",EDGE,"E125"),sQuery(id+"F0.wireOp",EDGE,"E126"),sQuery(id+"F0.wireOp",EDGE,"E127"),sQuery(id+"F0.wireOp",EDGE,"E128"),sQuery(id+"F0.wireOp",EDGE,"E129"),sQuery(id+"F0.wireOp",EDGE,"E130"),sQuery(id+"F0.wireOp",EDGE,"E131"),sQuery(id+"F0.wireOp",EDGE,"E132"),sQuery(id+"F0.wireOp",EDGE,"E133"),sQuery(id+"F0.wireOp",EDGE,"E134"),sQuery(id+"F0.wireOp",EDGE,"E135"),sQuery(id+"F0.wireOp",EDGE,"E136"),sQuery(id+"F0.wireOp",EDGE,"E137")])],"isStart":false});
            var Q13;
            Q13=makeQuery(id+"F1.opExtrude","CAP_FACE",FACE,{"disambiguationData":[OSD([sQuery(id+"F0.wireOp",EDGE,"E113"),sQuery(id+"F0.wireOp",EDGE,"E114"),sQuery(id+"F0.wireOp",EDGE,"E115"),sQuery(id+"F0.wireOp",EDGE,"E116"),sQuery(id+"F0.wireOp",EDGE,"E117"),sQuery(id+"F0.wireOp",EDGE,"E118"),sQuery(id+"F0.wireOp",EDGE,"E119"),sQuery(id+"F0.wireOp",EDGE,"E120"),sQuery(id+"F0.wireOp",EDGE,"E121"),sQuery(id+"F0.wireOp",EDGE,"E122"),sQuery(id+"F0.wireOp",EDGE,"E123"),sQuery(id+"F0.wireOp",EDGE,"E124")])],"isStart":false});
            var Q14;
            Q14=makeQuery(id+"F1.opExtrude","CAP_FACE",FACE,{"disambiguationData":[OSD([sQuery(id+"F0.wireOp",EDGE,"E138"),sQuery(id+"F0.wireOp",EDGE,"E139"),sQuery(id+"F0.wireOp",EDGE,"E140"),sQuery(id+"F0.wireOp",EDGE,"E141"),sQuery(id+"F0.wireOp",EDGE,"E142"),sQuery(id+"F0.wireOp",EDGE,"E143"),sQuery(id+"F0.wireOp",EDGE,"E144"),sQuery(id+"F0.wireOp",EDGE,"E145"),sQuery(id+"F0.wireOp",EDGE,"E146"),sQuery(id+"F0.wireOp",EDGE,"E147"),sQuery(id+"F0.wireOp",EDGE,"E148")])],"isStart":false});
            var Q15;
            Q15=makeQuery(id+"F1.opExtrude","CAP_FACE",FACE,{"disambiguationData":[OSD([sQuery(id+"F0.wireOp",EDGE,"E481"),sQuery(id+"F0.wireOp",EDGE,"E482"),sQuery(id+"F0.wireOp",EDGE,"E483"),sQuery(id+"F0.wireOp",EDGE,"E484"),sQuery(id+"F0.wireOp",EDGE,"E485"),sQuery(id+"F0.wireOp",EDGE,"E486"),sQuery(id+"F0.wireOp",EDGE,"E487"),sQuery(id+"F0.wireOp",EDGE,"E488"),sQuery(id+"F0.wireOp",EDGE,"E489"),sQuery(id+"F0.wireOp",EDGE,"E490")])],"isStart":false});
            var Q16;
            Q16=makeQuery(id+"F1.opExtrude","CAP_FACE",FACE,{"disambiguationData":[OSD([sQuery(id+"F0.wireOp",EDGE,"E496"),sQuery(id+"F0.wireOp",EDGE,"E497"),sQuery(id+"F0.wireOp",EDGE,"E498"),sQuery(id+"F0.wireOp",EDGE,"E499"),sQuery(id+"F0.wireOp",EDGE,"E500"),sQuery(id+"F0.wireOp",EDGE,"E501"),sQuery(id+"F0.wireOp",EDGE,"E502"),sQuery(id+"F0.wireOp",EDGE,"E503"),sQuery(id+"F0.wireOp",EDGE,"E504")])],"isStart":false});
            var Q17;
            Q17=makeQuery(id+"F1.opExtrude","CAP_FACE",FACE,{"disambiguationData":[OSD([sQuery(id+"F0.wireOp",EDGE,"E226"),sQuery(id+"F0.wireOp",EDGE,"E227"),sQuery(id+"F0.wireOp",EDGE,"E228"),sQuery(id+"F0.wireOp",EDGE,"E229"),sQuery(id+"F0.wireOp",EDGE,"E230"),sQuery(id+"F0.wireOp",EDGE,"E231"),sQuery(id+"F0.wireOp",EDGE,"E232"),sQuery(id+"F0.wireOp",EDGE,"E233"),sQuery(id+"F0.wireOp",EDGE,"E234"),sQuery(id+"F0.wireOp",EDGE,"E235"),sQuery(id+"F0.wireOp",EDGE,"E236"),sQuery(id+"F0.wireOp",EDGE,"E237"),sQuery(id+"F0.wireOp",EDGE,"E238")])],"isStart":false});
            var Q18;
            Q18=makeQuery(id+"F1.opExtrude","CAP_FACE",FACE,{"disambiguationData":[OSD([sQuery(id+"F0.wireOp",EDGE,"E149"),sQuery(id+"F0.wireOp",EDGE,"E150"),sQuery(id+"F0.wireOp",EDGE,"E151"),sQuery(id+"F0.wireOp",EDGE,"E152"),sQuery(id+"F0.wireOp",EDGE,"E153"),sQuery(id+"F0.wireOp",EDGE,"E154"),sQuery(id+"F0.wireOp",EDGE,"E155"),sQuery(id+"F0.wireOp",EDGE,"E156"),sQuery(id+"F0.wireOp",EDGE,"E157"),sQuery(id+"F0.wireOp",EDGE,"E158"),sQuery(id+"F0.wireOp",EDGE,"E159"),sQuery(id+"F0.wireOp",EDGE,"E160"),sQuery(id+"F0.wireOp",EDGE,"E161"),sQuery(id+"F0.wireOp",EDGE,"E162")])],"isStart":false});
            var Q19;
            Q19=makeQuery(id+"F1.opExtrude","CAP_FACE",FACE,{"disambiguationData":[OSD([sQuery(id+"F0.wireOp",EDGE,"E29"),sQuery(id+"F0.wireOp",EDGE,"E30"),sQuery(id+"F0.wireOp",EDGE,"E31"),sQuery(id+"F0.wireOp",EDGE,"E32"),sQuery(id+"F0.wireOp",EDGE,"E33"),sQuery(id+"F0.wireOp",EDGE,"E34"),sQuery(id+"F0.wireOp",EDGE,"E35"),sQuery(id+"F0.wireOp",EDGE,"E36"),sQuery(id+"F0.wireOp",EDGE,"E37")])],"isStart":false});
            var Q20;
            Q20=makeQuery(id+"F1.opExtrude","CAP_FACE",FACE,{"disambiguationData":[OSD([sQuery(id+"F0.wireOp",EDGE,"E38"),sQuery(id+"F0.wireOp",EDGE,"E39"),sQuery(id+"F0.wireOp",EDGE,"E40"),sQuery(id+"F0.wireOp",EDGE,"E41"),sQuery(id+"F0.wireOp",EDGE,"E42"),sQuery(id+"F0.wireOp",EDGE,"E43"),sQuery(id+"F0.wireOp",EDGE,"E44"),sQuery(id+"F0.wireOp",EDGE,"E45")])],"isStart":false});
            var Q21;
            Q21=makeQuery(id+"F1.opExtrude","CAP_FACE",FACE,{"disambiguationData":[OSD([sQuery(id+"F0.wireOp",EDGE,"E465"),sQuery(id+"F0.wireOp",EDGE,"E466"),sQuery(id+"F0.wireOp",EDGE,"E467"),sQuery(id+"F0.wireOp",EDGE,"E468"),sQuery(id+"F0.wireOp",EDGE,"E469"),sQuery(id+"F0.wireOp",EDGE,"E470"),sQuery(id+"F0.wireOp",EDGE,"E471"),sQuery(id+"F0.wireOp",EDGE,"E472"),sQuery(id+"F0.wireOp",EDGE,"E473")])],"isStart":false});
            var Q22;
            Q22=makeQuery(id+"F1.opExtrude","CAP_FACE",FACE,{"disambiguationData":[OSD([sQuery(id+"F0.wireOp",EDGE,"E457"),sQuery(id+"F0.wireOp",EDGE,"E458"),sQuery(id+"F0.wireOp",EDGE,"E459"),sQuery(id+"F0.wireOp",EDGE,"E460"),sQuery(id+"F0.wireOp",EDGE,"E461"),sQuery(id+"F0.wireOp",EDGE,"E462"),sQuery(id+"F0.wireOp",EDGE,"E463"),sQuery(id+"F0.wireOp",EDGE,"E464")])],"isStart":false});
            var Q23;
            Q23=makeQuery(id+"F1.opExtrude","CAP_FACE",FACE,{"disambiguationData":[OSD([sQuery(id+"F0.wireOp",EDGE,"E449"),sQuery(id+"F0.wireOp",EDGE,"E450"),sQuery(id+"F0.wireOp",EDGE,"E451"),sQuery(id+"F0.wireOp",EDGE,"E452"),sQuery(id+"F0.wireOp",EDGE,"E453"),sQuery(id+"F0.wireOp",EDGE,"E454"),sQuery(id+"F0.wireOp",EDGE,"E455"),sQuery(id+"F0.wireOp",EDGE,"E456")])],"isStart":false});
            var Q24;
            Q24=makeQuery(id+"F1.opExtrude","CAP_FACE",FACE,{"disambiguationData":[OSD([sQuery(id+"F0.wireOp",EDGE,"E443"),sQuery(id+"F0.wireOp",EDGE,"E444"),sQuery(id+"F0.wireOp",EDGE,"E445"),sQuery(id+"F0.wireOp",EDGE,"E446"),sQuery(id+"F0.wireOp",EDGE,"E447"),sQuery(id+"F0.wireOp",EDGE,"E448")])],"isStart":false});
            var Q25;
            Q25=makeQuery(id+"F1.opExtrude","CAP_FACE",FACE,{"disambiguationData":[OSD([sQuery(id+"F0.wireOp",EDGE,"E434"),sQuery(id+"F0.wireOp",EDGE,"E435"),sQuery(id+"F0.wireOp",EDGE,"E436"),sQuery(id+"F0.wireOp",EDGE,"E437"),sQuery(id+"F0.wireOp",EDGE,"E438"),sQuery(id+"F0.wireOp",EDGE,"E439"),sQuery(id+"F0.wireOp",EDGE,"E440"),sQuery(id+"F0.wireOp",EDGE,"E441"),sQuery(id+"F0.wireOp",EDGE,"E442")])],"isStart":false});
            var Q26;
            Q26=makeQuery(id+"F1.opExtrude","CAP_FACE",FACE,{"disambiguationData":[OSD([sQuery(id+"F0.wireOp",EDGE,"E79"),sQuery(id+"F0.wireOp",EDGE,"E80"),sQuery(id+"F0.wireOp",EDGE,"E81"),sQuery(id+"F0.wireOp",EDGE,"E82"),sQuery(id+"F0.wireOp",EDGE,"E83"),sQuery(id+"F0.wireOp",EDGE,"E84"),sQuery(id+"F0.wireOp",EDGE,"E85"),sQuery(id+"F0.wireOp",EDGE,"E86"),sQuery(id+"F0.wireOp",EDGE,"E87")])],"isStart":false});
            var Q27;
            Q27=makeQuery(id+"F1.opExtrude","CAP_FACE",FACE,{"disambiguationData":[OSD([sQuery(id+"F0.wireOp",EDGE,"E285"),sQuery(id+"F0.wireOp",EDGE,"E286"),sQuery(id+"F0.wireOp",EDGE,"E287"),sQuery(id+"F0.wireOp",EDGE,"E288"),sQuery(id+"F0.wireOp",EDGE,"E289"),sQuery(id+"F0.wireOp",EDGE,"E290"),sQuery(id+"F0.wireOp",EDGE,"E291"),sQuery(id+"F0.wireOp",EDGE,"E292"),sQuery(id+"F0.wireOp",EDGE,"E293"),sQuery(id+"F0.wireOp",EDGE,"E294")])],"isStart":false});
            var Q28;
            Q28=makeQuery(id+"F1.opExtrude","CAP_FACE",FACE,{"disambiguationData":[OSD([sQuery(id+"F0.wireOp",EDGE,"E193"),sQuery(id+"F0.wireOp",EDGE,"E194"),sQuery(id+"F0.wireOp",EDGE,"E195"),sQuery(id+"F0.wireOp",EDGE,"E196"),sQuery(id+"F0.wireOp",EDGE,"E197"),sQuery(id+"F0.wireOp",EDGE,"E198"),sQuery(id+"F0.wireOp",EDGE,"E199"),sQuery(id+"F0.wireOp",EDGE,"E200"),sQuery(id+"F0.wireOp",EDGE,"E201"),sQuery(id+"F0.wireOp",EDGE,"E202"),sQuery(id+"F0.wireOp",EDGE,"E203"),sQuery(id+"F0.wireOp",EDGE,"E204"),sQuery(id+"F0.wireOp",EDGE,"E205"),sQuery(id+"F0.wireOp",EDGE,"E206"),sQuery(id+"F0.wireOp",EDGE,"E207")])],"isStart":false});
            var Q29;
            Q29=makeQuery(id+"F1.opExtrude","CAP_FACE",FACE,{"disambiguationData":[OSD([sQuery(id+"F0.wireOp",EDGE,"E295"),sQuery(id+"F0.wireOp",EDGE,"E296"),sQuery(id+"F0.wireOp",EDGE,"E297"),sQuery(id+"F0.wireOp",EDGE,"E298"),sQuery(id+"F0.wireOp",EDGE,"E299"),sQuery(id+"F0.wireOp",EDGE,"E300"),sQuery(id+"F0.wireOp",EDGE,"E301"),sQuery(id+"F0.wireOp",EDGE,"E302"),sQuery(id+"F0.wireOp",EDGE,"E303"),sQuery(id+"F0.wireOp",EDGE,"E304")])],"isStart":false});
            var Q30;
            Q30=makeQuery(id+"F1.opExtrude","CAP_FACE",FACE,{"disambiguationData":[OSD([sQuery(id+"F0.wireOp",EDGE,"E171"),sQuery(id+"F0.wireOp",EDGE,"E172"),sQuery(id+"F0.wireOp",EDGE,"E173"),sQuery(id+"F0.wireOp",EDGE,"E174"),sQuery(id+"F0.wireOp",EDGE,"E175"),sQuery(id+"F0.wireOp",EDGE,"E176"),sQuery(id+"F0.wireOp",EDGE,"E177"),sQuery(id+"F0.wireOp",EDGE,"E178"),sQuery(id+"F0.wireOp",EDGE,"E179"),sQuery(id+"F0.wireOp",EDGE,"E180"),sQuery(id+"F0.wireOp",EDGE,"E181"),sQuery(id+"F0.wireOp",EDGE,"E182"),sQuery(id+"F0.wireOp",EDGE,"E183"),sQuery(id+"F0.wireOp",EDGE,"E184")])],"isStart":false});
            var Q31;
            Q31=makeQuery(id+"F1.opExtrude","CAP_FACE",FACE,{"disambiguationData":[OSD([sQuery(id+"F0.wireOp",EDGE,"E163"),sQuery(id+"F0.wireOp",EDGE,"E164"),sQuery(id+"F0.wireOp",EDGE,"E165"),sQuery(id+"F0.wireOp",EDGE,"E166"),sQuery(id+"F0.wireOp",EDGE,"E167"),sQuery(id+"F0.wireOp",EDGE,"E168"),sQuery(id+"F0.wireOp",EDGE,"E169"),sQuery(id+"F0.wireOp",EDGE,"E170")])],"isStart":false});
            var Q32;
            Q32=makeQuery(id+"F1.opExtrude","CAP_FACE",FACE,{"disambiguationData":[OSD([sQuery(id+"F0.wireOp",EDGE,"E405"),sQuery(id+"F0.wireOp",EDGE,"E406"),sQuery(id+"F0.wireOp",EDGE,"E407"),sQuery(id+"F0.wireOp",EDGE,"E408"),sQuery(id+"F0.wireOp",EDGE,"E409"),sQuery(id+"F0.wireOp",EDGE,"E410"),sQuery(id+"F0.wireOp",EDGE,"E411"),sQuery(id+"F0.wireOp",EDGE,"E412"),sQuery(id+"F0.wireOp",EDGE,"E413"),sQuery(id+"F0.wireOp",EDGE,"E414")])],"isStart":false});
            var Q33;
            Q33=makeQuery(id+"F1.opExtrude","CAP_FACE",FACE,{"disambiguationData":[OSD([sQuery(id+"F0.wireOp",EDGE,"E372"),sQuery(id+"F0.wireOp",EDGE,"E373"),sQuery(id+"F0.wireOp",EDGE,"E374"),sQuery(id+"F0.wireOp",EDGE,"E375"),sQuery(id+"F0.wireOp",EDGE,"E376"),sQuery(id+"F0.wireOp",EDGE,"E377"),sQuery(id+"F0.wireOp",EDGE,"E378"),sQuery(id+"F0.wireOp",EDGE,"E379"),sQuery(id+"F0.wireOp",EDGE,"E380"),sQuery(id+"F0.wireOp",EDGE,"E381")])],"isStart":false});
            var Q34;
            Q34=makeQuery(id+"F1.opExtrude","CAP_FACE",FACE,{"disambiguationData":[OSD([sQuery(id+"F0.wireOp",EDGE,"E512"),sQuery(id+"F0.wireOp",EDGE,"E513"),sQuery(id+"F0.wireOp",EDGE,"E514"),sQuery(id+"F0.wireOp",EDGE,"E515"),sQuery(id+"F0.wireOp",EDGE,"E516"),sQuery(id+"F0.wireOp",EDGE,"E517"),sQuery(id+"F0.wireOp",EDGE,"E518"),sQuery(id+"F0.wireOp",EDGE,"E519")])],"isStart":false});
            var Q35;
            Q35=makeQuery(id+"F1.opExtrude","CAP_FACE",FACE,{"disambiguationData":[OSD([sQuery(id+"F0.wireOp",EDGE,"E363"),sQuery(id+"F0.wireOp",EDGE,"E364"),sQuery(id+"F0.wireOp",EDGE,"E365"),sQuery(id+"F0.wireOp",EDGE,"E366"),sQuery(id+"F0.wireOp",EDGE,"E367"),sQuery(id+"F0.wireOp",EDGE,"E368"),sQuery(id+"F0.wireOp",EDGE,"E369"),sQuery(id+"F0.wireOp",EDGE,"E370"),sQuery(id+"F0.wireOp",EDGE,"E371")])],"isStart":false});
            var Q36;
            Q36=makeQuery(id+"F1.opExtrude","CAP_FACE",FACE,{"disambiguationData":[OSD([sQuery(id+"F0.wireOp",EDGE,"E524"),sQuery(id+"F0.wireOp",EDGE,"E525"),sQuery(id+"F0.wireOp",EDGE,"E526"),sQuery(id+"F0.wireOp",EDGE,"E527"),sQuery(id+"F0.wireOp",EDGE,"E528"),sQuery(id+"F0.wireOp",EDGE,"E529"),sQuery(id+"F0.wireOp",EDGE,"E530")])],"isStart":false});
            var Q37;
            Q37=makeQuery(id+"F1.opExtrude","CAP_FACE",FACE,{"disambiguationData":[OSD([sQuery(id+"F0.wireOp",EDGE,"E239"),sQuery(id+"F0.wireOp",EDGE,"E240"),sQuery(id+"F0.wireOp",EDGE,"E241"),sQuery(id+"F0.wireOp",EDGE,"E242"),sQuery(id+"F0.wireOp",EDGE,"E243"),sQuery(id+"F0.wireOp",EDGE,"E244"),sQuery(id+"F0.wireOp",EDGE,"E245"),sQuery(id+"F0.wireOp",EDGE,"E246"),sQuery(id+"F0.wireOp",EDGE,"E247"),sQuery(id+"F0.wireOp",EDGE,"E248"),sQuery(id+"F0.wireOp",EDGE,"E249"),sQuery(id+"F0.wireOp",EDGE,"E250"),sQuery(id+"F0.wireOp",EDGE,"E251"),sQuery(id+"F0.wireOp",EDGE,"E252"),sQuery(id+"F0.wireOp",EDGE,"E253"),sQuery(id+"F0.wireOp",EDGE,"E254"),sQuery(id+"F0.wireOp",EDGE,"E255"),sQuery(id+"F0.wireOp",EDGE,"E256")])],"isStart":false});
            var Q38;
            Q38=makeQuery(id+"F1.opExtrude","CAP_FACE",FACE,{"disambiguationData":[OSD([sQuery(id+"F0.wireOp",EDGE,"E325"),sQuery(id+"F0.wireOp",EDGE,"E326"),sQuery(id+"F0.wireOp",EDGE,"E327"),sQuery(id+"F0.wireOp",EDGE,"E328"),sQuery(id+"F0.wireOp",EDGE,"E329"),sQuery(id+"F0.wireOp",EDGE,"E330"),sQuery(id+"F0.wireOp",EDGE,"E331"),sQuery(id+"F0.wireOp",EDGE,"E332"),sQuery(id+"F0.wireOp",EDGE,"E333"),sQuery(id+"F0.wireOp",EDGE,"E334")])],"isStart":false});
            var Q39;
            Q39=makeQuery(id+"F1.opExtrude","CAP_FACE",FACE,{"disambiguationData":[OSD([sQuery(id+"F0.wireOp",EDGE,"E185"),sQuery(id+"F0.wireOp",EDGE,"E186"),sQuery(id+"F0.wireOp",EDGE,"E187"),sQuery(id+"F0.wireOp",EDGE,"E188"),sQuery(id+"F0.wireOp",EDGE,"E189"),sQuery(id+"F0.wireOp",EDGE,"E190"),sQuery(id+"F0.wireOp",EDGE,"E191"),sQuery(id+"F0.wireOp",EDGE,"E192")])],"isStart":false});
            var Q40;
            Q40=makeQuery(id+"F1.opExtrude","CAP_FACE",FACE,{"disambiguationData":[OSD([sQuery(id+"F0.wireOp",EDGE,"E305"),sQuery(id+"F0.wireOp",EDGE,"E306"),sQuery(id+"F0.wireOp",EDGE,"E307"),sQuery(id+"F0.wireOp",EDGE,"E308"),sQuery(id+"F0.wireOp",EDGE,"E309"),sQuery(id+"F0.wireOp",EDGE,"E310"),sQuery(id+"F0.wireOp",EDGE,"E311"),sQuery(id+"F0.wireOp",EDGE,"E312"),sQuery(id+"F0.wireOp",EDGE,"E313")])],"isStart":false});
            var Q41;
            Q41=makeQuery(id+"F1.opExtrude","CAP_FACE",FACE,{"disambiguationData":[OSD([sQuery(id+"F0.wireOp",EDGE,"E387"),sQuery(id+"F0.wireOp",EDGE,"E388"),sQuery(id+"F0.wireOp",EDGE,"E389"),sQuery(id+"F0.wireOp",EDGE,"E390"),sQuery(id+"F0.wireOp",EDGE,"E391"),sQuery(id+"F0.wireOp",EDGE,"E392"),sQuery(id+"F0.wireOp",EDGE,"E393"),sQuery(id+"F0.wireOp",EDGE,"E394"),sQuery(id+"F0.wireOp",EDGE,"E395"),sQuery(id+"F0.wireOp",EDGE,"E396")])],"isStart":false});
            var Q42;
            Q42=makeQuery(id+"F1.opExtrude","CAP_FACE",FACE,{"disambiguationData":[OSD([sQuery(id+"F0.wireOp",EDGE,"E269"),sQuery(id+"F0.wireOp",EDGE,"E270"),sQuery(id+"F0.wireOp",EDGE,"E271"),sQuery(id+"F0.wireOp",EDGE,"E272"),sQuery(id+"F0.wireOp",EDGE,"E273"),sQuery(id+"F0.wireOp",EDGE,"E274"),sQuery(id+"F0.wireOp",EDGE,"E275"),sQuery(id+"F0.wireOp",EDGE,"E276"),sQuery(id+"F0.wireOp",EDGE,"E277")])],"isStart":false});
            var Q43;
            Q43=makeQuery(id+"F1.opExtrude","CAP_FACE",FACE,{"disambiguationData":[OSD([sQuery(id+"F0.wireOp",EDGE,"E257"),sQuery(id+"F0.wireOp",EDGE,"E258"),sQuery(id+"F0.wireOp",EDGE,"E259"),sQuery(id+"F0.wireOp",EDGE,"E260"),sQuery(id+"F0.wireOp",EDGE,"E261"),sQuery(id+"F0.wireOp",EDGE,"E262"),sQuery(id+"F0.wireOp",EDGE,"E263"),sQuery(id+"F0.wireOp",EDGE,"E264"),sQuery(id+"F0.wireOp",EDGE,"E265"),sQuery(id+"F0.wireOp",EDGE,"E266"),sQuery(id+"F0.wireOp",EDGE,"E267"),sQuery(id+"F0.wireOp",EDGE,"E268")])],"isStart":false});
            var Q44;
            Q44=makeQuery(id+"F1.opExtrude","CAP_FACE",FACE,{"disambiguationData":[OSD([sQuery(id+"F0.wireOp",EDGE,"E314"),sQuery(id+"F0.wireOp",EDGE,"E315"),sQuery(id+"F0.wireOp",EDGE,"E316"),sQuery(id+"F0.wireOp",EDGE,"E317"),sQuery(id+"F0.wireOp",EDGE,"E318"),sQuery(id+"F0.wireOp",EDGE,"E319"),sQuery(id+"F0.wireOp",EDGE,"E320"),sQuery(id+"F0.wireOp",EDGE,"E321"),sQuery(id+"F0.wireOp",EDGE,"E322"),sQuery(id+"F0.wireOp",EDGE,"E323"),sQuery(id+"F0.wireOp",EDGE,"E324")])],"isStart":false});
            fillet(context, id + "F3", {"entities" : qUnion([Q0, Q1, Q2, Q3, Q4, Q5, Q6, Q7, Q8, Q9, Q10, Q11, Q12, Q13, Q14, Q15, Q16, Q17, Q18, Q19, Q20, Q21, Q22, Q23, Q24, Q25, Q26, Q27, Q28, Q29, Q30, Q31, Q32, Q33, Q34, Q35, Q36, Q37, Q38, Q39, Q40, Q41, Q42, Q43, Q44]), "radius" : 1.99 * mm, "tangentPropagation" : true, "allowEdgeOverflow" : false});
        }
        {
            var Q0;
            Q0=makeQuery(id+"F1.opExtrude","CAP_FACE",FACE,{"disambiguationData":[OSD([sQuery(id+"F0.wireOp",EDGE,"E335"),sQuery(id+"F0.wireOp",EDGE,"E336"),sQuery(id+"F0.wireOp",EDGE,"E337"),sQuery(id+"F0.wireOp",EDGE,"E338"),sQuery(id+"F0.wireOp",EDGE,"E339"),sQuery(id+"F0.wireOp",EDGE,"E340"),sQuery(id+"F0.wireOp",EDGE,"E341"),sQuery(id+"F0.wireOp",EDGE,"E342"),sQuery(id+"F0.wireOp",EDGE,"E343"),sQuery(id+"F0.wireOp",EDGE,"E344"),sQuery(id+"F0.wireOp",EDGE,"E345"),sQuery(id+"F0.wireOp",EDGE,"E346"),sQuery(id+"F0.wireOp",EDGE,"E347"),sQuery(id+"F0.wireOp",EDGE,"E348"),sQuery(id+"F0.wireOp",EDGE,"E349")])],"isStart":false});
            var Q1;
            Q1=makeQuery(id+"F1.opExtrude","CAP_FACE",FACE,{"disambiguationData":[OSD([sQuery(id+"F0.wireOp",EDGE,"E531"),sQuery(id+"F0.wireOp",EDGE,"E532"),sQuery(id+"F0.wireOp",EDGE,"E533"),sQuery(id+"F0.wireOp",EDGE,"E534"),sQuery(id+"F0.wireOp",EDGE,"E535"),sQuery(id+"F0.wireOp",EDGE,"E536"),sQuery(id+"F0.wireOp",EDGE,"E537"),sQuery(id+"F0.wireOp",EDGE,"E538")])],"isStart":false});
            var Q2;
            Q2=makeQuery(id+"F1.opExtrude","CAP_FACE",FACE,{"disambiguationData":[OSD([sQuery(id+"F0.wireOp",EDGE,"E539"),sQuery(id+"F0.wireOp",EDGE,"E540"),sQuery(id+"F0.wireOp",EDGE,"E541"),sQuery(id+"F0.wireOp",EDGE,"E542"),sQuery(id+"F0.wireOp",EDGE,"E543")])],"isStart":false});
            var Q3;
            Q3=makeQuery(id+"F1.opExtrude","CAP_FACE",FACE,{"disambiguationData":[OSD([sQuery(id+"F0.wireOp",EDGE,"E422"),sQuery(id+"F0.wireOp",EDGE,"E423"),sQuery(id+"F0.wireOp",EDGE,"E424"),sQuery(id+"F0.wireOp",EDGE,"E425"),sQuery(id+"F0.wireOp",EDGE,"E426"),sQuery(id+"F0.wireOp",EDGE,"E427"),sQuery(id+"F0.wireOp",EDGE,"E428"),sQuery(id+"F0.wireOp",EDGE,"E429"),sQuery(id+"F0.wireOp",EDGE,"E430"),sQuery(id+"F0.wireOp",EDGE,"E431"),sQuery(id+"F0.wireOp",EDGE,"E432"),sQuery(id+"F0.wireOp",EDGE,"E433")])],"isStart":false});
            var Q4;
            Q4=makeQuery(id+"F1.opExtrude","CAP_FACE",FACE,{"disambiguationData":[OSD([sQuery(id+"F0.wireOp",EDGE,"E415"),sQuery(id+"F0.wireOp",EDGE,"E416"),sQuery(id+"F0.wireOp",EDGE,"E417"),sQuery(id+"F0.wireOp",EDGE,"E418"),sQuery(id+"F0.wireOp",EDGE,"E419"),sQuery(id+"F0.wireOp",EDGE,"E420"),sQuery(id+"F0.wireOp",EDGE,"E421")])],"isStart":false});
            var Q5;
            Q5=makeQuery(id+"F1.opExtrude","CAP_FACE",FACE,{"disambiguationData":[OSD([sQuery(id+"F0.wireOp",EDGE,"E382"),sQuery(id+"F0.wireOp",EDGE,"E383"),sQuery(id+"F0.wireOp",EDGE,"E384"),sQuery(id+"F0.wireOp",EDGE,"E385"),sQuery(id+"F0.wireOp",EDGE,"E386")])],"isStart":false});
            var Q6;
            Q6=makeQuery(id+"F1.opExtrude","CAP_FACE",FACE,{"disambiguationData":[OSD([sQuery(id+"F0.wireOp",EDGE,"E278"),sQuery(id+"F0.wireOp",EDGE,"E279"),sQuery(id+"F0.wireOp",EDGE,"E280"),sQuery(id+"F0.wireOp",EDGE,"E281"),sQuery(id+"F0.wireOp",EDGE,"E282"),sQuery(id+"F0.wireOp",EDGE,"E283"),sQuery(id+"F0.wireOp",EDGE,"E284")])],"isStart":false});
            var Q7;
            Q7=makeQuery(id+"F1.opExtrude","CAP_FACE",FACE,{"disambiguationData":[OSD([sQuery(id+"F0.wireOp",EDGE,"E219"),sQuery(id+"F0.wireOp",EDGE,"E220"),sQuery(id+"F0.wireOp",EDGE,"E221"),sQuery(id+"F0.wireOp",EDGE,"E222"),sQuery(id+"F0.wireOp",EDGE,"E223"),sQuery(id+"F0.wireOp",EDGE,"E224"),sQuery(id+"F0.wireOp",EDGE,"E225")])],"isStart":false});
            var Q8;
            Q8=makeQuery(id+"F1.opExtrude","CAP_FACE",FACE,{"disambiguationData":[OSD([sQuery(id+"F0.wireOp",EDGE,"E208"),sQuery(id+"F0.wireOp",EDGE,"E209"),sQuery(id+"F0.wireOp",EDGE,"E210"),sQuery(id+"F0.wireOp",EDGE,"E211"),sQuery(id+"F0.wireOp",EDGE,"E212"),sQuery(id+"F0.wireOp",EDGE,"E213")])],"isStart":false});
            fillet(context, id + "F4", {"entities" : qUnion([Q0, Q1, Q2, Q3, Q4, Q5, Q6, Q7, Q8]), "radius" : 1.6 * mm, "tangentPropagation" : true, "allowEdgeOverflow" : false});
        }
        {
            var Q0;
            Q0=makeQuery(id+"F1.opExtrude","SWEPT_EDGE",EDGE,{"disambiguationData":[OSD([sQuery(id+"F0.wireOp",EDGE,"E354"),sQuery(id+"F0.wireOp",EDGE,"E355")])]});
            fillet(context, id + "F5", {"entities" : qUnion([Q0]), "radius" : 5 * mm, "tangentPropagation" : true, "allowEdgeOverflow" : false});
        }
        {
            var Q0;
            Q0=makeQuery(id+"F1.opExtrude","CAP_FACE",FACE,{"disambiguationData":[OSD([sQuery(id+"F0.wireOp",EDGE,"E350"),sQuery(id+"F0.wireOp",EDGE,"E351"),sQuery(id+"F0.wireOp",EDGE,"E352"),sQuery(id+"F0.wireOp",EDGE,"E353"),sQuery(id+"F0.wireOp",EDGE,"E354"),sQuery(id+"F0.wireOp",EDGE,"E355"),sQuery(id+"F0.wireOp",EDGE,"E356"),sQuery(id+"F0.wireOp",EDGE,"E357"),sQuery(id+"F0.wireOp",EDGE,"E358"),sQuery(id+"F0.wireOp",EDGE,"E359"),sQuery(id+"F0.wireOp",EDGE,"E360"),sQuery(id+"F0.wireOp",EDGE,"E361"),sQuery(id+"F0.wireOp",EDGE,"E362")])],"isStart":false});
            var Q1;
            Q1=makeQuery(id+"F1.opExtrude","CAP_FACE",FACE,{"disambiguationData":[OSD([sQuery(id+"F0.wireOp",EDGE,"E397"),sQuery(id+"F0.wireOp",EDGE,"E398"),sQuery(id+"F0.wireOp",EDGE,"E399"),sQuery(id+"F0.wireOp",EDGE,"E400"),sQuery(id+"F0.wireOp",EDGE,"E401"),sQuery(id+"F0.wireOp",EDGE,"E402"),sQuery(id+"F0.wireOp",EDGE,"E403"),sQuery(id+"F0.wireOp",EDGE,"E404")])],"isStart":false});
            var Q2;
            Q2=makeQuery(id+"F1.opExtrude","CAP_FACE",FACE,{"disambiguationData":[OSD([sQuery(id+"F0.wireOp",EDGE,"E520"),sQuery(id+"F0.wireOp",EDGE,"E521"),sQuery(id+"F0.wireOp",EDGE,"E522"),sQuery(id+"F0.wireOp",EDGE,"E523")])],"isStart":false});
            var Q3;
            Q3=makeQuery(id+"F1.opExtrude","CAP_FACE",FACE,{"disambiguationData":[OSD([sQuery(id+"F0.wireOp",EDGE,"E214"),sQuery(id+"F0.wireOp",EDGE,"E215"),sQuery(id+"F0.wireOp",EDGE,"E216"),sQuery(id+"F0.wireOp",EDGE,"E217"),sQuery(id+"F0.wireOp",EDGE,"E218")])],"isStart":false});
            fillet(context, id + "F6", {"entities" : qUnion([Q0, Q1, Q2, Q3]), "radius" : .9 * mm, "tangentPropagation" : true, "allowEdgeOverflow" : false});
        }
    });
